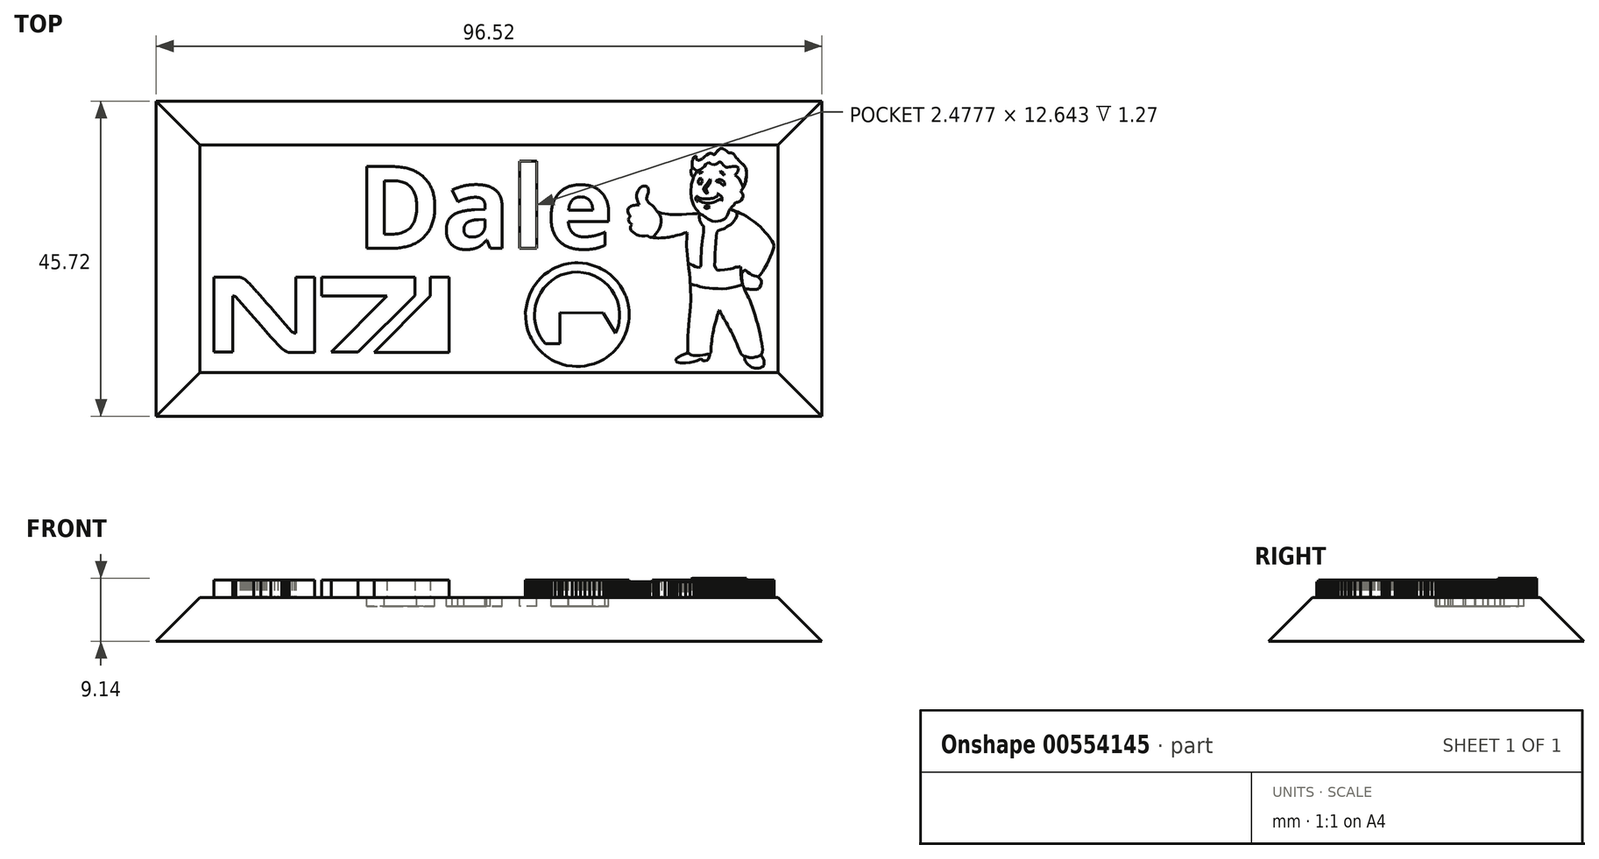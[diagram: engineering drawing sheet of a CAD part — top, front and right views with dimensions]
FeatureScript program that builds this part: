
annotation { "Feature Type Name" : "Feature", "Feature Type Description" : "" }
export const myFeature = defineFeature(function(context is Context, id is Id, definition is map)
    precondition{}
    {
        {
            var Q0;
            Q0=qCreatedBy(makeId("Top.planeOp"),FACE);
            var sketch = newSketch(context, id + "F0", { "sketchPlane" : qUnion([Q0])});
            skLineSegment(sketch, "E0.bottom", {"start": v(50.8, -25.4) * mm, "end": v(-50.8, -25.4) * mm});
            skLineSegment(sketch, "E0.top", {"start": v(50.8, 25.4) * mm, "end": v(-50.8, 25.4) * mm});
            skLineSegment(sketch, "E0.left", {"start": v(50.8, -25.4) * mm, "end": v(50.8, 25.4) * mm});
            skLineSegment(sketch, "E0.right", {"start": v(-50.8, -25.4) * mm, "end": v(-50.8, 25.4) * mm});
            skPoint(sketch, "E0.middle", {"position": v(0, 0) * mm});
            skSolve(sketch);
        }
        {
            var Q0;
            Q0 = qSketchRegion(id + "F0", true);
            extrude(context, id + "F1", {"entities" : qUnion([Q0]), "depth" : 6.35 * mm, "offsetDistance" : 25.4 * mm});
        }
        {
            var Q0;
            Q0=makeQuery(id+"F1.opExtrude","CAP_EDGE",EDGE,{"disambiguationData":[OSD([sQuery(id+"F0.wireOp",EDGE,"E0.right")])],"isStart":false});
            var Q1;
            Q1=makeQuery(id+"F1.opExtrude","CAP_EDGE",EDGE,{"disambiguationData":[OSD([sQuery(id+"F0.wireOp",EDGE,"E0.top")])],"isStart":false});
            var Q2;
            Q2=makeQuery(id+"F1.opExtrude","CAP_EDGE",EDGE,{"disambiguationData":[OSD([sQuery(id+"F0.wireOp",EDGE,"E0.left")])],"isStart":false});
            var Q3;
            Q3=makeQuery(id+"F1.opExtrude","CAP_EDGE",EDGE,{"disambiguationData":[OSD([sQuery(id+"F0.wireOp",EDGE,"E0.bottom")])],"isStart":false});
            chamfer(context, id + "F2", {"entities" : qUnion([Q0, Q1, Q2, Q3]), "width" : 8.9 * mm, "tangentPropagation" : true});
        }
        {
            var Q0;
            Q0=makeQuery(id+"F1.opExtrude","CAP_FACE",FACE,{"disambiguationData":[OSD([sQuery(id+"F0.wireOp",EDGE,"E0.bottom"),sQuery(id+"F0.wireOp",EDGE,"E0.top"),sQuery(id+"F0.wireOp",EDGE,"E0.left"),sQuery(id+"F0.wireOp",EDGE,"E0.right")])],"isStart":false});
            var sketch = newSketch(context, id + "F3", { "sketchPlane" : qUnion([Q0])});
            skText(sketch, "E1", { "text": "Dale", "fontName": "OpenSans-Bold.ttf"});
            const initialGuessF3  = {"E1": [-0.01922, 0.00149, 1, 0, 0.01198]};
            skSetInitialGuess(sketch, initialGuessF3);
            skSolve(sketch);
        }
        {
            var Q0;
            Q0=makeQuery(id+"F3.imprint","IMPRINT",FACE,{"disambiguationData":[TD([[makeQuery(id+"F3.imprint","IMPRINT",EDGE,{"derivedFrom":sQuery(id+"F3.wireOp",EDGE,"E1.sketch_text.stroke-0")}),1.0]])]});
            var sketch = newSketch(context, id + "F4", { "sketchPlane" : qUnion([Q0])});
            skLineSegment(sketch, "E2", {"start": v(21.69, 8.01) * mm, "end": v(21.57, 8.24) * mm});
            skLineSegment(sketch, "E3", {"start": v(21.57, 8.24) * mm, "end": v(21.48, 8.48) * mm});
            skLineSegment(sketch, "E4", {"start": v(21.48, 8.48) * mm, "end": v(21.44, 8.64) * mm});
            skLineSegment(sketch, "E5", {"start": v(21.44, 8.64) * mm, "end": v(21.4, 8.93) * mm});
            skLineSegment(sketch, "E6", {"start": v(21.4, 8.93) * mm, "end": v(21.4, 9.24) * mm});
            skLineSegment(sketch, "E7", {"start": v(21.4, 9.24) * mm, "end": v(21.44, 9.52) * mm});
            skLineSegment(sketch, "E8", {"start": v(21.44, 9.52) * mm, "end": v(21.55, 9.82) * mm});
            skLineSegment(sketch, "E9", {"start": v(21.55, 9.82) * mm, "end": v(21.7, 10.05) * mm});
            skLineSegment(sketch, "E10", {"start": v(21.7, 10.05) * mm, "end": v(21.83, 10.2) * mm});
            skLineSegment(sketch, "E11", {"start": v(21.83, 10.2) * mm, "end": v(21.96, 10.34) * mm});
            skLineSegment(sketch, "E12", {"start": v(21.96, 10.34) * mm, "end": v(22.13, 10.44) * mm});
            skLineSegment(sketch, "E13", {"start": v(22.13, 10.44) * mm, "end": v(22.33, 10.53) * mm});
            skLineSegment(sketch, "E14", {"start": v(22.33, 10.53) * mm, "end": v(22.48, 10.55) * mm});
            skLineSegment(sketch, "E15", {"start": v(22.48, 10.55) * mm, "end": v(22.6, 10.55) * mm});
            skLineSegment(sketch, "E16", {"start": v(22.6, 10.55) * mm, "end": v(22.73, 10.54) * mm});
            skLineSegment(sketch, "E17", {"start": v(22.73, 10.54) * mm, "end": v(22.84, 10.5) * mm});
            skLineSegment(sketch, "E18", {"start": v(22.84, 10.5) * mm, "end": v(22.95, 10.38) * mm});
            skLineSegment(sketch, "E19", {"start": v(22.95, 10.38) * mm, "end": v(23.04, 10.2) * mm});
            skLineSegment(sketch, "E20", {"start": v(23.04, 10.2) * mm, "end": v(23.08, 10.07) * mm});
            skLineSegment(sketch, "E21", {"start": v(23.08, 10.07) * mm, "end": v(23.12, 9.92) * mm});
            skLineSegment(sketch, "E22", {"start": v(23.12, 9.92) * mm, "end": v(23.12, 9.76) * mm});
            skLineSegment(sketch, "E23", {"start": v(23.12, 9.76) * mm, "end": v(23.07, 9.57) * mm});
            skLineSegment(sketch, "E24", {"start": v(23.07, 9.57) * mm, "end": v(23.04, 9.45) * mm});
            skLineSegment(sketch, "E25", {"start": v(23.04, 9.45) * mm, "end": v(22.98, 9.3) * mm});
            skLineSegment(sketch, "E26", {"start": v(22.98, 9.3) * mm, "end": v(22.92, 9.15) * mm});
            skLineSegment(sketch, "E27", {"start": v(22.92, 9.15) * mm, "end": v(22.88, 9) * mm});
            skLineSegment(sketch, "E28", {"start": v(22.88, 9) * mm, "end": v(22.85, 8.83) * mm});
            skLineSegment(sketch, "E29", {"start": v(22.85, 8.83) * mm, "end": v(22.86, 8.62) * mm});
            skLineSegment(sketch, "E30", {"start": v(22.86, 8.62) * mm, "end": v(22.96, 8.38) * mm});
            skLineSegment(sketch, "E31", {"start": v(22.96, 8.38) * mm, "end": v(23.1, 8.2) * mm});
            skLineSegment(sketch, "E32", {"start": v(23.1, 8.2) * mm, "end": v(23.3, 8) * mm});
            skLineSegment(sketch, "E33", {"start": v(23.3, 8) * mm, "end": v(23.47, 7.88) * mm});
            skLineSegment(sketch, "E34", {"start": v(23.47, 7.88) * mm, "end": v(23.66, 7.74) * mm});
            skLineSegment(sketch, "E35", {"start": v(23.66, 7.74) * mm, "end": v(23.84, 7.54) * mm});
            skLineSegment(sketch, "E36", {"start": v(23.84, 7.54) * mm, "end": v(24.05, 7.29) * mm});
            skLineSegment(sketch, "E37", {"start": v(24.05, 7.29) * mm, "end": v(24.21, 7.04) * mm});
            skLineSegment(sketch, "E38", {"start": v(24.21, 7.04) * mm, "end": v(24.3, 6.9) * mm});
            skLineSegment(sketch, "E39", {"start": v(24.3, 6.9) * mm, "end": v(24.41, 6.8) * mm});
            skLineSegment(sketch, "E40", {"start": v(24.41, 6.8) * mm, "end": v(24.66, 6.73) * mm});
            skLineSegment(sketch, "E41", {"start": v(24.66, 6.73) * mm, "end": v(25.02, 6.62) * mm});
            skLineSegment(sketch, "E42", {"start": v(25.02, 6.62) * mm, "end": v(25.48, 6.54) * mm});
            skLineSegment(sketch, "E43", {"start": v(25.48, 6.54) * mm, "end": v(25.95, 6.46) * mm});
            skLineSegment(sketch, "E44", {"start": v(25.95, 6.46) * mm, "end": v(26.28, 6.44) * mm});
            skLineSegment(sketch, "E45", {"start": v(26.28, 6.44) * mm, "end": v(26.73, 6.42) * mm});
            skLineSegment(sketch, "E46", {"start": v(26.73, 6.42) * mm, "end": v(27.3, 6.41) * mm});
            skLineSegment(sketch, "E47", {"start": v(27.3, 6.41) * mm, "end": v(27.91, 6.42) * mm});
            skLineSegment(sketch, "E48", {"start": v(27.91, 6.42) * mm, "end": v(28.6, 6.45) * mm});
            skLineSegment(sketch, "E49", {"start": v(28.6, 6.45) * mm, "end": v(29.5, 6.53) * mm});
            skLineSegment(sketch, "E50", {"start": v(29.5, 6.53) * mm, "end": v(30.08, 6.55) * mm});
            skLineSegment(sketch, "E51", {"start": v(30.08, 6.55) * mm, "end": v(30.33, 6.58) * mm});
            skLineSegment(sketch, "E52", {"start": v(30.33, 6.58) * mm, "end": v(30.4, 6.63) * mm});
            skLineSegment(sketch, "E53", {"start": v(30.4, 6.63) * mm, "end": v(30.4, 6.72) * mm});
            skLineSegment(sketch, "E54", {"start": v(30.4, 6.72) * mm, "end": v(30.35, 6.78) * mm});
            skLineSegment(sketch, "E55", {"start": v(30.35, 6.78) * mm, "end": v(30.3, 6.86) * mm});
            skLineSegment(sketch, "E56", {"start": v(30.3, 6.86) * mm, "end": v(30.2, 6.99) * mm});
            skLineSegment(sketch, "E57", {"start": v(30.2, 6.99) * mm, "end": v(30.04, 7.2) * mm});
            skLineSegment(sketch, "E58", {"start": v(30.04, 7.2) * mm, "end": v(29.9, 7.35) * mm});
            skLineSegment(sketch, "E59", {"start": v(29.9, 7.35) * mm, "end": v(29.8, 7.53) * mm});
            skLineSegment(sketch, "E60", {"start": v(29.8, 7.53) * mm, "end": v(29.72, 7.67) * mm});
            skLineSegment(sketch, "E61", {"start": v(29.72, 7.67) * mm, "end": v(29.65, 7.82) * mm});
            skLineSegment(sketch, "E62", {"start": v(29.65, 7.82) * mm, "end": v(29.56, 7.99) * mm});
            skLineSegment(sketch, "E63", {"start": v(29.56, 7.99) * mm, "end": v(29.49, 8.16) * mm});
            skLineSegment(sketch, "E64", {"start": v(29.49, 8.16) * mm, "end": v(29.43, 8.35) * mm});
            skLineSegment(sketch, "E65", {"start": v(29.43, 8.35) * mm, "end": v(29.39, 8.57) * mm});
            skLineSegment(sketch, "E66", {"start": v(29.39, 8.57) * mm, "end": v(29.34, 8.8) * mm});
            skLineSegment(sketch, "E67", {"start": v(29.34, 8.8) * mm, "end": v(29.3, 9.12) * mm});
            skLineSegment(sketch, "E68", {"start": v(29.3, 9.12) * mm, "end": v(29.28, 9.38) * mm});
            skLineSegment(sketch, "E69", {"start": v(29.28, 9.38) * mm, "end": v(29.27, 9.73) * mm});
            skLineSegment(sketch, "E70", {"start": v(29.27, 9.73) * mm, "end": v(29.27, 10.04) * mm});
            skLineSegment(sketch, "E71", {"start": v(29.27, 10.04) * mm, "end": v(29.3, 10.42) * mm});
            skLineSegment(sketch, "E72", {"start": v(29.3, 10.42) * mm, "end": v(29.35, 10.8) * mm});
            skLineSegment(sketch, "E73", {"start": v(29.35, 10.8) * mm, "end": v(29.43, 11.17) * mm});
            skLineSegment(sketch, "E74", {"start": v(29.43, 11.17) * mm, "end": v(29.56, 11.55) * mm});
            skLineSegment(sketch, "E75", {"start": v(29.56, 11.55) * mm, "end": v(29.63, 11.82) * mm});
            skLineSegment(sketch, "E76", {"start": v(29.63, 11.82) * mm, "end": v(29.53, 11.9) * mm});
            skLineSegment(sketch, "E77", {"start": v(29.53, 11.9) * mm, "end": v(29.4, 12.05) * mm});
            skLineSegment(sketch, "E78", {"start": v(29.4, 12.05) * mm, "end": v(29.32, 12.29) * mm});
            skLineSegment(sketch, "E79", {"start": v(29.32, 12.29) * mm, "end": v(29.27, 12.55) * mm});
            skLineSegment(sketch, "E80", {"start": v(29.27, 12.55) * mm, "end": v(29.27, 12.8) * mm});
            skLineSegment(sketch, "E81", {"start": v(29.27, 12.8) * mm, "end": v(29.35, 13) * mm});
            skLineSegment(sketch, "E82", {"start": v(29.35, 13) * mm, "end": v(29.44, 13.12) * mm});
            skLineSegment(sketch, "E83", {"start": v(29.44, 13.12) * mm, "end": v(29.5, 13.2) * mm});
            skLineSegment(sketch, "E84", {"start": v(29.5, 13.2) * mm, "end": v(29.46, 13.38) * mm});
            skLineSegment(sketch, "E85", {"start": v(29.46, 13.38) * mm, "end": v(29.43, 13.67) * mm});
            skLineSegment(sketch, "E86", {"start": v(29.43, 13.67) * mm, "end": v(29.43, 13.88) * mm});
            skLineSegment(sketch, "E87", {"start": v(29.43, 13.88) * mm, "end": v(29.46, 14.12) * mm});
            skLineSegment(sketch, "E88", {"start": v(29.46, 14.12) * mm, "end": v(29.5, 14.3) * mm});
            skLineSegment(sketch, "E89", {"start": v(29.5, 14.3) * mm, "end": v(29.57, 14.47) * mm});
            skLineSegment(sketch, "E90", {"start": v(29.57, 14.47) * mm, "end": v(29.65, 14.66) * mm});
            skLineSegment(sketch, "E91", {"start": v(29.65, 14.66) * mm, "end": v(29.8, 14.81) * mm});
            skLineSegment(sketch, "E92", {"start": v(29.8, 14.81) * mm, "end": v(29.9, 14.89) * mm});
            skLineSegment(sketch, "E93", {"start": v(29.9, 14.89) * mm, "end": v(29.96, 14.92) * mm});
            skLineSegment(sketch, "E94", {"start": v(29.96, 14.92) * mm, "end": v(30, 14.76) * mm});
            skLineSegment(sketch, "E95", {"start": v(30, 14.76) * mm, "end": v(30, 14.63) * mm});
            skLineSegment(sketch, "E96", {"start": v(30, 14.63) * mm, "end": v(30.03, 14.45) * mm});
            skLineSegment(sketch, "E97", {"start": v(30.03, 14.45) * mm, "end": v(30.14, 14.34) * mm});
            skLineSegment(sketch, "E98", {"start": v(30.14, 14.34) * mm, "end": v(30.3, 14.27) * mm});
            skLineSegment(sketch, "E99", {"start": v(30.3, 14.27) * mm, "end": v(30.48, 14.29) * mm});
            skLineSegment(sketch, "E100", {"start": v(30.48, 14.29) * mm, "end": v(30.72, 14.4) * mm});
            skLineSegment(sketch, "E101", {"start": v(30.72, 14.4) * mm, "end": v(30.92, 14.52) * mm});
            skLineSegment(sketch, "E102", {"start": v(30.92, 14.52) * mm, "end": v(31.1, 14.69) * mm});
            skLineSegment(sketch, "E103", {"start": v(31.1, 14.69) * mm, "end": v(31.3, 14.85) * mm});
            skLineSegment(sketch, "E104", {"start": v(31.3, 14.85) * mm, "end": v(31.48, 15.01) * mm});
            skLineSegment(sketch, "E105", {"start": v(31.48, 15.01) * mm, "end": v(31.73, 15.17) * mm});
            skLineSegment(sketch, "E106", {"start": v(31.73, 15.17) * mm, "end": v(31.97, 15.29) * mm});
            skLineSegment(sketch, "E107", {"start": v(31.97, 15.29) * mm, "end": v(32.15, 15.3) * mm});
            skLineSegment(sketch, "E108", {"start": v(32.15, 15.3) * mm, "end": v(32.31, 15.22) * mm});
            skLineSegment(sketch, "E109", {"start": v(32.31, 15.22) * mm, "end": v(32.45, 15.13) * mm});
            skLineSegment(sketch, "E110", {"start": v(32.45, 15.13) * mm, "end": v(32.49, 15.12) * mm});
            skLineSegment(sketch, "E111", {"start": v(32.49, 15.12) * mm, "end": v(32.53, 15.1) * mm});
            skLineSegment(sketch, "E112", {"start": v(32.53, 15.1) * mm, "end": v(32.58, 15.1) * mm});
            skLineSegment(sketch, "E113", {"start": v(32.58, 15.1) * mm, "end": v(32.63, 15.13) * mm});
            skLineSegment(sketch, "E114", {"start": v(32.63, 15.13) * mm, "end": v(32.68, 15.17) * mm});
            skLineSegment(sketch, "E115", {"start": v(32.68, 15.17) * mm, "end": v(32.78, 15.24) * mm});
            skLineSegment(sketch, "E116", {"start": v(32.78, 15.24) * mm, "end": v(32.88, 15.36) * mm});
            skLineSegment(sketch, "E117", {"start": v(32.88, 15.36) * mm, "end": v(32.97, 15.49) * mm});
            skLineSegment(sketch, "E118", {"start": v(32.97, 15.49) * mm, "end": v(33.1, 15.61) * mm});
            skLineSegment(sketch, "E119", {"start": v(33.1, 15.61) * mm, "end": v(33.22, 15.72) * mm});
            skLineSegment(sketch, "E120", {"start": v(33.22, 15.72) * mm, "end": v(33.35, 15.83) * mm});
            skLineSegment(sketch, "E121", {"start": v(33.35, 15.83) * mm, "end": v(33.48, 15.93) * mm});
            skLineSegment(sketch, "E122", {"start": v(33.48, 15.93) * mm, "end": v(33.62, 15.99) * mm});
            skLineSegment(sketch, "E123", {"start": v(33.62, 15.99) * mm, "end": v(33.76, 16) * mm});
            skLineSegment(sketch, "E124", {"start": v(33.76, 16) * mm, "end": v(33.94, 15.94) * mm});
            skLineSegment(sketch, "E125", {"start": v(33.94, 15.94) * mm, "end": v(34.13, 15.85) * mm});
            skLineSegment(sketch, "E126", {"start": v(34.13, 15.85) * mm, "end": v(34.3, 15.72) * mm});
            skLineSegment(sketch, "E127", {"start": v(34.3, 15.72) * mm, "end": v(34.44, 15.57) * mm});
            skLineSegment(sketch, "E128", {"start": v(34.44, 15.57) * mm, "end": v(34.58, 15.45) * mm});
            skLineSegment(sketch, "E129", {"start": v(34.58, 15.45) * mm, "end": v(34.71, 15.38) * mm});
            skLineSegment(sketch, "E130", {"start": v(34.71, 15.38) * mm, "end": v(34.9, 15.34) * mm});
            skLineSegment(sketch, "E131", {"start": v(34.9, 15.34) * mm, "end": v(35.13, 15.34) * mm});
            skLineSegment(sketch, "E132", {"start": v(35.13, 15.34) * mm, "end": v(35.32, 15.31) * mm});
            skLineSegment(sketch, "E133", {"start": v(35.32, 15.31) * mm, "end": v(35.43, 15.2) * mm});
            skLineSegment(sketch, "E134", {"start": v(35.43, 15.2) * mm, "end": v(35.52, 15.11) * mm});
            skLineSegment(sketch, "E135", {"start": v(35.52, 15.11) * mm, "end": v(35.58, 15.02) * mm});
            skLineSegment(sketch, "E136", {"start": v(35.58, 15.02) * mm, "end": v(35.7, 14.87) * mm});
            skLineSegment(sketch, "E137", {"start": v(35.7, 14.87) * mm, "end": v(35.79, 14.73) * mm});
            skLineSegment(sketch, "E138", {"start": v(35.79, 14.73) * mm, "end": v(35.87, 14.63) * mm});
            skLineSegment(sketch, "E139", {"start": v(35.87, 14.63) * mm, "end": v(35.96, 14.54) * mm});
            skLineSegment(sketch, "E140", {"start": v(35.96, 14.54) * mm, "end": v(36.06, 14.43) * mm});
            skLineSegment(sketch, "E141", {"start": v(36.06, 14.43) * mm, "end": v(36.19, 14.29) * mm});
            skLineSegment(sketch, "E142", {"start": v(36.19, 14.29) * mm, "end": v(36.27, 14.19) * mm});
            skLineSegment(sketch, "E143", {"start": v(36.27, 14.19) * mm, "end": v(36.33, 14.11) * mm});
            skLineSegment(sketch, "E144", {"start": v(36.33, 14.11) * mm, "end": v(36.4, 14.04) * mm});
            skLineSegment(sketch, "E145", {"start": v(36.4, 14.04) * mm, "end": v(36.49, 13.96) * mm});
            skLineSegment(sketch, "E146", {"start": v(36.49, 13.96) * mm, "end": v(36.56, 13.88) * mm});
            skLineSegment(sketch, "E147", {"start": v(36.56, 13.88) * mm, "end": v(36.67, 13.78) * mm});
            skLineSegment(sketch, "E148", {"start": v(36.67, 13.78) * mm, "end": v(36.8, 13.69) * mm});
            skLineSegment(sketch, "E149", {"start": v(36.8, 13.69) * mm, "end": v(36.93, 13.55) * mm});
            skLineSegment(sketch, "E150", {"start": v(36.93, 13.55) * mm, "end": v(37.04, 13.42) * mm});
            skLineSegment(sketch, "E151", {"start": v(37.04, 13.42) * mm, "end": v(37.17, 13.2) * mm});
            skLineSegment(sketch, "E152", {"start": v(37.17, 13.2) * mm, "end": v(37.25, 13) * mm});
            skLineSegment(sketch, "E153", {"start": v(37.25, 13) * mm, "end": v(37.3, 12.76) * mm});
            skLineSegment(sketch, "E154", {"start": v(37.3, 12.76) * mm, "end": v(37.33, 12.47) * mm});
            skLineSegment(sketch, "E155", {"start": v(37.33, 12.47) * mm, "end": v(37.35, 12.23) * mm});
            skLineSegment(sketch, "E156", {"start": v(37.35, 12.23) * mm, "end": v(37.33, 11.98) * mm});
            skLineSegment(sketch, "E157", {"start": v(37.33, 11.98) * mm, "end": v(37.32, 11.78) * mm});
            skLineSegment(sketch, "E158", {"start": v(37.32, 11.78) * mm, "end": v(37.26, 11.57) * mm});
            skLineSegment(sketch, "E159", {"start": v(37.26, 11.57) * mm, "end": v(37.22, 11.31) * mm});
            skLineSegment(sketch, "E160", {"start": v(37.22, 11.31) * mm, "end": v(37.17, 11.1) * mm});
            skLineSegment(sketch, "E161", {"start": v(37.17, 11.1) * mm, "end": v(37.11, 10.92) * mm});
            skLineSegment(sketch, "E162", {"start": v(37.11, 10.92) * mm, "end": v(37.05, 10.74) * mm});
            skLineSegment(sketch, "E163", {"start": v(37.05, 10.74) * mm, "end": v(36.97, 10.58) * mm});
            skLineSegment(sketch, "E164", {"start": v(36.97, 10.58) * mm, "end": v(36.87, 10.34) * mm});
            skLineSegment(sketch, "E165", {"start": v(36.87, 10.34) * mm, "end": v(36.74, 10.15) * mm});
            skLineSegment(sketch, "E166", {"start": v(36.74, 10.15) * mm, "end": v(36.63, 9.98) * mm});
            skLineSegment(sketch, "E167", {"start": v(36.63, 9.98) * mm, "end": v(36.48, 9.83) * mm});
            skLineSegment(sketch, "E168", {"start": v(36.48, 9.83) * mm, "end": v(36.56, 9.63) * mm});
            skLineSegment(sketch, "E169", {"start": v(36.56, 9.63) * mm, "end": v(36.75, 9.46) * mm});
            skLineSegment(sketch, "E170", {"start": v(36.75, 9.46) * mm, "end": v(36.83, 9.22) * mm});
            skLineSegment(sketch, "E171", {"start": v(36.83, 9.22) * mm, "end": v(36.8, 9) * mm});
            skLineSegment(sketch, "E172", {"start": v(36.8, 9) * mm, "end": v(36.74, 8.79) * mm});
            skLineSegment(sketch, "E173", {"start": v(36.74, 8.79) * mm, "end": v(36.56, 8.52) * mm});
            skLineSegment(sketch, "E174", {"start": v(36.56, 8.52) * mm, "end": v(36.4, 8.4) * mm});
            skLineSegment(sketch, "E175", {"start": v(36.4, 8.4) * mm, "end": v(36.18, 8.26) * mm});
            skLineSegment(sketch, "E176", {"start": v(36.18, 8.26) * mm, "end": v(36, 8.2) * mm});
            skLineSegment(sketch, "E177", {"start": v(36, 8.2) * mm, "end": v(35.78, 8.16) * mm});
            skLineSegment(sketch, "E178", {"start": v(35.78, 8.16) * mm, "end": v(35.59, 8.03) * mm});
            skLineSegment(sketch, "E179", {"start": v(35.59, 8.03) * mm, "end": v(35.51, 7.8) * mm});
            skLineSegment(sketch, "E180", {"start": v(35.51, 7.8) * mm, "end": v(35.3, 7.6) * mm});
            skLineSegment(sketch, "E181", {"start": v(35.3, 7.6) * mm, "end": v(35.12, 7.42) * mm});
            skLineSegment(sketch, "E182", {"start": v(35.12, 7.42) * mm, "end": v(35.04, 7.27) * mm});
            skLineSegment(sketch, "E183", {"start": v(35.04, 7.27) * mm, "end": v(35.12, 7.14) * mm});
            skLineSegment(sketch, "E184", {"start": v(35.12, 7.14) * mm, "end": v(35.4, 7.03) * mm});
            skLineSegment(sketch, "E185", {"start": v(35.4, 7.03) * mm, "end": v(35.69, 6.92) * mm});
            skLineSegment(sketch, "E186", {"start": v(35.69, 6.92) * mm, "end": v(36.03, 6.79) * mm});
            skLineSegment(sketch, "E187", {"start": v(36.03, 6.79) * mm, "end": v(36.39, 6.63) * mm});
            skLineSegment(sketch, "E188", {"start": v(36.39, 6.63) * mm, "end": v(36.84, 6.43) * mm});
            skLineSegment(sketch, "E189", {"start": v(36.84, 6.43) * mm, "end": v(37.3, 6.16) * mm});
            skLineSegment(sketch, "E190", {"start": v(37.3, 6.16) * mm, "end": v(37.84, 5.8) * mm});
            skLineSegment(sketch, "E191", {"start": v(37.84, 5.8) * mm, "end": v(38.38, 5.4) * mm});
            skLineSegment(sketch, "E192", {"start": v(38.38, 5.4) * mm, "end": v(38.94, 4.96) * mm});
            skLineSegment(sketch, "E193", {"start": v(38.94, 4.96) * mm, "end": v(39.33, 4.62) * mm});
            skLineSegment(sketch, "E194", {"start": v(39.33, 4.62) * mm, "end": v(39.67, 4.27) * mm});
            skLineSegment(sketch, "E195", {"start": v(39.67, 4.27) * mm, "end": v(40.08, 3.81) * mm});
            skLineSegment(sketch, "E196", {"start": v(40.08, 3.81) * mm, "end": v(40.44, 3.44) * mm});
            skLineSegment(sketch, "E197", {"start": v(40.44, 3.44) * mm, "end": v(40.76, 3) * mm});
            skLineSegment(sketch, "E198", {"start": v(40.76, 3) * mm, "end": v(41, 2.62) * mm});
            skLineSegment(sketch, "E199", {"start": v(41, 2.62) * mm, "end": v(41.2, 2.25) * mm});
            skLineSegment(sketch, "E200", {"start": v(41.2, 2.25) * mm, "end": v(41.33, 1.83) * mm});
            skLineSegment(sketch, "E201", {"start": v(41.33, 1.83) * mm, "end": v(41.22, 1.37) * mm});
            skLineSegment(sketch, "E202", {"start": v(41.22, 1.37) * mm, "end": v(41.02, 0.8) * mm});
            skLineSegment(sketch, "E203", {"start": v(41.02, 0.8) * mm, "end": v(40.76, 0.26) * mm});
            skLineSegment(sketch, "E204", {"start": v(40.76, 0.26) * mm, "end": v(40.54, -0.22) * mm});
            skLineSegment(sketch, "E205", {"start": v(40.54, -0.22) * mm, "end": v(40.29, -0.78) * mm});
            skLineSegment(sketch, "E206", {"start": v(40.29, -0.78) * mm, "end": v(39.95, -1.39) * mm});
            skLineSegment(sketch, "E207", {"start": v(39.95, -1.39) * mm, "end": v(39.67, -1.83) * mm});
            skLineSegment(sketch, "E208", {"start": v(39.67, -1.83) * mm, "end": v(39.35, -2.26) * mm});
            skLineSegment(sketch, "E209", {"start": v(39.35, -2.26) * mm, "end": v(39.07, -2.55) * mm});
            skLineSegment(sketch, "E210", {"start": v(39.07, -2.55) * mm, "end": v(39.01, -2.68) * mm});
            skLineSegment(sketch, "E211", {"start": v(39.01, -2.68) * mm, "end": v(39.25, -2.88) * mm});
            skLineSegment(sketch, "E212", {"start": v(39.25, -2.88) * mm, "end": v(39.4, -3.03) * mm});
            skLineSegment(sketch, "E213", {"start": v(39.4, -3.03) * mm, "end": v(39.48, -3.24) * mm});
            skLineSegment(sketch, "E214", {"start": v(39.48, -3.24) * mm, "end": v(39.48, -3.5) * mm});
            skLineSegment(sketch, "E215", {"start": v(39.48, -3.5) * mm, "end": v(39.42, -3.83) * mm});
            skLineSegment(sketch, "E216", {"start": v(39.42, -3.83) * mm, "end": v(39.25, -4.13) * mm});
            skLineSegment(sketch, "E217", {"start": v(39.25, -4.13) * mm, "end": v(39.1, -4.37) * mm});
            skLineSegment(sketch, "E218", {"start": v(39.1, -4.37) * mm, "end": v(38.92, -4.42) * mm});
            skLineSegment(sketch, "E219", {"start": v(29.21, -4.75) * mm, "end": v(29.2, -4.71) * mm});
            skLineSegment(sketch, "E220", {"start": v(29.21, -4.75) * mm, "end": v(29.19, -4.27) * mm});
            skLineSegment(sketch, "E221", {"start": v(29.19, -4.27) * mm, "end": v(29.16, -3.76) * mm});
            skLineSegment(sketch, "E222", {"start": v(29.16, -3.76) * mm, "end": v(29.15, -3.34) * mm});
            skLineSegment(sketch, "E223", {"start": v(29.15, -3.34) * mm, "end": v(29.12, -2.92) * mm});
            skLineSegment(sketch, "E224", {"start": v(29.12, -2.92) * mm, "end": v(29.07, -2.13) * mm});
            skLineSegment(sketch, "E225", {"start": v(29.07, -2.13) * mm, "end": v(28.97, -1.43) * mm});
            skLineSegment(sketch, "E226", {"start": v(28.97, -1.43) * mm, "end": v(28.88, -0.7) * mm});
            skLineSegment(sketch, "E227", {"start": v(28.88, -0.7) * mm, "end": v(28.8, -0.13) * mm});
            skLineSegment(sketch, "E228", {"start": v(28.8, -0.13) * mm, "end": v(28.73, 0.55) * mm});
            skLineSegment(sketch, "E229", {"start": v(28.73, 0.55) * mm, "end": v(28.67, 1.2) * mm});
            skLineSegment(sketch, "E230", {"start": v(28.67, 1.2) * mm, "end": v(28.64, 1.85) * mm});
            skLineSegment(sketch, "E231", {"start": v(28.64, 1.85) * mm, "end": v(28.63, 2.4) * mm});
            skLineSegment(sketch, "E232", {"start": v(28.63, 2.4) * mm, "end": v(28.67, 2.94) * mm});
            skLineSegment(sketch, "E233", {"start": v(28.67, 2.94) * mm, "end": v(28.69, 3.44) * mm});
            skLineSegment(sketch, "E234", {"start": v(28.69, 3.44) * mm, "end": v(28.72, 3.67) * mm});
            skLineSegment(sketch, "E235", {"start": v(28.72, 3.67) * mm, "end": v(28.7, 3.78) * mm});
            skLineSegment(sketch, "E236", {"start": v(28.7, 3.78) * mm, "end": v(28.59, 3.79) * mm});
            skLineSegment(sketch, "E237", {"start": v(28.59, 3.79) * mm, "end": v(28.3, 3.73) * mm});
            skLineSegment(sketch, "E238", {"start": v(28.3, 3.73) * mm, "end": v(28.07, 3.65) * mm});
            skLineSegment(sketch, "E239", {"start": v(28.07, 3.65) * mm, "end": v(27.93, 3.57) * mm});
            skLineSegment(sketch, "E240", {"start": v(27.93, 3.57) * mm, "end": v(27.68, 3.51) * mm});
            skLineSegment(sketch, "E241", {"start": v(27.68, 3.51) * mm, "end": v(27.28, 3.4) * mm});
            skLineSegment(sketch, "E242", {"start": v(27.28, 3.4) * mm, "end": v(27, 3.33) * mm});
            skLineSegment(sketch, "E243", {"start": v(27, 3.33) * mm, "end": v(26.74, 3.26) * mm});
            skLineSegment(sketch, "E244", {"start": v(26.74, 3.26) * mm, "end": v(26.5, 3.21) * mm});
            skLineSegment(sketch, "E245", {"start": v(26.5, 3.21) * mm, "end": v(26.28, 3.15) * mm});
            skLineSegment(sketch, "E246", {"start": v(26.28, 3.15) * mm, "end": v(26.1, 3.13) * mm});
            skLineSegment(sketch, "E247", {"start": v(26.1, 3.13) * mm, "end": v(25.86, 3.1) * mm});
            skLineSegment(sketch, "E248", {"start": v(25.86, 3.1) * mm, "end": v(25.54, 3.04) * mm});
            skLineSegment(sketch, "E249", {"start": v(25.54, 3.04) * mm, "end": v(25.24, 3.03) * mm});
            skLineSegment(sketch, "E250", {"start": v(25.24, 3.03) * mm, "end": v(24.9, 3.01) * mm});
            skLineSegment(sketch, "E251", {"start": v(24.9, 3.01) * mm, "end": v(24.58, 3) * mm});
            skLineSegment(sketch, "E252", {"start": v(24.58, 3) * mm, "end": v(24.24, 3.01) * mm});
            skLineSegment(sketch, "E253", {"start": v(24.24, 3.01) * mm, "end": v(23.88, 3.05) * mm});
            skLineSegment(sketch, "E254", {"start": v(23.88, 3.05) * mm, "end": v(23.62, 3.09) * mm});
            skLineSegment(sketch, "E255", {"start": v(23.62, 3.09) * mm, "end": v(23.31, 3.13) * mm});
            skLineSegment(sketch, "E256", {"start": v(23.31, 3.13) * mm, "end": v(23.1, 3.23) * mm});
            skLineSegment(sketch, "E257", {"start": v(23.1, 3.23) * mm, "end": v(22.94, 3.34) * mm});
            skLineSegment(sketch, "E258", {"start": v(22.94, 3.34) * mm, "end": v(22.62, 3.3) * mm});
            skLineSegment(sketch, "E259", {"start": v(22.62, 3.3) * mm, "end": v(22.12, 3.29) * mm});
            skLineSegment(sketch, "E260", {"start": v(22.12, 3.29) * mm, "end": v(21.78, 3.35) * mm});
            skLineSegment(sketch, "E261", {"start": v(21.78, 3.35) * mm, "end": v(21.4, 3.48) * mm});
            skLineSegment(sketch, "E262", {"start": v(21.4, 3.48) * mm, "end": v(21.1, 3.68) * mm});
            skLineSegment(sketch, "E263", {"start": v(21.1, 3.68) * mm, "end": v(20.84, 3.87) * mm});
            skLineSegment(sketch, "E264", {"start": v(20.84, 3.87) * mm, "end": v(20.62, 4.08) * mm});
            skLineSegment(sketch, "E265", {"start": v(20.62, 4.08) * mm, "end": v(20.56, 4.22) * mm});
            skLineSegment(sketch, "E266", {"start": v(20.56, 4.22) * mm, "end": v(20.48, 4.4) * mm});
            skLineSegment(sketch, "E267", {"start": v(20.48, 4.4) * mm, "end": v(20.47, 4.6) * mm});
            skLineSegment(sketch, "E268", {"start": v(20.47, 4.6) * mm, "end": v(20.54, 4.78) * mm});
            skLineSegment(sketch, "E269", {"start": v(20.54, 4.78) * mm, "end": v(20.67, 4.92) * mm});
            skLineSegment(sketch, "E270", {"start": v(20.67, 4.92) * mm, "end": v(20.61, 5.07) * mm});
            skLineSegment(sketch, "E271", {"start": v(20.61, 5.07) * mm, "end": v(20.46, 5.19) * mm});
            skLineSegment(sketch, "E272", {"start": v(20.46, 5.19) * mm, "end": v(20.29, 5.35) * mm});
            skLineSegment(sketch, "E273", {"start": v(20.29, 5.35) * mm, "end": v(20.2, 5.56) * mm});
            skLineSegment(sketch, "E274", {"start": v(20.2, 5.56) * mm, "end": v(20.19, 5.71) * mm});
            skLineSegment(sketch, "E275", {"start": v(20.19, 5.71) * mm, "end": v(20.26, 5.87) * mm});
            skLineSegment(sketch, "E276", {"start": v(20.26, 5.87) * mm, "end": v(20.37, 6.02) * mm});
            skLineSegment(sketch, "E277", {"start": v(20.37, 6.02) * mm, "end": v(20.44, 6.16) * mm});
            skLineSegment(sketch, "E278", {"start": v(20.44, 6.16) * mm, "end": v(20.4, 6.27) * mm});
            skLineSegment(sketch, "E279", {"start": v(20.4, 6.27) * mm, "end": v(20.3, 6.41) * mm});
            skLineSegment(sketch, "E280", {"start": v(20.3, 6.41) * mm, "end": v(20.24, 6.5) * mm});
            skLineSegment(sketch, "E281", {"start": v(20.24, 6.5) * mm, "end": v(20.17, 6.67) * mm});
            skLineSegment(sketch, "E282", {"start": v(20.17, 6.67) * mm, "end": v(20.13, 6.84) * mm});
            skLineSegment(sketch, "E283", {"start": v(20.13, 6.84) * mm, "end": v(20.13, 7.08) * mm});
            skLineSegment(sketch, "E284", {"start": v(20.13, 7.08) * mm, "end": v(20.18, 7.28) * mm});
            skLineSegment(sketch, "E285", {"start": v(20.18, 7.28) * mm, "end": v(20.33, 7.46) * mm});
            skLineSegment(sketch, "E286", {"start": v(20.33, 7.46) * mm, "end": v(20.56, 7.63) * mm});
            skLineSegment(sketch, "E287", {"start": v(20.56, 7.63) * mm, "end": v(20.84, 7.74) * mm});
            skLineSegment(sketch, "E288", {"start": v(20.84, 7.74) * mm, "end": v(21.08, 7.77) * mm});
            skLineSegment(sketch, "E289", {"start": v(21.08, 7.77) * mm, "end": v(21.32, 7.79) * mm});
            skLineSegment(sketch, "E290", {"start": v(21.32, 7.79) * mm, "end": v(21.58, 7.8) * mm});
            skLineSegment(sketch, "E291", {"start": v(21.58, 7.8) * mm, "end": v(21.74, 7.8) * mm});
            skLineSegment(sketch, "E292", {"start": v(21.74, 7.8) * mm, "end": v(21.69, 8.01) * mm});
            skLineSegment(sketch, "E293", {"start": v(29.63, 11.82) * mm, "end": v(29.76, 12.06) * mm});
            skLineSegment(sketch, "E294", {"start": v(29.76, 12.06) * mm, "end": v(29.9, 12.33) * mm});
            skLineSegment(sketch, "E295", {"start": v(29.9, 12.33) * mm, "end": v(30.04, 12.55) * mm});
            skLineSegment(sketch, "E296", {"start": v(30.04, 12.55) * mm, "end": v(30.17, 12.73) * mm});
            skLineSegment(sketch, "E297", {"start": v(30.17, 12.73) * mm, "end": v(30.33, 12.84) * mm});
            skLineSegment(sketch, "E298", {"start": v(30.33, 12.84) * mm, "end": v(30.58, 12.93) * mm});
            skLineSegment(sketch, "E299", {"start": v(30.58, 12.93) * mm, "end": v(30.7, 13) * mm});
            skLineSegment(sketch, "E300", {"start": v(30.7, 13) * mm, "end": v(30.87, 13.13) * mm});
            skLineSegment(sketch, "E301", {"start": v(30.87, 13.13) * mm, "end": v(31.06, 13.3) * mm});
            skLineSegment(sketch, "E302", {"start": v(38.92, -4.42) * mm, "end": v(38.79, -4.43) * mm});
            skLineSegment(sketch, "E303", {"start": v(38.79, -4.43) * mm, "end": v(38.63, -4.43) * mm});
            skLineSegment(sketch, "E304", {"start": v(38.63, -4.43) * mm, "end": v(38.35, -4.43) * mm});
            skLineSegment(sketch, "E305", {"start": v(38.35, -4.43) * mm, "end": v(38.1, -4.42) * mm});
            skLineSegment(sketch, "E306", {"start": v(38.1, -4.42) * mm, "end": v(37.85, -4.42) * mm});
            skLineSegment(sketch, "E307", {"start": v(37.85, -4.42) * mm, "end": v(37.63, -4.42) * mm});
            skLineSegment(sketch, "E308", {"start": v(37.63, -4.42) * mm, "end": v(37.4, -4.4) * mm});
            skLineSegment(sketch, "E309", {"start": v(37.4, -4.4) * mm, "end": v(37.18, -4.36) * mm});
            skLineSegment(sketch, "E310", {"start": v(37.18, -4.36) * mm, "end": v(37.07, -4.38) * mm});
            skLineSegment(sketch, "E311", {"start": v(37.07, -4.38) * mm, "end": v(37.09, -4.53) * mm});
            skLineSegment(sketch, "E312", {"start": v(37.09, -4.53) * mm, "end": v(37.47, -5.31) * mm});
            skLineSegment(sketch, "E313", {"start": v(37.47, -5.31) * mm, "end": v(37.64, -5.68) * mm});
            skLineSegment(sketch, "E314", {"start": v(37.64, -5.68) * mm, "end": v(37.8, -6.06) * mm});
            skLineSegment(sketch, "E315", {"start": v(37.8, -6.06) * mm, "end": v(37.97, -6.45) * mm});
            skLineSegment(sketch, "E316", {"start": v(37.97, -6.45) * mm, "end": v(38.2, -7.11) * mm});
            skLineSegment(sketch, "E317", {"start": v(38.2, -7.11) * mm, "end": v(38.51, -8.08) * mm});
            skLineSegment(sketch, "E318", {"start": v(38.51, -8.08) * mm, "end": v(38.8, -9) * mm});
            skLineSegment(sketch, "E319", {"start": v(38.8, -9) * mm, "end": v(38.95, -9.52) * mm});
            skLineSegment(sketch, "E320", {"start": v(38.95, -9.52) * mm, "end": v(39.17, -10.39) * mm});
            skLineSegment(sketch, "E321", {"start": v(39.17, -10.39) * mm, "end": v(39.3, -10.92) * mm});
            skLineSegment(sketch, "E322", {"start": v(39.3, -10.92) * mm, "end": v(39.36, -11.28) * mm});
            skLineSegment(sketch, "E323", {"start": v(39.36, -11.28) * mm, "end": v(39.44, -11.74) * mm});
            skLineSegment(sketch, "E324", {"start": v(39.44, -11.74) * mm, "end": v(39.52, -12.24) * mm});
            skLineSegment(sketch, "E325", {"start": v(39.52, -12.24) * mm, "end": v(39.61, -12.75) * mm});
            skLineSegment(sketch, "E326", {"start": v(39.61, -12.75) * mm, "end": v(39.64, -13.16) * mm});
            skLineSegment(sketch, "E327", {"start": v(39.64, -13.16) * mm, "end": v(39.6, -13.6) * mm});
            skLineSegment(sketch, "E328", {"start": v(39.6, -13.6) * mm, "end": v(39.5, -13.85) * mm});
            skLineSegment(sketch, "E329", {"start": v(39.5, -13.85) * mm, "end": v(39.48, -13.94) * mm});
            skLineSegment(sketch, "E330", {"start": v(39.48, -13.94) * mm, "end": v(39.5, -14.05) * mm});
            skLineSegment(sketch, "E331", {"start": v(39.5, -14.05) * mm, "end": v(39.62, -14.22) * mm});
            skLineSegment(sketch, "E332", {"start": v(39.62, -14.22) * mm, "end": v(39.72, -14.46) * mm});
            skLineSegment(sketch, "E333", {"start": v(39.72, -14.46) * mm, "end": v(39.77, -14.6) * mm});
            skLineSegment(sketch, "E334", {"start": v(39.77, -14.6) * mm, "end": v(39.83, -14.77) * mm});
            skLineSegment(sketch, "E335", {"start": v(39.83, -14.77) * mm, "end": v(39.86, -15) * mm});
            skLineSegment(sketch, "E336", {"start": v(39.86, -15) * mm, "end": v(39.87, -15.21) * mm});
            skLineSegment(sketch, "E337", {"start": v(39.87, -15.21) * mm, "end": v(39.85, -15.4) * mm});
            skLineSegment(sketch, "E338", {"start": v(39.85, -15.4) * mm, "end": v(39.71, -15.6) * mm});
            skLineSegment(sketch, "E339", {"start": v(39.71, -15.6) * mm, "end": v(39.53, -15.72) * mm});
            skLineSegment(sketch, "E340", {"start": v(39.53, -15.72) * mm, "end": v(39.35, -15.81) * mm});
            skLineSegment(sketch, "E341", {"start": v(39.35, -15.81) * mm, "end": v(39.12, -15.85) * mm});
            skLineSegment(sketch, "E342", {"start": v(39.12, -15.85) * mm, "end": v(38.92, -15.87) * mm});
            skLineSegment(sketch, "E343", {"start": v(38.92, -15.87) * mm, "end": v(38.73, -15.88) * mm});
            skLineSegment(sketch, "E344", {"start": v(38.73, -15.88) * mm, "end": v(38.53, -15.86) * mm});
            skLineSegment(sketch, "E345", {"start": v(38.53, -15.86) * mm, "end": v(38.33, -15.81) * mm});
            skLineSegment(sketch, "E346", {"start": v(38.33, -15.81) * mm, "end": v(38.07, -15.73) * mm});
            skLineSegment(sketch, "E347", {"start": v(38.07, -15.73) * mm, "end": v(37.8, -15.6) * mm});
            skLineSegment(sketch, "E348", {"start": v(37.8, -15.6) * mm, "end": v(37.59, -15.38) * mm});
            skLineSegment(sketch, "E349", {"start": v(37.59, -15.38) * mm, "end": v(37.4, -15.2) * mm});
            skLineSegment(sketch, "E350", {"start": v(37.4, -15.2) * mm, "end": v(37.27, -15.01) * mm});
            skLineSegment(sketch, "E351", {"start": v(37.27, -15.01) * mm, "end": v(37.15, -14.81) * mm});
            skLineSegment(sketch, "E352", {"start": v(37.15, -14.81) * mm, "end": v(37.1, -14.6) * mm});
            skLineSegment(sketch, "E353", {"start": v(37.1, -14.6) * mm, "end": v(37.06, -14.4) * mm});
            skLineSegment(sketch, "E354", {"start": v(37.06, -14.4) * mm, "end": v(37.05, -14.25) * mm});
            skLineSegment(sketch, "E355", {"start": v(37.05, -14.25) * mm, "end": v(36.78, -14.05) * mm});
            skLineSegment(sketch, "E356", {"start": v(36.78, -14.05) * mm, "end": v(36.58, -13.82) * mm});
            skLineSegment(sketch, "E357", {"start": v(36.58, -13.82) * mm, "end": v(36.44, -13.6) * mm});
            skLineSegment(sketch, "E358", {"start": v(36.44, -13.6) * mm, "end": v(36.28, -13.27) * mm});
            skLineSegment(sketch, "E359", {"start": v(36.28, -13.27) * mm, "end": v(36.16, -13) * mm});
            skLineSegment(sketch, "E360", {"start": v(36.16, -13) * mm, "end": v(36.04, -12.7) * mm});
            skLineSegment(sketch, "E361", {"start": v(36.04, -12.7) * mm, "end": v(35.9, -12.35) * mm});
            skLineSegment(sketch, "E362", {"start": v(35.9, -12.35) * mm, "end": v(35.74, -11.93) * mm});
            skLineSegment(sketch, "E363", {"start": v(35.74, -11.93) * mm, "end": v(35.54, -11.48) * mm});
            skLineSegment(sketch, "E364", {"start": v(35.54, -11.48) * mm, "end": v(35.32, -11.06) * mm});
            skLineSegment(sketch, "E365", {"start": v(35.32, -11.06) * mm, "end": v(35.08, -10.55) * mm});
            skLineSegment(sketch, "E366", {"start": v(35.08, -10.55) * mm, "end": v(34.9, -10.2) * mm});
            skLineSegment(sketch, "E367", {"start": v(34.9, -10.2) * mm, "end": v(34.68, -9.82) * mm});
            skLineSegment(sketch, "E368", {"start": v(34.68, -9.82) * mm, "end": v(34.56, -9.62) * mm});
            skLineSegment(sketch, "E369", {"start": v(34.56, -9.62) * mm, "end": v(34.37, -9.28) * mm});
            skLineSegment(sketch, "E370", {"start": v(34.37, -9.28) * mm, "end": v(34.17, -8.91) * mm});
            skLineSegment(sketch, "E371", {"start": v(34.17, -8.91) * mm, "end": v(34, -8.62) * mm});
            skLineSegment(sketch, "E372", {"start": v(34, -8.62) * mm, "end": v(33.83, -8.32) * mm});
            skLineSegment(sketch, "E373", {"start": v(33.83, -8.32) * mm, "end": v(33.57, -7.84) * mm});
            skLineSegment(sketch, "E374", {"start": v(33.57, -7.84) * mm, "end": v(33.38, -7.5) * mm});
            skLineSegment(sketch, "E375", {"start": v(33.38, -7.5) * mm, "end": v(33.28, -7.53) * mm});
            skLineSegment(sketch, "E376", {"start": v(33.28, -7.53) * mm, "end": v(33.23, -7.68) * mm});
            skLineSegment(sketch, "E377", {"start": v(33.23, -7.68) * mm, "end": v(33.17, -7.95) * mm});
            skLineSegment(sketch, "E378", {"start": v(33.17, -7.95) * mm, "end": v(33.06, -8.28) * mm});
            skLineSegment(sketch, "E379", {"start": v(33.06, -8.28) * mm, "end": v(33, -8.58) * mm});
            skLineSegment(sketch, "E380", {"start": v(33, -8.58) * mm, "end": v(32.91, -8.87) * mm});
            skLineSegment(sketch, "E381", {"start": v(32.91, -8.87) * mm, "end": v(32.78, -9.26) * mm});
            skLineSegment(sketch, "E382", {"start": v(32.78, -9.26) * mm, "end": v(32.73, -9.46) * mm});
            skLineSegment(sketch, "E383", {"start": v(32.73, -9.46) * mm, "end": v(32.7, -9.68) * mm});
            skLineSegment(sketch, "E384", {"start": v(32.7, -9.68) * mm, "end": v(32.64, -9.94) * mm});
            skLineSegment(sketch, "E385", {"start": v(32.64, -9.94) * mm, "end": v(32.57, -10.18) * mm});
            skLineSegment(sketch, "E386", {"start": v(32.57, -10.18) * mm, "end": v(32.53, -10.45) * mm});
            skLineSegment(sketch, "E387", {"start": v(32.53, -10.45) * mm, "end": v(32.46, -10.86) * mm});
            skLineSegment(sketch, "E388", {"start": v(32.46, -10.86) * mm, "end": v(32.39, -11.27) * mm});
            skLineSegment(sketch, "E389", {"start": v(32.39, -11.27) * mm, "end": v(32.31, -11.6) * mm});
            skLineSegment(sketch, "E390", {"start": v(32.31, -11.6) * mm, "end": v(32.27, -12) * mm});
            skLineSegment(sketch, "E391", {"start": v(32.27, -12) * mm, "end": v(32.22, -12.28) * mm});
            skLineSegment(sketch, "E392", {"start": v(32.22, -12.28) * mm, "end": v(32.2, -12.8) * mm});
            skLineSegment(sketch, "E393", {"start": v(32.2, -12.8) * mm, "end": v(32.2, -13.32) * mm});
            skLineSegment(sketch, "E394", {"start": v(32.2, -13.32) * mm, "end": v(32.2, -13.6) * mm});
            skLineSegment(sketch, "E395", {"start": v(32.2, -13.6) * mm, "end": v(31.98, -13.82) * mm});
            skLineSegment(sketch, "E396", {"start": v(31.98, -13.82) * mm, "end": v(31.93, -14.18) * mm});
            skLineSegment(sketch, "E397", {"start": v(31.93, -14.18) * mm, "end": v(31.81, -14.53) * mm});
            skLineSegment(sketch, "E398", {"start": v(31.81, -14.53) * mm, "end": v(31.58, -14.7) * mm});
            skLineSegment(sketch, "E399", {"start": v(31.58, -14.7) * mm, "end": v(31.27, -14.83) * mm});
            skLineSegment(sketch, "E400", {"start": v(31.27, -14.83) * mm, "end": v(30.96, -14.8) * mm});
            skLineSegment(sketch, "E401", {"start": v(30.96, -14.8) * mm, "end": v(30.81, -14.62) * mm});
            skLineSegment(sketch, "E402", {"start": v(30.81, -14.62) * mm, "end": v(30.7, -14.52) * mm});
            skLineSegment(sketch, "E403", {"start": v(30.7, -14.52) * mm, "end": v(30.51, -14.63) * mm});
            skLineSegment(sketch, "E404", {"start": v(30.51, -14.63) * mm, "end": v(30.13, -14.8) * mm});
            skLineSegment(sketch, "E405", {"start": v(30.13, -14.8) * mm, "end": v(29.7, -14.92) * mm});
            skLineSegment(sketch, "E406", {"start": v(29.7, -14.92) * mm, "end": v(29.14, -15.05) * mm});
            skLineSegment(sketch, "E407", {"start": v(29.14, -15.05) * mm, "end": v(28.51, -15.11) * mm});
            skLineSegment(sketch, "E408", {"start": v(28.51, -15.11) * mm, "end": v(27.73, -15.14) * mm});
            skLineSegment(sketch, "E409", {"start": v(27.73, -15.14) * mm, "end": v(27.2, -15) * mm});
            skLineSegment(sketch, "E410", {"start": v(27.2, -15) * mm, "end": v(27.06, -14.78) * mm});
            skLineSegment(sketch, "E411", {"start": v(27.06, -14.78) * mm, "end": v(27.11, -14.53) * mm});
            skLineSegment(sketch, "E412", {"start": v(27.11, -14.53) * mm, "end": v(27.4, -14.3) * mm});
            skLineSegment(sketch, "E413", {"start": v(27.4, -14.3) * mm, "end": v(27.84, -14.04) * mm});
            skLineSegment(sketch, "E414", {"start": v(27.84, -14.04) * mm, "end": v(28.32, -13.88) * mm});
            skLineSegment(sketch, "E415", {"start": v(28.32, -13.88) * mm, "end": v(28.77, -13.68) * mm});
            skLineSegment(sketch, "E416", {"start": v(28.77, -13.68) * mm, "end": v(28.8, -13.36) * mm});
            skLineSegment(sketch, "E417", {"start": v(28.8, -13.36) * mm, "end": v(28.78, -12.78) * mm});
            skLineSegment(sketch, "E418", {"start": v(28.78, -12.78) * mm, "end": v(28.8, -12.04) * mm});
            skLineSegment(sketch, "E419", {"start": v(28.8, -12.04) * mm, "end": v(28.83, -11.22) * mm});
            skLineSegment(sketch, "E420", {"start": v(28.83, -11.22) * mm, "end": v(28.86, -10.48) * mm});
            skLineSegment(sketch, "E421", {"start": v(28.86, -10.48) * mm, "end": v(28.91, -9.65) * mm});
            skLineSegment(sketch, "E422", {"start": v(28.91, -9.65) * mm, "end": v(29, -8.82) * mm});
            skLineSegment(sketch, "E423", {"start": v(29, -8.82) * mm, "end": v(29.08, -7.9) * mm});
            skLineSegment(sketch, "E424", {"start": v(29.08, -7.9) * mm, "end": v(29.17, -6.98) * mm});
            skLineSegment(sketch, "E425", {"start": v(29.17, -6.98) * mm, "end": v(29.27, -5.82) * mm});
            skLineSegment(sketch, "E426", {"start": v(29.27, -5.82) * mm, "end": v(29.26, -5.25) * mm});
            skLineSegment(sketch, "E427", {"start": v(29.26, -5.25) * mm, "end": v(29.21, -4.75) * mm});
            skSolve(sketch);
        }
        {
            var Q0;
            Q0 = qSketchRegion(id + "F4", true);
            extrude(context, id + "F5", {"entities" : qUnion([Q0]), "operationType" : NewBodyOperationType.ADD, "depth" : 2.54 * mm, "offsetDistance" : 25.4 * mm});
        }
        {
            var Q0;
            Q0=makeQuery(id+"F5.opExtrude","CAP_FACE",FACE,{"disambiguationData":[OSD([sQuery(id+"F4.wireOp",EDGE,"E2"),sQuery(id+"F4.wireOp",EDGE,"E3"),sQuery(id+"F4.wireOp",EDGE,"E4"),sQuery(id+"F4.wireOp",EDGE,"E5"),sQuery(id+"F4.wireOp",EDGE,"E6"),sQuery(id+"F4.wireOp",EDGE,"E7"),sQuery(id+"F4.wireOp",EDGE,"E8"),sQuery(id+"F4.wireOp",EDGE,"E9"),sQuery(id+"F4.wireOp",EDGE,"E10"),sQuery(id+"F4.wireOp",EDGE,"E11"),sQuery(id+"F4.wireOp",EDGE,"E12"),sQuery(id+"F4.wireOp",EDGE,"E13"),sQuery(id+"F4.wireOp",EDGE,"E14"),sQuery(id+"F4.wireOp",EDGE,"E15"),sQuery(id+"F4.wireOp",EDGE,"E16"),sQuery(id+"F4.wireOp",EDGE,"E17"),sQuery(id+"F4.wireOp",EDGE,"E18"),sQuery(id+"F4.wireOp",EDGE,"E19"),sQuery(id+"F4.wireOp",EDGE,"E20"),sQuery(id+"F4.wireOp",EDGE,"E21"),sQuery(id+"F4.wireOp",EDGE,"E22"),sQuery(id+"F4.wireOp",EDGE,"E23"),sQuery(id+"F4.wireOp",EDGE,"E24"),sQuery(id+"F4.wireOp",EDGE,"E25"),sQuery(id+"F4.wireOp",EDGE,"E26"),sQuery(id+"F4.wireOp",EDGE,"E27"),sQuery(id+"F4.wireOp",EDGE,"E28"),sQuery(id+"F4.wireOp",EDGE,"E29"),sQuery(id+"F4.wireOp",EDGE,"E30"),sQuery(id+"F4.wireOp",EDGE,"E31"),sQuery(id+"F4.wireOp",EDGE,"E32"),sQuery(id+"F4.wireOp",EDGE,"E33"),sQuery(id+"F4.wireOp",EDGE,"E34"),sQuery(id+"F4.wireOp",EDGE,"E35"),sQuery(id+"F4.wireOp",EDGE,"E36"),sQuery(id+"F4.wireOp",EDGE,"E37"),sQuery(id+"F4.wireOp",EDGE,"E38"),sQuery(id+"F4.wireOp",EDGE,"E39"),sQuery(id+"F4.wireOp",EDGE,"E40"),sQuery(id+"F4.wireOp",EDGE,"E41"),sQuery(id+"F4.wireOp",EDGE,"E42"),sQuery(id+"F4.wireOp",EDGE,"E43"),sQuery(id+"F4.wireOp",EDGE,"E44"),sQuery(id+"F4.wireOp",EDGE,"E45"),sQuery(id+"F4.wireOp",EDGE,"E46"),sQuery(id+"F4.wireOp",EDGE,"E47"),sQuery(id+"F4.wireOp",EDGE,"E48"),sQuery(id+"F4.wireOp",EDGE,"E49"),sQuery(id+"F4.wireOp",EDGE,"E50"),sQuery(id+"F4.wireOp",EDGE,"E51"),sQuery(id+"F4.wireOp",EDGE,"E52"),sQuery(id+"F4.wireOp",EDGE,"E53"),sQuery(id+"F4.wireOp",EDGE,"E54"),sQuery(id+"F4.wireOp",EDGE,"E55"),sQuery(id+"F4.wireOp",EDGE,"E56"),sQuery(id+"F4.wireOp",EDGE,"E57"),sQuery(id+"F4.wireOp",EDGE,"E58"),sQuery(id+"F4.wireOp",EDGE,"E59"),sQuery(id+"F4.wireOp",EDGE,"E60"),sQuery(id+"F4.wireOp",EDGE,"E61"),sQuery(id+"F4.wireOp",EDGE,"E62"),sQuery(id+"F4.wireOp",EDGE,"E63"),sQuery(id+"F4.wireOp",EDGE,"E64"),sQuery(id+"F4.wireOp",EDGE,"E65"),sQuery(id+"F4.wireOp",EDGE,"E66"),sQuery(id+"F4.wireOp",EDGE,"E67"),sQuery(id+"F4.wireOp",EDGE,"E68"),sQuery(id+"F4.wireOp",EDGE,"E69"),sQuery(id+"F4.wireOp",EDGE,"E70"),sQuery(id+"F4.wireOp",EDGE,"E71"),sQuery(id+"F4.wireOp",EDGE,"E72"),sQuery(id+"F4.wireOp",EDGE,"E73"),sQuery(id+"F4.wireOp",EDGE,"E74"),sQuery(id+"F4.wireOp",EDGE,"E75"),sQuery(id+"F4.wireOp",EDGE,"E76"),sQuery(id+"F4.wireOp",EDGE,"E77"),sQuery(id+"F4.wireOp",EDGE,"E78"),sQuery(id+"F4.wireOp",EDGE,"E79"),sQuery(id+"F4.wireOp",EDGE,"E80"),sQuery(id+"F4.wireOp",EDGE,"E81"),sQuery(id+"F4.wireOp",EDGE,"E82"),sQuery(id+"F4.wireOp",EDGE,"E83"),sQuery(id+"F4.wireOp",EDGE,"E84"),sQuery(id+"F4.wireOp",EDGE,"E85"),sQuery(id+"F4.wireOp",EDGE,"E86"),sQuery(id+"F4.wireOp",EDGE,"E87"),sQuery(id+"F4.wireOp",EDGE,"E88"),sQuery(id+"F4.wireOp",EDGE,"E89"),sQuery(id+"F4.wireOp",EDGE,"E90"),sQuery(id+"F4.wireOp",EDGE,"E91"),sQuery(id+"F4.wireOp",EDGE,"E92"),sQuery(id+"F4.wireOp",EDGE,"E93"),sQuery(id+"F4.wireOp",EDGE,"E94"),sQuery(id+"F4.wireOp",EDGE,"E95"),sQuery(id+"F4.wireOp",EDGE,"E96"),sQuery(id+"F4.wireOp",EDGE,"E97"),sQuery(id+"F4.wireOp",EDGE,"E98"),sQuery(id+"F4.wireOp",EDGE,"E99"),sQuery(id+"F4.wireOp",EDGE,"E100"),sQuery(id+"F4.wireOp",EDGE,"E101"),sQuery(id+"F4.wireOp",EDGE,"E102"),sQuery(id+"F4.wireOp",EDGE,"E103"),sQuery(id+"F4.wireOp",EDGE,"E104"),sQuery(id+"F4.wireOp",EDGE,"E105"),sQuery(id+"F4.wireOp",EDGE,"E106"),sQuery(id+"F4.wireOp",EDGE,"E107"),sQuery(id+"F4.wireOp",EDGE,"E108"),sQuery(id+"F4.wireOp",EDGE,"E109"),sQuery(id+"F4.wireOp",EDGE,"E110"),sQuery(id+"F4.wireOp",EDGE,"E111"),sQuery(id+"F4.wireOp",EDGE,"E112"),sQuery(id+"F4.wireOp",EDGE,"E113"),sQuery(id+"F4.wireOp",EDGE,"E114"),sQuery(id+"F4.wireOp",EDGE,"E115"),sQuery(id+"F4.wireOp",EDGE,"E116"),sQuery(id+"F4.wireOp",EDGE,"E117"),sQuery(id+"F4.wireOp",EDGE,"E118"),sQuery(id+"F4.wireOp",EDGE,"E119"),sQuery(id+"F4.wireOp",EDGE,"E120"),sQuery(id+"F4.wireOp",EDGE,"E121"),sQuery(id+"F4.wireOp",EDGE,"E122"),sQuery(id+"F4.wireOp",EDGE,"E123"),sQuery(id+"F4.wireOp",EDGE,"E124"),sQuery(id+"F4.wireOp",EDGE,"E125"),sQuery(id+"F4.wireOp",EDGE,"E126"),sQuery(id+"F4.wireOp",EDGE,"E127"),sQuery(id+"F4.wireOp",EDGE,"E128"),sQuery(id+"F4.wireOp",EDGE,"E129"),sQuery(id+"F4.wireOp",EDGE,"E130"),sQuery(id+"F4.wireOp",EDGE,"E131"),sQuery(id+"F4.wireOp",EDGE,"E132"),sQuery(id+"F4.wireOp",EDGE,"E133"),sQuery(id+"F4.wireOp",EDGE,"E134"),sQuery(id+"F4.wireOp",EDGE,"E135"),sQuery(id+"F4.wireOp",EDGE,"E136"),sQuery(id+"F4.wireOp",EDGE,"E137"),sQuery(id+"F4.wireOp",EDGE,"E138"),sQuery(id+"F4.wireOp",EDGE,"E139"),sQuery(id+"F4.wireOp",EDGE,"E140"),sQuery(id+"F4.wireOp",EDGE,"E141"),sQuery(id+"F4.wireOp",EDGE,"E142"),sQuery(id+"F4.wireOp",EDGE,"E143"),sQuery(id+"F4.wireOp",EDGE,"E144"),sQuery(id+"F4.wireOp",EDGE,"E145"),sQuery(id+"F4.wireOp",EDGE,"E146"),sQuery(id+"F4.wireOp",EDGE,"E147"),sQuery(id+"F4.wireOp",EDGE,"E148"),sQuery(id+"F4.wireOp",EDGE,"E149"),sQuery(id+"F4.wireOp",EDGE,"E150"),sQuery(id+"F4.wireOp",EDGE,"E151"),sQuery(id+"F4.wireOp",EDGE,"E152"),sQuery(id+"F4.wireOp",EDGE,"E153"),sQuery(id+"F4.wireOp",EDGE,"E154"),sQuery(id+"F4.wireOp",EDGE,"E155"),sQuery(id+"F4.wireOp",EDGE,"E156"),sQuery(id+"F4.wireOp",EDGE,"E157"),sQuery(id+"F4.wireOp",EDGE,"E158"),sQuery(id+"F4.wireOp",EDGE,"E159"),sQuery(id+"F4.wireOp",EDGE,"E160"),sQuery(id+"F4.wireOp",EDGE,"E161"),sQuery(id+"F4.wireOp",EDGE,"E162"),sQuery(id+"F4.wireOp",EDGE,"E163"),sQuery(id+"F4.wireOp",EDGE,"E164"),sQuery(id+"F4.wireOp",EDGE,"E165"),sQuery(id+"F4.wireOp",EDGE,"E166"),sQuery(id+"F4.wireOp",EDGE,"E167"),sQuery(id+"F4.wireOp",EDGE,"E168"),sQuery(id+"F4.wireOp",EDGE,"E169"),sQuery(id+"F4.wireOp",EDGE,"E170"),sQuery(id+"F4.wireOp",EDGE,"E171"),sQuery(id+"F4.wireOp",EDGE,"E172"),sQuery(id+"F4.wireOp",EDGE,"E173"),sQuery(id+"F4.wireOp",EDGE,"E174"),sQuery(id+"F4.wireOp",EDGE,"E175"),sQuery(id+"F4.wireOp",EDGE,"E176"),sQuery(id+"F4.wireOp",EDGE,"E177"),sQuery(id+"F4.wireOp",EDGE,"E178"),sQuery(id+"F4.wireOp",EDGE,"E179"),sQuery(id+"F4.wireOp",EDGE,"E180"),sQuery(id+"F4.wireOp",EDGE,"E181"),sQuery(id+"F4.wireOp",EDGE,"E182"),sQuery(id+"F4.wireOp",EDGE,"E183"),sQuery(id+"F4.wireOp",EDGE,"E184"),sQuery(id+"F4.wireOp",EDGE,"E185"),sQuery(id+"F4.wireOp",EDGE,"E186"),sQuery(id+"F4.wireOp",EDGE,"E187"),sQuery(id+"F4.wireOp",EDGE,"E188"),sQuery(id+"F4.wireOp",EDGE,"E189"),sQuery(id+"F4.wireOp",EDGE,"E190"),sQuery(id+"F4.wireOp",EDGE,"E191"),sQuery(id+"F4.wireOp",EDGE,"E192"),sQuery(id+"F4.wireOp",EDGE,"E193"),sQuery(id+"F4.wireOp",EDGE,"E194"),sQuery(id+"F4.wireOp",EDGE,"E195"),sQuery(id+"F4.wireOp",EDGE,"E196"),sQuery(id+"F4.wireOp",EDGE,"E197"),sQuery(id+"F4.wireOp",EDGE,"E198"),sQuery(id+"F4.wireOp",EDGE,"E199"),sQuery(id+"F4.wireOp",EDGE,"E200"),sQuery(id+"F4.wireOp",EDGE,"E201"),sQuery(id+"F4.wireOp",EDGE,"E202"),sQuery(id+"F4.wireOp",EDGE,"E203"),sQuery(id+"F4.wireOp",EDGE,"E204"),sQuery(id+"F4.wireOp",EDGE,"E205"),sQuery(id+"F4.wireOp",EDGE,"E206"),sQuery(id+"F4.wireOp",EDGE,"E207"),sQuery(id+"F4.wireOp",EDGE,"E208"),sQuery(id+"F4.wireOp",EDGE,"E209"),sQuery(id+"F4.wireOp",EDGE,"E210"),sQuery(id+"F4.wireOp",EDGE,"E211"),sQuery(id+"F4.wireOp",EDGE,"E212"),sQuery(id+"F4.wireOp",EDGE,"E213"),sQuery(id+"F4.wireOp",EDGE,"E214"),sQuery(id+"F4.wireOp",EDGE,"E215"),sQuery(id+"F4.wireOp",EDGE,"E216"),sQuery(id+"F4.wireOp",EDGE,"E217"),sQuery(id+"F4.wireOp",EDGE,"E218"),sQuery(id+"F4.wireOp",EDGE,"E220"),sQuery(id+"F4.wireOp",EDGE,"E221"),sQuery(id+"F4.wireOp",EDGE,"E222"),sQuery(id+"F4.wireOp",EDGE,"E223"),sQuery(id+"F4.wireOp",EDGE,"E224"),sQuery(id+"F4.wireOp",EDGE,"E225"),sQuery(id+"F4.wireOp",EDGE,"E226"),sQuery(id+"F4.wireOp",EDGE,"E227"),sQuery(id+"F4.wireOp",EDGE,"E228"),sQuery(id+"F4.wireOp",EDGE,"E229"),sQuery(id+"F4.wireOp",EDGE,"E230"),sQuery(id+"F4.wireOp",EDGE,"E231"),sQuery(id+"F4.wireOp",EDGE,"E232"),sQuery(id+"F4.wireOp",EDGE,"E233"),sQuery(id+"F4.wireOp",EDGE,"E234"),sQuery(id+"F4.wireOp",EDGE,"E235"),sQuery(id+"F4.wireOp",EDGE,"E236"),sQuery(id+"F4.wireOp",EDGE,"E237"),sQuery(id+"F4.wireOp",EDGE,"E238"),sQuery(id+"F4.wireOp",EDGE,"E239"),sQuery(id+"F4.wireOp",EDGE,"E240"),sQuery(id+"F4.wireOp",EDGE,"E241"),sQuery(id+"F4.wireOp",EDGE,"E242"),sQuery(id+"F4.wireOp",EDGE,"E243"),sQuery(id+"F4.wireOp",EDGE,"E244"),sQuery(id+"F4.wireOp",EDGE,"E245"),sQuery(id+"F4.wireOp",EDGE,"E246"),sQuery(id+"F4.wireOp",EDGE,"E247"),sQuery(id+"F4.wireOp",EDGE,"E248"),sQuery(id+"F4.wireOp",EDGE,"E249"),sQuery(id+"F4.wireOp",EDGE,"E250"),sQuery(id+"F4.wireOp",EDGE,"E251"),sQuery(id+"F4.wireOp",EDGE,"E252"),sQuery(id+"F4.wireOp",EDGE,"E253"),sQuery(id+"F4.wireOp",EDGE,"E254"),sQuery(id+"F4.wireOp",EDGE,"E255"),sQuery(id+"F4.wireOp",EDGE,"E256"),sQuery(id+"F4.wireOp",EDGE,"E257"),sQuery(id+"F4.wireOp",EDGE,"E258"),sQuery(id+"F4.wireOp",EDGE,"E259"),sQuery(id+"F4.wireOp",EDGE,"E260"),sQuery(id+"F4.wireOp",EDGE,"E261"),sQuery(id+"F4.wireOp",EDGE,"E262"),sQuery(id+"F4.wireOp",EDGE,"E263"),sQuery(id+"F4.wireOp",EDGE,"E264"),sQuery(id+"F4.wireOp",EDGE,"E265"),sQuery(id+"F4.wireOp",EDGE,"E266"),sQuery(id+"F4.wireOp",EDGE,"E267"),sQuery(id+"F4.wireOp",EDGE,"E268"),sQuery(id+"F4.wireOp",EDGE,"E269"),sQuery(id+"F4.wireOp",EDGE,"E270"),sQuery(id+"F4.wireOp",EDGE,"E271"),sQuery(id+"F4.wireOp",EDGE,"E272"),sQuery(id+"F4.wireOp",EDGE,"E273"),sQuery(id+"F4.wireOp",EDGE,"E274"),sQuery(id+"F4.wireOp",EDGE,"E275"),sQuery(id+"F4.wireOp",EDGE,"E276"),sQuery(id+"F4.wireOp",EDGE,"E277"),sQuery(id+"F4.wireOp",EDGE,"E278"),sQuery(id+"F4.wireOp",EDGE,"E279"),sQuery(id+"F4.wireOp",EDGE,"E280"),sQuery(id+"F4.wireOp",EDGE,"E281"),sQuery(id+"F4.wireOp",EDGE,"E282"),sQuery(id+"F4.wireOp",EDGE,"E283"),sQuery(id+"F4.wireOp",EDGE,"E284"),sQuery(id+"F4.wireOp",EDGE,"E285"),sQuery(id+"F4.wireOp",EDGE,"E286"),sQuery(id+"F4.wireOp",EDGE,"E287"),sQuery(id+"F4.wireOp",EDGE,"E288"),sQuery(id+"F4.wireOp",EDGE,"E289"),sQuery(id+"F4.wireOp",EDGE,"E290"),sQuery(id+"F4.wireOp",EDGE,"E291"),sQuery(id+"F4.wireOp",EDGE,"E292"),sQuery(id+"F4.wireOp",EDGE,"E302"),sQuery(id+"F4.wireOp",EDGE,"E303"),sQuery(id+"F4.wireOp",EDGE,"E304"),sQuery(id+"F4.wireOp",EDGE,"E305"),sQuery(id+"F4.wireOp",EDGE,"E306"),sQuery(id+"F4.wireOp",EDGE,"E307"),sQuery(id+"F4.wireOp",EDGE,"E308"),sQuery(id+"F4.wireOp",EDGE,"E309"),sQuery(id+"F4.wireOp",EDGE,"E310"),sQuery(id+"F4.wireOp",EDGE,"E311"),sQuery(id+"F4.wireOp",EDGE,"E312"),sQuery(id+"F4.wireOp",EDGE,"E313"),sQuery(id+"F4.wireOp",EDGE,"E314"),sQuery(id+"F4.wireOp",EDGE,"E315"),sQuery(id+"F4.wireOp",EDGE,"E316"),sQuery(id+"F4.wireOp",EDGE,"E317"),sQuery(id+"F4.wireOp",EDGE,"E318"),sQuery(id+"F4.wireOp",EDGE,"E319"),sQuery(id+"F4.wireOp",EDGE,"E320"),sQuery(id+"F4.wireOp",EDGE,"E321"),sQuery(id+"F4.wireOp",EDGE,"E322"),sQuery(id+"F4.wireOp",EDGE,"E323"),sQuery(id+"F4.wireOp",EDGE,"E324"),sQuery(id+"F4.wireOp",EDGE,"E325"),sQuery(id+"F4.wireOp",EDGE,"E326"),sQuery(id+"F4.wireOp",EDGE,"E327"),sQuery(id+"F4.wireOp",EDGE,"E328"),sQuery(id+"F4.wireOp",EDGE,"E329"),sQuery(id+"F4.wireOp",EDGE,"E330"),sQuery(id+"F4.wireOp",EDGE,"E331"),sQuery(id+"F4.wireOp",EDGE,"E332"),sQuery(id+"F4.wireOp",EDGE,"E333"),sQuery(id+"F4.wireOp",EDGE,"E334"),sQuery(id+"F4.wireOp",EDGE,"E335"),sQuery(id+"F4.wireOp",EDGE,"E336"),sQuery(id+"F4.wireOp",EDGE,"E337"),sQuery(id+"F4.wireOp",EDGE,"E338"),sQuery(id+"F4.wireOp",EDGE,"E339"),sQuery(id+"F4.wireOp",EDGE,"E340"),sQuery(id+"F4.wireOp",EDGE,"E341"),sQuery(id+"F4.wireOp",EDGE,"E342"),sQuery(id+"F4.wireOp",EDGE,"E343"),sQuery(id+"F4.wireOp",EDGE,"E344"),sQuery(id+"F4.wireOp",EDGE,"E345"),sQuery(id+"F4.wireOp",EDGE,"E346"),sQuery(id+"F4.wireOp",EDGE,"E347"),sQuery(id+"F4.wireOp",EDGE,"E348"),sQuery(id+"F4.wireOp",EDGE,"E349"),sQuery(id+"F4.wireOp",EDGE,"E350"),sQuery(id+"F4.wireOp",EDGE,"E351"),sQuery(id+"F4.wireOp",EDGE,"E352"),sQuery(id+"F4.wireOp",EDGE,"E353"),sQuery(id+"F4.wireOp",EDGE,"E354"),sQuery(id+"F4.wireOp",EDGE,"E355"),sQuery(id+"F4.wireOp",EDGE,"E356"),sQuery(id+"F4.wireOp",EDGE,"E357"),sQuery(id+"F4.wireOp",EDGE,"E358"),sQuery(id+"F4.wireOp",EDGE,"E359"),sQuery(id+"F4.wireOp",EDGE,"E360"),sQuery(id+"F4.wireOp",EDGE,"E361"),sQuery(id+"F4.wireOp",EDGE,"E362"),sQuery(id+"F4.wireOp",EDGE,"E363"),sQuery(id+"F4.wireOp",EDGE,"E364"),sQuery(id+"F4.wireOp",EDGE,"E365"),sQuery(id+"F4.wireOp",EDGE,"E366"),sQuery(id+"F4.wireOp",EDGE,"E367"),sQuery(id+"F4.wireOp",EDGE,"E368"),sQuery(id+"F4.wireOp",EDGE,"E369"),sQuery(id+"F4.wireOp",EDGE,"E370"),sQuery(id+"F4.wireOp",EDGE,"E371"),sQuery(id+"F4.wireOp",EDGE,"E372"),sQuery(id+"F4.wireOp",EDGE,"E373"),sQuery(id+"F4.wireOp",EDGE,"E374"),sQuery(id+"F4.wireOp",EDGE,"E375"),sQuery(id+"F4.wireOp",EDGE,"E376"),sQuery(id+"F4.wireOp",EDGE,"E377"),sQuery(id+"F4.wireOp",EDGE,"E378"),sQuery(id+"F4.wireOp",EDGE,"E379"),sQuery(id+"F4.wireOp",EDGE,"E380"),sQuery(id+"F4.wireOp",EDGE,"E381"),sQuery(id+"F4.wireOp",EDGE,"E382"),sQuery(id+"F4.wireOp",EDGE,"E383"),sQuery(id+"F4.wireOp",EDGE,"E384"),sQuery(id+"F4.wireOp",EDGE,"E385"),sQuery(id+"F4.wireOp",EDGE,"E386"),sQuery(id+"F4.wireOp",EDGE,"E387"),sQuery(id+"F4.wireOp",EDGE,"E388"),sQuery(id+"F4.wireOp",EDGE,"E389"),sQuery(id+"F4.wireOp",EDGE,"E390"),sQuery(id+"F4.wireOp",EDGE,"E391"),sQuery(id+"F4.wireOp",EDGE,"E392"),sQuery(id+"F4.wireOp",EDGE,"E393"),sQuery(id+"F4.wireOp",EDGE,"E394"),sQuery(id+"F4.wireOp",EDGE,"E395"),sQuery(id+"F4.wireOp",EDGE,"E396"),sQuery(id+"F4.wireOp",EDGE,"E397"),sQuery(id+"F4.wireOp",EDGE,"E398"),sQuery(id+"F4.wireOp",EDGE,"E399"),sQuery(id+"F4.wireOp",EDGE,"E400"),sQuery(id+"F4.wireOp",EDGE,"E401"),sQuery(id+"F4.wireOp",EDGE,"E402"),sQuery(id+"F4.wireOp",EDGE,"E403"),sQuery(id+"F4.wireOp",EDGE,"E404"),sQuery(id+"F4.wireOp",EDGE,"E405"),sQuery(id+"F4.wireOp",EDGE,"E406"),sQuery(id+"F4.wireOp",EDGE,"E407"),sQuery(id+"F4.wireOp",EDGE,"E408"),sQuery(id+"F4.wireOp",EDGE,"E409"),sQuery(id+"F4.wireOp",EDGE,"E410"),sQuery(id+"F4.wireOp",EDGE,"E411"),sQuery(id+"F4.wireOp",EDGE,"E412"),sQuery(id+"F4.wireOp",EDGE,"E413"),sQuery(id+"F4.wireOp",EDGE,"E414"),sQuery(id+"F4.wireOp",EDGE,"E415"),sQuery(id+"F4.wireOp",EDGE,"E416"),sQuery(id+"F4.wireOp",EDGE,"E417"),sQuery(id+"F4.wireOp",EDGE,"E418"),sQuery(id+"F4.wireOp",EDGE,"E419"),sQuery(id+"F4.wireOp",EDGE,"E420"),sQuery(id+"F4.wireOp",EDGE,"E421"),sQuery(id+"F4.wireOp",EDGE,"E422"),sQuery(id+"F4.wireOp",EDGE,"E423"),sQuery(id+"F4.wireOp",EDGE,"E424"),sQuery(id+"F4.wireOp",EDGE,"E425"),sQuery(id+"F4.wireOp",EDGE,"E426"),sQuery(id+"F4.wireOp",EDGE,"E427")])],"isStart":false});
            var sketch = newSketch(context, id + "F6", { "sketchPlane" : qUnion([Q0])});
            skLineSegment(sketch, "E428", {"start": v(30.52, 6.52) * mm, "end": v(30.5, 6.38) * mm});
            skLineSegment(sketch, "E429", {"start": v(30.5, 6.38) * mm, "end": v(30.48, 6.17) * mm});
            skLineSegment(sketch, "E430", {"start": v(30.48, 6.17) * mm, "end": v(30.47, 5.98) * mm});
            skLineSegment(sketch, "E431", {"start": v(30.47, 5.98) * mm, "end": v(30.5, 5.77) * mm});
            skLineSegment(sketch, "E432", {"start": v(30.5, 5.77) * mm, "end": v(30.54, 5.56) * mm});
            skLineSegment(sketch, "E433", {"start": v(30.54, 5.56) * mm, "end": v(30.63, 5.32) * mm});
            skLineSegment(sketch, "E434", {"start": v(30.63, 5.32) * mm, "end": v(30.76, 5.08) * mm});
            skLineSegment(sketch, "E435", {"start": v(30.76, 5.08) * mm, "end": v(30.92, 4.9) * mm});
            skLineSegment(sketch, "E436", {"start": v(30.92, 4.9) * mm, "end": v(31.07, 4.74) * mm});
            skLineSegment(sketch, "E437", {"start": v(31.07, 4.74) * mm, "end": v(31.12, 4.65) * mm});
            skLineSegment(sketch, "E438", {"start": v(31.12, 4.65) * mm, "end": v(31.1, 4.35) * mm});
            skLineSegment(sketch, "E439", {"start": v(31.1, 4.35) * mm, "end": v(31.07, 3.9) * mm});
            skLineSegment(sketch, "E440", {"start": v(31.07, 3.9) * mm, "end": v(31, 3.37) * mm});
            skLineSegment(sketch, "E441", {"start": v(31, 3.37) * mm, "end": v(30.95, 3.05) * mm});
            skLineSegment(sketch, "E442", {"start": v(30.95, 3.05) * mm, "end": v(30.9, 2.55) * mm});
            skLineSegment(sketch, "E443", {"start": v(30.9, 2.55) * mm, "end": v(30.84, 2.04) * mm});
            skLineSegment(sketch, "E444", {"start": v(30.84, 2.04) * mm, "end": v(30.8, 1.45) * mm});
            skLineSegment(sketch, "E445", {"start": v(30.8, 1.45) * mm, "end": v(30.76, 0.92) * mm});
            skLineSegment(sketch, "E446", {"start": v(30.76, 0.92) * mm, "end": v(30.72, 0.17) * mm});
            skLineSegment(sketch, "E447", {"start": v(30.72, 0.17) * mm, "end": v(30.7, -0.73) * mm});
            skLineSegment(sketch, "E448", {"start": v(30.7, -0.73) * mm, "end": v(30.7, -0.96) * mm});
            skLineSegment(sketch, "E449", {"start": v(30.7, -0.96) * mm, "end": v(30.67, -1.11) * mm});
            skLineSegment(sketch, "E450", {"start": v(30.67, -1.11) * mm, "end": v(30.57, -1.22) * mm});
            skLineSegment(sketch, "E451", {"start": v(30.57, -1.22) * mm, "end": v(30.38, -1.28) * mm});
            skLineSegment(sketch, "E452", {"start": v(30.38, -1.28) * mm, "end": v(30.12, -1.23) * mm});
            skLineSegment(sketch, "E453", {"start": v(30.12, -1.23) * mm, "end": v(29.89, -1.14) * mm});
            skLineSegment(sketch, "E454", {"start": v(29.89, -1.14) * mm, "end": v(29.6, -0.98) * mm});
            skLineSegment(sketch, "E455", {"start": v(29.6, -0.98) * mm, "end": v(29.22, -0.81) * mm});
            skLineSegment(sketch, "E456", {"start": v(29.22, -0.81) * mm, "end": v(29.1, -0.75) * mm});
            skLineSegment(sketch, "E457", {"start": v(29.73, -3.8) * mm, "end": v(30.17, -3.9) * mm});
            skLineSegment(sketch, "E458", {"start": v(30.17, -3.9) * mm, "end": v(30.61, -4.05) * mm});
            skLineSegment(sketch, "E459", {"start": v(30.61, -4.05) * mm, "end": v(31.26, -4.2) * mm});
            skLineSegment(sketch, "E460", {"start": v(31.26, -4.2) * mm, "end": v(31.9, -4.27) * mm});
            skLineSegment(sketch, "E461", {"start": v(31.9, -4.27) * mm, "end": v(32.46, -4.32) * mm});
            skLineSegment(sketch, "E462", {"start": v(32.46, -4.32) * mm, "end": v(33.2, -4.35) * mm});
            skLineSegment(sketch, "E463", {"start": v(33.2, -4.35) * mm, "end": v(33.76, -4.36) * mm});
            skLineSegment(sketch, "E464", {"start": v(33.76, -4.36) * mm, "end": v(34.47, -4.3) * mm});
            skLineSegment(sketch, "E465", {"start": v(34.47, -4.3) * mm, "end": v(35.12, -4.19) * mm});
            skLineSegment(sketch, "E466", {"start": v(35.12, -4.19) * mm, "end": v(35.7, -4.09) * mm});
            skLineSegment(sketch, "E467", {"start": v(35.7, -4.09) * mm, "end": v(36.38, -3.9) * mm});
            skLineSegment(sketch, "E468", {"start": v(36.38, -3.9) * mm, "end": v(36.63, -3.8) * mm});
            skLineSegment(sketch, "E469", {"start": v(36.63, -3.8) * mm, "end": v(36.7, -3.7) * mm});
            skLineSegment(sketch, "E470", {"start": v(36.7, -3.7) * mm, "end": v(36.65, -3.4) * mm});
            skLineSegment(sketch, "E471", {"start": v(36.65, -3.4) * mm, "end": v(36.58, -2.9) * mm});
            skLineSegment(sketch, "E472", {"start": v(36.58, -2.9) * mm, "end": v(36.5, -2.1) * mm});
            skLineSegment(sketch, "E473", {"start": v(36.5, -2.1) * mm, "end": v(36.48, -1.32) * mm});
            skLineSegment(sketch, "E474", {"start": v(36.48, -1.32) * mm, "end": v(36.42, -1.18) * mm});
            skLineSegment(sketch, "E475", {"start": v(36.42, -1.18) * mm, "end": v(36.3, -1.13) * mm});
            skLineSegment(sketch, "E476", {"start": v(36.3, -1.13) * mm, "end": v(36.09, -1.19) * mm});
            skLineSegment(sketch, "E477", {"start": v(36.09, -1.19) * mm, "end": v(35.75, -1.24) * mm});
            skLineSegment(sketch, "E478", {"start": v(35.75, -1.24) * mm, "end": v(35.32, -1.37) * mm});
            skLineSegment(sketch, "E479", {"start": v(35.32, -1.37) * mm, "end": v(35.02, -1.45) * mm});
            skLineSegment(sketch, "E480", {"start": v(35.02, -1.45) * mm, "end": v(34.6, -1.5) * mm});
            skLineSegment(sketch, "E481", {"start": v(34.6, -1.5) * mm, "end": v(34.15, -1.59) * mm});
            skLineSegment(sketch, "E482", {"start": v(34.15, -1.59) * mm, "end": v(33.48, -1.63) * mm});
            skLineSegment(sketch, "E483", {"start": v(33.48, -1.63) * mm, "end": v(33.04, -1.63) * mm});
            skLineSegment(sketch, "E484", {"start": v(33.04, -1.63) * mm, "end": v(32.87, -1.39) * mm});
            skLineSegment(sketch, "E485", {"start": v(32.87, -1.39) * mm, "end": v(32.7, -0.95) * mm});
            skLineSegment(sketch, "E486", {"start": v(32.7, -0.95) * mm, "end": v(32.72, -0.23) * mm});
            skLineSegment(sketch, "E487", {"start": v(32.72, -0.23) * mm, "end": v(32.75, 0.35) * mm});
            skLineSegment(sketch, "E488", {"start": v(32.75, 0.35) * mm, "end": v(32.77, 0.8) * mm});
            skLineSegment(sketch, "E489", {"start": v(32.77, 0.8) * mm, "end": v(32.82, 1.46) * mm});
            skLineSegment(sketch, "E490", {"start": v(32.82, 1.46) * mm, "end": v(32.88, 2.38) * mm});
            skLineSegment(sketch, "E491", {"start": v(32.88, 2.38) * mm, "end": v(32.95, 3.23) * mm});
            skLineSegment(sketch, "E492", {"start": v(32.95, 3.23) * mm, "end": v(33.03, 3.81) * mm});
            skLineSegment(sketch, "E493", {"start": v(33.03, 3.81) * mm, "end": v(33.17, 4.05) * mm});
            skLineSegment(sketch, "E494", {"start": v(33.17, 4.05) * mm, "end": v(33.53, 4.2) * mm});
            skLineSegment(sketch, "E495", {"start": v(33.53, 4.2) * mm, "end": v(34.12, 4.38) * mm});
            skLineSegment(sketch, "E496", {"start": v(34.12, 4.38) * mm, "end": v(34.55, 4.67) * mm});
            skLineSegment(sketch, "E497", {"start": v(34.55, 4.67) * mm, "end": v(35.01, 4.97) * mm});
            skLineSegment(sketch, "E498", {"start": v(35.01, 4.97) * mm, "end": v(35.36, 5.3) * mm});
            skLineSegment(sketch, "E499", {"start": v(35.36, 5.3) * mm, "end": v(35.7, 5.68) * mm});
            skLineSegment(sketch, "E500", {"start": v(35.7, 5.68) * mm, "end": v(35.9, 6.17) * mm});
            skLineSegment(sketch, "E501", {"start": v(35.9, 6.17) * mm, "end": v(35.93, 6.47) * mm});
            skLineSegment(sketch, "E502", {"start": v(35.93, 6.47) * mm, "end": v(35.94, 6.69) * mm});
            skLineSegment(sketch, "E503", {"start": v(35.94, 6.69) * mm, "end": v(35.76, 6.82) * mm});
            skLineSegment(sketch, "E504", {"start": v(35.76, 6.82) * mm, "end": v(35.46, 6.96) * mm});
            skLineSegment(sketch, "E505", {"start": v(35.46, 6.96) * mm, "end": v(35.2, 7.07) * mm});
            skLineSegment(sketch, "E506", {"start": v(35.2, 7.07) * mm, "end": v(35.06, 7.14) * mm});
            skLineSegment(sketch, "E507", {"start": v(35.06, 7.14) * mm, "end": v(34.9, 7.17) * mm});
            skLineSegment(sketch, "E508", {"start": v(34.9, 7.17) * mm, "end": v(34.75, 7) * mm});
            skLineSegment(sketch, "E509", {"start": v(34.75, 7) * mm, "end": v(34.7, 6.73) * mm});
            skLineSegment(sketch, "E510", {"start": v(34.7, 6.73) * mm, "end": v(34.6, 6.44) * mm});
            skLineSegment(sketch, "E511", {"start": v(34.6, 6.44) * mm, "end": v(34.47, 6.18) * mm});
            skLineSegment(sketch, "E512", {"start": v(34.47, 6.18) * mm, "end": v(34.31, 5.99) * mm});
            skLineSegment(sketch, "E513", {"start": v(34.31, 5.99) * mm, "end": v(34.12, 5.79) * mm});
            skLineSegment(sketch, "E514", {"start": v(34.12, 5.79) * mm, "end": v(33.88, 5.66) * mm});
            skLineSegment(sketch, "E515", {"start": v(33.88, 5.66) * mm, "end": v(33.58, 5.53) * mm});
            skLineSegment(sketch, "E516", {"start": v(33.58, 5.53) * mm, "end": v(33.2, 5.44) * mm});
            skLineSegment(sketch, "E517", {"start": v(33.2, 5.44) * mm, "end": v(32.79, 5.4) * mm});
            skLineSegment(sketch, "E518", {"start": v(32.79, 5.4) * mm, "end": v(32.36, 5.47) * mm});
            skLineSegment(sketch, "E519", {"start": v(32.36, 5.47) * mm, "end": v(32.12, 5.58) * mm});
            skLineSegment(sketch, "E520", {"start": v(32.12, 5.58) * mm, "end": v(31.88, 5.7) * mm});
            skLineSegment(sketch, "E521", {"start": v(30.53, 6.6) * mm, "end": v(30.52, 6.52) * mm});
            skLineSegment(sketch, "E522", {"start": v(31.88, 5.7) * mm, "end": v(31.72, 5.78) * mm});
            skLineSegment(sketch, "E523", {"start": v(31.72, 5.78) * mm, "end": v(31.55, 5.89) * mm});
            skLineSegment(sketch, "E524", {"start": v(31.55, 5.89) * mm, "end": v(31.4, 6) * mm});
            skLineSegment(sketch, "E525", {"start": v(31.4, 6) * mm, "end": v(31.26, 6.11) * mm});
            skLineSegment(sketch, "E526", {"start": v(31.26, 6.11) * mm, "end": v(31.05, 6.25) * mm});
            skLineSegment(sketch, "E527", {"start": v(31.05, 6.25) * mm, "end": v(30.94, 6.33) * mm});
            skLineSegment(sketch, "E528", {"start": v(30.94, 6.33) * mm, "end": v(30.78, 6.42) * mm});
            skLineSegment(sketch, "E529", {"start": v(30.78, 6.42) * mm, "end": v(30.67, 6.48) * mm});
            skLineSegment(sketch, "E530", {"start": v(30.67, 6.48) * mm, "end": v(30.6, 6.54) * mm});
            skLineSegment(sketch, "E531", {"start": v(30.6, 6.54) * mm, "end": v(30.53, 6.6) * mm});
            skLineSegment(sketch, "E532", {"start": v(29.1, -0.75) * mm, "end": v(28.89, -0.78) * mm});
            skLineSegment(sketch, "E533", {"start": v(29.15, -3.44) * mm, "end": v(29.32, -3.68) * mm});
            skLineSegment(sketch, "E534", {"start": v(29.32, -3.68) * mm, "end": v(29.73, -3.8) * mm});
            skLineSegment(sketch, "E535", {"start": v(28.89, -0.78) * mm, "end": v(28.9, -1.07) * mm});
            skLineSegment(sketch, "E536", {"start": v(28.9, -1.07) * mm, "end": v(28.9, -1.4) * mm});
            skLineSegment(sketch, "E537", {"start": v(28.9, -1.4) * mm, "end": v(28.93, -1.86) * mm});
            skLineSegment(sketch, "E538", {"start": v(28.93, -1.86) * mm, "end": v(28.97, -2.21) * mm});
            skLineSegment(sketch, "E539", {"start": v(28.97, -2.21) * mm, "end": v(29.04, -2.82) * mm});
            skLineSegment(sketch, "E540", {"start": v(29.04, -2.82) * mm, "end": v(29.1, -3.34) * mm});
            skLineSegment(sketch, "E541", {"start": v(29.1, -3.34) * mm, "end": v(29.15, -3.44) * mm});
            skSolve(sketch);
        }
        {
            var Q0;
            Q0 = qSketchRegion(id + "F6", true);
            extrude(context, id + "F7", {"entities" : qUnion([Q0]), "operationType" : NewBodyOperationType.REMOVE, "oppositeDirection" : true, "depth" : 0.25 * mm, "offsetDistance" : 25.4 * mm});
        }
        {
            var Q0;
            Q0=makeQuery(id+"F5.opExtrude","CAP_FACE",FACE,{"disambiguationData":[OSD([sQuery(id+"F4.wireOp",EDGE,"E2"),sQuery(id+"F4.wireOp",EDGE,"E3"),sQuery(id+"F4.wireOp",EDGE,"E4"),sQuery(id+"F4.wireOp",EDGE,"E5"),sQuery(id+"F4.wireOp",EDGE,"E6"),sQuery(id+"F4.wireOp",EDGE,"E7"),sQuery(id+"F4.wireOp",EDGE,"E8"),sQuery(id+"F4.wireOp",EDGE,"E9"),sQuery(id+"F4.wireOp",EDGE,"E10"),sQuery(id+"F4.wireOp",EDGE,"E11"),sQuery(id+"F4.wireOp",EDGE,"E12"),sQuery(id+"F4.wireOp",EDGE,"E13"),sQuery(id+"F4.wireOp",EDGE,"E14"),sQuery(id+"F4.wireOp",EDGE,"E15"),sQuery(id+"F4.wireOp",EDGE,"E16"),sQuery(id+"F4.wireOp",EDGE,"E17"),sQuery(id+"F4.wireOp",EDGE,"E18"),sQuery(id+"F4.wireOp",EDGE,"E19"),sQuery(id+"F4.wireOp",EDGE,"E20"),sQuery(id+"F4.wireOp",EDGE,"E21"),sQuery(id+"F4.wireOp",EDGE,"E22"),sQuery(id+"F4.wireOp",EDGE,"E23"),sQuery(id+"F4.wireOp",EDGE,"E24"),sQuery(id+"F4.wireOp",EDGE,"E25"),sQuery(id+"F4.wireOp",EDGE,"E26"),sQuery(id+"F4.wireOp",EDGE,"E27"),sQuery(id+"F4.wireOp",EDGE,"E28"),sQuery(id+"F4.wireOp",EDGE,"E29"),sQuery(id+"F4.wireOp",EDGE,"E30"),sQuery(id+"F4.wireOp",EDGE,"E31"),sQuery(id+"F4.wireOp",EDGE,"E32"),sQuery(id+"F4.wireOp",EDGE,"E33"),sQuery(id+"F4.wireOp",EDGE,"E34"),sQuery(id+"F4.wireOp",EDGE,"E35"),sQuery(id+"F4.wireOp",EDGE,"E36"),sQuery(id+"F4.wireOp",EDGE,"E37"),sQuery(id+"F4.wireOp",EDGE,"E38"),sQuery(id+"F4.wireOp",EDGE,"E39"),sQuery(id+"F4.wireOp",EDGE,"E40"),sQuery(id+"F4.wireOp",EDGE,"E41"),sQuery(id+"F4.wireOp",EDGE,"E42"),sQuery(id+"F4.wireOp",EDGE,"E43"),sQuery(id+"F4.wireOp",EDGE,"E44"),sQuery(id+"F4.wireOp",EDGE,"E45"),sQuery(id+"F4.wireOp",EDGE,"E46"),sQuery(id+"F4.wireOp",EDGE,"E47"),sQuery(id+"F4.wireOp",EDGE,"E48"),sQuery(id+"F4.wireOp",EDGE,"E49"),sQuery(id+"F4.wireOp",EDGE,"E50"),sQuery(id+"F4.wireOp",EDGE,"E51"),sQuery(id+"F4.wireOp",EDGE,"E52"),sQuery(id+"F4.wireOp",EDGE,"E53"),sQuery(id+"F4.wireOp",EDGE,"E54"),sQuery(id+"F4.wireOp",EDGE,"E55"),sQuery(id+"F4.wireOp",EDGE,"E56"),sQuery(id+"F4.wireOp",EDGE,"E57"),sQuery(id+"F4.wireOp",EDGE,"E58"),sQuery(id+"F4.wireOp",EDGE,"E59"),sQuery(id+"F4.wireOp",EDGE,"E60"),sQuery(id+"F4.wireOp",EDGE,"E61"),sQuery(id+"F4.wireOp",EDGE,"E62"),sQuery(id+"F4.wireOp",EDGE,"E63"),sQuery(id+"F4.wireOp",EDGE,"E64"),sQuery(id+"F4.wireOp",EDGE,"E65"),sQuery(id+"F4.wireOp",EDGE,"E66"),sQuery(id+"F4.wireOp",EDGE,"E67"),sQuery(id+"F4.wireOp",EDGE,"E68"),sQuery(id+"F4.wireOp",EDGE,"E69"),sQuery(id+"F4.wireOp",EDGE,"E70"),sQuery(id+"F4.wireOp",EDGE,"E71"),sQuery(id+"F4.wireOp",EDGE,"E72"),sQuery(id+"F4.wireOp",EDGE,"E73"),sQuery(id+"F4.wireOp",EDGE,"E74"),sQuery(id+"F4.wireOp",EDGE,"E75"),sQuery(id+"F4.wireOp",EDGE,"E76"),sQuery(id+"F4.wireOp",EDGE,"E77"),sQuery(id+"F4.wireOp",EDGE,"E78"),sQuery(id+"F4.wireOp",EDGE,"E79"),sQuery(id+"F4.wireOp",EDGE,"E80"),sQuery(id+"F4.wireOp",EDGE,"E81"),sQuery(id+"F4.wireOp",EDGE,"E82"),sQuery(id+"F4.wireOp",EDGE,"E83"),sQuery(id+"F4.wireOp",EDGE,"E84"),sQuery(id+"F4.wireOp",EDGE,"E85"),sQuery(id+"F4.wireOp",EDGE,"E86"),sQuery(id+"F4.wireOp",EDGE,"E87"),sQuery(id+"F4.wireOp",EDGE,"E88"),sQuery(id+"F4.wireOp",EDGE,"E89"),sQuery(id+"F4.wireOp",EDGE,"E90"),sQuery(id+"F4.wireOp",EDGE,"E91"),sQuery(id+"F4.wireOp",EDGE,"E92"),sQuery(id+"F4.wireOp",EDGE,"E93"),sQuery(id+"F4.wireOp",EDGE,"E94"),sQuery(id+"F4.wireOp",EDGE,"E95"),sQuery(id+"F4.wireOp",EDGE,"E96"),sQuery(id+"F4.wireOp",EDGE,"E97"),sQuery(id+"F4.wireOp",EDGE,"E98"),sQuery(id+"F4.wireOp",EDGE,"E99"),sQuery(id+"F4.wireOp",EDGE,"E100"),sQuery(id+"F4.wireOp",EDGE,"E101"),sQuery(id+"F4.wireOp",EDGE,"E102"),sQuery(id+"F4.wireOp",EDGE,"E103"),sQuery(id+"F4.wireOp",EDGE,"E104"),sQuery(id+"F4.wireOp",EDGE,"E105"),sQuery(id+"F4.wireOp",EDGE,"E106"),sQuery(id+"F4.wireOp",EDGE,"E107"),sQuery(id+"F4.wireOp",EDGE,"E108"),sQuery(id+"F4.wireOp",EDGE,"E109"),sQuery(id+"F4.wireOp",EDGE,"E110"),sQuery(id+"F4.wireOp",EDGE,"E111"),sQuery(id+"F4.wireOp",EDGE,"E112"),sQuery(id+"F4.wireOp",EDGE,"E113"),sQuery(id+"F4.wireOp",EDGE,"E114"),sQuery(id+"F4.wireOp",EDGE,"E115"),sQuery(id+"F4.wireOp",EDGE,"E116"),sQuery(id+"F4.wireOp",EDGE,"E117"),sQuery(id+"F4.wireOp",EDGE,"E118"),sQuery(id+"F4.wireOp",EDGE,"E119"),sQuery(id+"F4.wireOp",EDGE,"E120"),sQuery(id+"F4.wireOp",EDGE,"E121"),sQuery(id+"F4.wireOp",EDGE,"E122"),sQuery(id+"F4.wireOp",EDGE,"E123"),sQuery(id+"F4.wireOp",EDGE,"E124"),sQuery(id+"F4.wireOp",EDGE,"E125"),sQuery(id+"F4.wireOp",EDGE,"E126"),sQuery(id+"F4.wireOp",EDGE,"E127"),sQuery(id+"F4.wireOp",EDGE,"E128"),sQuery(id+"F4.wireOp",EDGE,"E129"),sQuery(id+"F4.wireOp",EDGE,"E130"),sQuery(id+"F4.wireOp",EDGE,"E131"),sQuery(id+"F4.wireOp",EDGE,"E132"),sQuery(id+"F4.wireOp",EDGE,"E133"),sQuery(id+"F4.wireOp",EDGE,"E134"),sQuery(id+"F4.wireOp",EDGE,"E135"),sQuery(id+"F4.wireOp",EDGE,"E136"),sQuery(id+"F4.wireOp",EDGE,"E137"),sQuery(id+"F4.wireOp",EDGE,"E138"),sQuery(id+"F4.wireOp",EDGE,"E139"),sQuery(id+"F4.wireOp",EDGE,"E140"),sQuery(id+"F4.wireOp",EDGE,"E141"),sQuery(id+"F4.wireOp",EDGE,"E142"),sQuery(id+"F4.wireOp",EDGE,"E143"),sQuery(id+"F4.wireOp",EDGE,"E144"),sQuery(id+"F4.wireOp",EDGE,"E145"),sQuery(id+"F4.wireOp",EDGE,"E146"),sQuery(id+"F4.wireOp",EDGE,"E147"),sQuery(id+"F4.wireOp",EDGE,"E148"),sQuery(id+"F4.wireOp",EDGE,"E149"),sQuery(id+"F4.wireOp",EDGE,"E150"),sQuery(id+"F4.wireOp",EDGE,"E151"),sQuery(id+"F4.wireOp",EDGE,"E152"),sQuery(id+"F4.wireOp",EDGE,"E153"),sQuery(id+"F4.wireOp",EDGE,"E154"),sQuery(id+"F4.wireOp",EDGE,"E155"),sQuery(id+"F4.wireOp",EDGE,"E156"),sQuery(id+"F4.wireOp",EDGE,"E157"),sQuery(id+"F4.wireOp",EDGE,"E158"),sQuery(id+"F4.wireOp",EDGE,"E159"),sQuery(id+"F4.wireOp",EDGE,"E160"),sQuery(id+"F4.wireOp",EDGE,"E161"),sQuery(id+"F4.wireOp",EDGE,"E162"),sQuery(id+"F4.wireOp",EDGE,"E163"),sQuery(id+"F4.wireOp",EDGE,"E164"),sQuery(id+"F4.wireOp",EDGE,"E165"),sQuery(id+"F4.wireOp",EDGE,"E166"),sQuery(id+"F4.wireOp",EDGE,"E167"),sQuery(id+"F4.wireOp",EDGE,"E168"),sQuery(id+"F4.wireOp",EDGE,"E169"),sQuery(id+"F4.wireOp",EDGE,"E170"),sQuery(id+"F4.wireOp",EDGE,"E171"),sQuery(id+"F4.wireOp",EDGE,"E172"),sQuery(id+"F4.wireOp",EDGE,"E173"),sQuery(id+"F4.wireOp",EDGE,"E174"),sQuery(id+"F4.wireOp",EDGE,"E175"),sQuery(id+"F4.wireOp",EDGE,"E176"),sQuery(id+"F4.wireOp",EDGE,"E177"),sQuery(id+"F4.wireOp",EDGE,"E178"),sQuery(id+"F4.wireOp",EDGE,"E179"),sQuery(id+"F4.wireOp",EDGE,"E180"),sQuery(id+"F4.wireOp",EDGE,"E181"),sQuery(id+"F4.wireOp",EDGE,"E182"),sQuery(id+"F4.wireOp",EDGE,"E183"),sQuery(id+"F4.wireOp",EDGE,"E184"),sQuery(id+"F4.wireOp",EDGE,"E185"),sQuery(id+"F4.wireOp",EDGE,"E186"),sQuery(id+"F4.wireOp",EDGE,"E187"),sQuery(id+"F4.wireOp",EDGE,"E188"),sQuery(id+"F4.wireOp",EDGE,"E189"),sQuery(id+"F4.wireOp",EDGE,"E190"),sQuery(id+"F4.wireOp",EDGE,"E191"),sQuery(id+"F4.wireOp",EDGE,"E192"),sQuery(id+"F4.wireOp",EDGE,"E193"),sQuery(id+"F4.wireOp",EDGE,"E194"),sQuery(id+"F4.wireOp",EDGE,"E195"),sQuery(id+"F4.wireOp",EDGE,"E196"),sQuery(id+"F4.wireOp",EDGE,"E197"),sQuery(id+"F4.wireOp",EDGE,"E198"),sQuery(id+"F4.wireOp",EDGE,"E199"),sQuery(id+"F4.wireOp",EDGE,"E200"),sQuery(id+"F4.wireOp",EDGE,"E201"),sQuery(id+"F4.wireOp",EDGE,"E202"),sQuery(id+"F4.wireOp",EDGE,"E203"),sQuery(id+"F4.wireOp",EDGE,"E204"),sQuery(id+"F4.wireOp",EDGE,"E205"),sQuery(id+"F4.wireOp",EDGE,"E206"),sQuery(id+"F4.wireOp",EDGE,"E207"),sQuery(id+"F4.wireOp",EDGE,"E208"),sQuery(id+"F4.wireOp",EDGE,"E209"),sQuery(id+"F4.wireOp",EDGE,"E210"),sQuery(id+"F4.wireOp",EDGE,"E211"),sQuery(id+"F4.wireOp",EDGE,"E212"),sQuery(id+"F4.wireOp",EDGE,"E213"),sQuery(id+"F4.wireOp",EDGE,"E214"),sQuery(id+"F4.wireOp",EDGE,"E215"),sQuery(id+"F4.wireOp",EDGE,"E216"),sQuery(id+"F4.wireOp",EDGE,"E217"),sQuery(id+"F4.wireOp",EDGE,"E218"),sQuery(id+"F4.wireOp",EDGE,"E220"),sQuery(id+"F4.wireOp",EDGE,"E221"),sQuery(id+"F4.wireOp",EDGE,"E222"),sQuery(id+"F4.wireOp",EDGE,"E223"),sQuery(id+"F4.wireOp",EDGE,"E224"),sQuery(id+"F4.wireOp",EDGE,"E225"),sQuery(id+"F4.wireOp",EDGE,"E226"),sQuery(id+"F4.wireOp",EDGE,"E227"),sQuery(id+"F4.wireOp",EDGE,"E228"),sQuery(id+"F4.wireOp",EDGE,"E229"),sQuery(id+"F4.wireOp",EDGE,"E230"),sQuery(id+"F4.wireOp",EDGE,"E231"),sQuery(id+"F4.wireOp",EDGE,"E232"),sQuery(id+"F4.wireOp",EDGE,"E233"),sQuery(id+"F4.wireOp",EDGE,"E234"),sQuery(id+"F4.wireOp",EDGE,"E235"),sQuery(id+"F4.wireOp",EDGE,"E236"),sQuery(id+"F4.wireOp",EDGE,"E237"),sQuery(id+"F4.wireOp",EDGE,"E238"),sQuery(id+"F4.wireOp",EDGE,"E239"),sQuery(id+"F4.wireOp",EDGE,"E240"),sQuery(id+"F4.wireOp",EDGE,"E241"),sQuery(id+"F4.wireOp",EDGE,"E242"),sQuery(id+"F4.wireOp",EDGE,"E243"),sQuery(id+"F4.wireOp",EDGE,"E244"),sQuery(id+"F4.wireOp",EDGE,"E245"),sQuery(id+"F4.wireOp",EDGE,"E246"),sQuery(id+"F4.wireOp",EDGE,"E247"),sQuery(id+"F4.wireOp",EDGE,"E248"),sQuery(id+"F4.wireOp",EDGE,"E249"),sQuery(id+"F4.wireOp",EDGE,"E250"),sQuery(id+"F4.wireOp",EDGE,"E251"),sQuery(id+"F4.wireOp",EDGE,"E252"),sQuery(id+"F4.wireOp",EDGE,"E253"),sQuery(id+"F4.wireOp",EDGE,"E254"),sQuery(id+"F4.wireOp",EDGE,"E255"),sQuery(id+"F4.wireOp",EDGE,"E256"),sQuery(id+"F4.wireOp",EDGE,"E257"),sQuery(id+"F4.wireOp",EDGE,"E258"),sQuery(id+"F4.wireOp",EDGE,"E259"),sQuery(id+"F4.wireOp",EDGE,"E260"),sQuery(id+"F4.wireOp",EDGE,"E261"),sQuery(id+"F4.wireOp",EDGE,"E262"),sQuery(id+"F4.wireOp",EDGE,"E263"),sQuery(id+"F4.wireOp",EDGE,"E264"),sQuery(id+"F4.wireOp",EDGE,"E265"),sQuery(id+"F4.wireOp",EDGE,"E266"),sQuery(id+"F4.wireOp",EDGE,"E267"),sQuery(id+"F4.wireOp",EDGE,"E268"),sQuery(id+"F4.wireOp",EDGE,"E269"),sQuery(id+"F4.wireOp",EDGE,"E270"),sQuery(id+"F4.wireOp",EDGE,"E271"),sQuery(id+"F4.wireOp",EDGE,"E272"),sQuery(id+"F4.wireOp",EDGE,"E273"),sQuery(id+"F4.wireOp",EDGE,"E274"),sQuery(id+"F4.wireOp",EDGE,"E275"),sQuery(id+"F4.wireOp",EDGE,"E276"),sQuery(id+"F4.wireOp",EDGE,"E277"),sQuery(id+"F4.wireOp",EDGE,"E278"),sQuery(id+"F4.wireOp",EDGE,"E279"),sQuery(id+"F4.wireOp",EDGE,"E280"),sQuery(id+"F4.wireOp",EDGE,"E281"),sQuery(id+"F4.wireOp",EDGE,"E282"),sQuery(id+"F4.wireOp",EDGE,"E283"),sQuery(id+"F4.wireOp",EDGE,"E284"),sQuery(id+"F4.wireOp",EDGE,"E285"),sQuery(id+"F4.wireOp",EDGE,"E286"),sQuery(id+"F4.wireOp",EDGE,"E287"),sQuery(id+"F4.wireOp",EDGE,"E288"),sQuery(id+"F4.wireOp",EDGE,"E289"),sQuery(id+"F4.wireOp",EDGE,"E290"),sQuery(id+"F4.wireOp",EDGE,"E291"),sQuery(id+"F4.wireOp",EDGE,"E292"),sQuery(id+"F4.wireOp",EDGE,"E302"),sQuery(id+"F4.wireOp",EDGE,"E303"),sQuery(id+"F4.wireOp",EDGE,"E304"),sQuery(id+"F4.wireOp",EDGE,"E305"),sQuery(id+"F4.wireOp",EDGE,"E306"),sQuery(id+"F4.wireOp",EDGE,"E307"),sQuery(id+"F4.wireOp",EDGE,"E308"),sQuery(id+"F4.wireOp",EDGE,"E309"),sQuery(id+"F4.wireOp",EDGE,"E310"),sQuery(id+"F4.wireOp",EDGE,"E311"),sQuery(id+"F4.wireOp",EDGE,"E312"),sQuery(id+"F4.wireOp",EDGE,"E313"),sQuery(id+"F4.wireOp",EDGE,"E314"),sQuery(id+"F4.wireOp",EDGE,"E315"),sQuery(id+"F4.wireOp",EDGE,"E316"),sQuery(id+"F4.wireOp",EDGE,"E317"),sQuery(id+"F4.wireOp",EDGE,"E318"),sQuery(id+"F4.wireOp",EDGE,"E319"),sQuery(id+"F4.wireOp",EDGE,"E320"),sQuery(id+"F4.wireOp",EDGE,"E321"),sQuery(id+"F4.wireOp",EDGE,"E322"),sQuery(id+"F4.wireOp",EDGE,"E323"),sQuery(id+"F4.wireOp",EDGE,"E324"),sQuery(id+"F4.wireOp",EDGE,"E325"),sQuery(id+"F4.wireOp",EDGE,"E326"),sQuery(id+"F4.wireOp",EDGE,"E327"),sQuery(id+"F4.wireOp",EDGE,"E328"),sQuery(id+"F4.wireOp",EDGE,"E329"),sQuery(id+"F4.wireOp",EDGE,"E330"),sQuery(id+"F4.wireOp",EDGE,"E331"),sQuery(id+"F4.wireOp",EDGE,"E332"),sQuery(id+"F4.wireOp",EDGE,"E333"),sQuery(id+"F4.wireOp",EDGE,"E334"),sQuery(id+"F4.wireOp",EDGE,"E335"),sQuery(id+"F4.wireOp",EDGE,"E336"),sQuery(id+"F4.wireOp",EDGE,"E337"),sQuery(id+"F4.wireOp",EDGE,"E338"),sQuery(id+"F4.wireOp",EDGE,"E339"),sQuery(id+"F4.wireOp",EDGE,"E340"),sQuery(id+"F4.wireOp",EDGE,"E341"),sQuery(id+"F4.wireOp",EDGE,"E342"),sQuery(id+"F4.wireOp",EDGE,"E343"),sQuery(id+"F4.wireOp",EDGE,"E344"),sQuery(id+"F4.wireOp",EDGE,"E345"),sQuery(id+"F4.wireOp",EDGE,"E346"),sQuery(id+"F4.wireOp",EDGE,"E347"),sQuery(id+"F4.wireOp",EDGE,"E348"),sQuery(id+"F4.wireOp",EDGE,"E349"),sQuery(id+"F4.wireOp",EDGE,"E350"),sQuery(id+"F4.wireOp",EDGE,"E351"),sQuery(id+"F4.wireOp",EDGE,"E352"),sQuery(id+"F4.wireOp",EDGE,"E353"),sQuery(id+"F4.wireOp",EDGE,"E354"),sQuery(id+"F4.wireOp",EDGE,"E355"),sQuery(id+"F4.wireOp",EDGE,"E356"),sQuery(id+"F4.wireOp",EDGE,"E357"),sQuery(id+"F4.wireOp",EDGE,"E358"),sQuery(id+"F4.wireOp",EDGE,"E359"),sQuery(id+"F4.wireOp",EDGE,"E360"),sQuery(id+"F4.wireOp",EDGE,"E361"),sQuery(id+"F4.wireOp",EDGE,"E362"),sQuery(id+"F4.wireOp",EDGE,"E363"),sQuery(id+"F4.wireOp",EDGE,"E364"),sQuery(id+"F4.wireOp",EDGE,"E365"),sQuery(id+"F4.wireOp",EDGE,"E366"),sQuery(id+"F4.wireOp",EDGE,"E367"),sQuery(id+"F4.wireOp",EDGE,"E368"),sQuery(id+"F4.wireOp",EDGE,"E369"),sQuery(id+"F4.wireOp",EDGE,"E370"),sQuery(id+"F4.wireOp",EDGE,"E371"),sQuery(id+"F4.wireOp",EDGE,"E372"),sQuery(id+"F4.wireOp",EDGE,"E373"),sQuery(id+"F4.wireOp",EDGE,"E374"),sQuery(id+"F4.wireOp",EDGE,"E375"),sQuery(id+"F4.wireOp",EDGE,"E376"),sQuery(id+"F4.wireOp",EDGE,"E377"),sQuery(id+"F4.wireOp",EDGE,"E378"),sQuery(id+"F4.wireOp",EDGE,"E379"),sQuery(id+"F4.wireOp",EDGE,"E380"),sQuery(id+"F4.wireOp",EDGE,"E381"),sQuery(id+"F4.wireOp",EDGE,"E382"),sQuery(id+"F4.wireOp",EDGE,"E383"),sQuery(id+"F4.wireOp",EDGE,"E384"),sQuery(id+"F4.wireOp",EDGE,"E385"),sQuery(id+"F4.wireOp",EDGE,"E386"),sQuery(id+"F4.wireOp",EDGE,"E387"),sQuery(id+"F4.wireOp",EDGE,"E388"),sQuery(id+"F4.wireOp",EDGE,"E389"),sQuery(id+"F4.wireOp",EDGE,"E390"),sQuery(id+"F4.wireOp",EDGE,"E391"),sQuery(id+"F4.wireOp",EDGE,"E392"),sQuery(id+"F4.wireOp",EDGE,"E393"),sQuery(id+"F4.wireOp",EDGE,"E394"),sQuery(id+"F4.wireOp",EDGE,"E395"),sQuery(id+"F4.wireOp",EDGE,"E396"),sQuery(id+"F4.wireOp",EDGE,"E397"),sQuery(id+"F4.wireOp",EDGE,"E398"),sQuery(id+"F4.wireOp",EDGE,"E399"),sQuery(id+"F4.wireOp",EDGE,"E400"),sQuery(id+"F4.wireOp",EDGE,"E401"),sQuery(id+"F4.wireOp",EDGE,"E402"),sQuery(id+"F4.wireOp",EDGE,"E403"),sQuery(id+"F4.wireOp",EDGE,"E404"),sQuery(id+"F4.wireOp",EDGE,"E405"),sQuery(id+"F4.wireOp",EDGE,"E406"),sQuery(id+"F4.wireOp",EDGE,"E407"),sQuery(id+"F4.wireOp",EDGE,"E408"),sQuery(id+"F4.wireOp",EDGE,"E409"),sQuery(id+"F4.wireOp",EDGE,"E410"),sQuery(id+"F4.wireOp",EDGE,"E411"),sQuery(id+"F4.wireOp",EDGE,"E412"),sQuery(id+"F4.wireOp",EDGE,"E413"),sQuery(id+"F4.wireOp",EDGE,"E414"),sQuery(id+"F4.wireOp",EDGE,"E415"),sQuery(id+"F4.wireOp",EDGE,"E416"),sQuery(id+"F4.wireOp",EDGE,"E417"),sQuery(id+"F4.wireOp",EDGE,"E418"),sQuery(id+"F4.wireOp",EDGE,"E419"),sQuery(id+"F4.wireOp",EDGE,"E420"),sQuery(id+"F4.wireOp",EDGE,"E421"),sQuery(id+"F4.wireOp",EDGE,"E422"),sQuery(id+"F4.wireOp",EDGE,"E423"),sQuery(id+"F4.wireOp",EDGE,"E424"),sQuery(id+"F4.wireOp",EDGE,"E425"),sQuery(id+"F4.wireOp",EDGE,"E426"),sQuery(id+"F4.wireOp",EDGE,"E427")])],"isStart":false});
            var sketch = newSketch(context, id + "F8", { "sketchPlane" : qUnion([Q0])});
            skLineSegment(sketch, "E542", {"start": v(30.37, 11.45) * mm, "end": v(30.32, 11.26) * mm});
            skLineSegment(sketch, "E543", {"start": v(30.32, 11.26) * mm, "end": v(30.33, 11.08) * mm});
            skLineSegment(sketch, "E544", {"start": v(30.33, 11.08) * mm, "end": v(30.4, 10.9) * mm});
            skLineSegment(sketch, "E545", {"start": v(30.4, 10.9) * mm, "end": v(30.5, 10.77) * mm});
            skLineSegment(sketch, "E546", {"start": v(30.5, 10.77) * mm, "end": v(30.61, 10.73) * mm});
            skLineSegment(sketch, "E547", {"start": v(30.61, 10.73) * mm, "end": v(30.74, 10.84) * mm});
            skLineSegment(sketch, "E548", {"start": v(30.74, 10.84) * mm, "end": v(30.84, 11.01) * mm});
            skLineSegment(sketch, "E549", {"start": v(30.84, 11.01) * mm, "end": v(30.88, 11.23) * mm});
            skLineSegment(sketch, "E550", {"start": v(30.88, 11.23) * mm, "end": v(30.83, 11.48) * mm});
            skLineSegment(sketch, "E551", {"start": v(30.83, 11.48) * mm, "end": v(30.75, 11.64) * mm});
            skLineSegment(sketch, "E552", {"start": v(30.75, 11.64) * mm, "end": v(30.65, 11.66) * mm});
            skLineSegment(sketch, "E553", {"start": v(30.65, 11.66) * mm, "end": v(30.5, 11.62) * mm});
            skLineSegment(sketch, "E554", {"start": v(30.5, 11.62) * mm, "end": v(30.38, 11.48) * mm});
            skLineSegment(sketch, "E555", {"start": v(32.03, 11.55) * mm, "end": v(31.8, 11.17) * mm});
            skLineSegment(sketch, "E556", {"start": v(31.8, 11.17) * mm, "end": v(31.56, 10.8) * mm});
            skLineSegment(sketch, "E557", {"start": v(31.56, 10.8) * mm, "end": v(31.3, 10.53) * mm});
            skLineSegment(sketch, "E558", {"start": v(31.3, 10.53) * mm, "end": v(31.13, 10.3) * mm});
            skLineSegment(sketch, "E559", {"start": v(31.13, 10.3) * mm, "end": v(31.07, 10.1) * mm});
            skLineSegment(sketch, "E560", {"start": v(31.07, 10.1) * mm, "end": v(31.12, 9.93) * mm});
            skLineSegment(sketch, "E561", {"start": v(31.12, 9.93) * mm, "end": v(31.28, 9.68) * mm});
            skLineSegment(sketch, "E562", {"start": v(31.28, 9.68) * mm, "end": v(31.46, 9.54) * mm});
            skLineSegment(sketch, "E563", {"start": v(31.46, 9.54) * mm, "end": v(31.6, 9.49) * mm});
            skLineSegment(sketch, "E564", {"start": v(31.6, 9.49) * mm, "end": v(31.65, 9.54) * mm});
            skLineSegment(sketch, "E565", {"start": v(31.65, 9.54) * mm, "end": v(31.67, 9.6) * mm});
            skLineSegment(sketch, "E566", {"start": v(31.67, 9.6) * mm, "end": v(31.64, 9.72) * mm});
            skLineSegment(sketch, "E567", {"start": v(31.64, 9.72) * mm, "end": v(31.55, 9.83) * mm});
            skLineSegment(sketch, "E568", {"start": v(31.55, 9.83) * mm, "end": v(31.44, 10.03) * mm});
            skLineSegment(sketch, "E569", {"start": v(31.44, 10.03) * mm, "end": v(31.46, 10.22) * mm});
            skLineSegment(sketch, "E570", {"start": v(31.46, 10.22) * mm, "end": v(31.68, 10.46) * mm});
            skLineSegment(sketch, "E571", {"start": v(31.68, 10.46) * mm, "end": v(31.93, 10.8) * mm});
            skLineSegment(sketch, "E572", {"start": v(31.93, 10.8) * mm, "end": v(32.05, 11.11) * mm});
            skLineSegment(sketch, "E573", {"start": v(32.05, 11.11) * mm, "end": v(32.1, 11.41) * mm});
            skLineSegment(sketch, "E574", {"start": v(32.1, 11.41) * mm, "end": v(32.03, 11.55) * mm});
            skLineSegment(sketch, "E575", {"start": v(32.94, 11.19) * mm, "end": v(33.1, 11.14) * mm});
            skLineSegment(sketch, "E576", {"start": v(33.1, 11.14) * mm, "end": v(33.26, 11.13) * mm});
            skLineSegment(sketch, "E577", {"start": v(33.26, 11.13) * mm, "end": v(33.42, 11.1) * mm});
            skLineSegment(sketch, "E578", {"start": v(33.42, 11.1) * mm, "end": v(33.52, 11.02) * mm});
            skLineSegment(sketch, "E579", {"start": v(33.52, 11.02) * mm, "end": v(33.66, 10.93) * mm});
            skLineSegment(sketch, "E580", {"start": v(33.66, 10.93) * mm, "end": v(33.79, 10.78) * mm});
            skLineSegment(sketch, "E581", {"start": v(33.79, 10.78) * mm, "end": v(33.94, 10.65) * mm});
            skLineSegment(sketch, "E582", {"start": v(33.94, 10.65) * mm, "end": v(34.08, 10.63) * mm});
            skLineSegment(sketch, "E583", {"start": v(34.08, 10.63) * mm, "end": v(34.15, 10.72) * mm});
            skLineSegment(sketch, "E584", {"start": v(34.15, 10.72) * mm, "end": v(34.17, 10.87) * mm});
            skLineSegment(sketch, "E585", {"start": v(34.17, 10.87) * mm, "end": v(34.11, 11.07) * mm});
            skLineSegment(sketch, "E586", {"start": v(34.11, 11.07) * mm, "end": v(33.99, 11.22) * mm});
            skLineSegment(sketch, "E587", {"start": v(33.99, 11.22) * mm, "end": v(33.85, 11.36) * mm});
            skLineSegment(sketch, "E588", {"start": v(33.85, 11.36) * mm, "end": v(33.68, 11.43) * mm});
            skLineSegment(sketch, "E589", {"start": v(33.68, 11.43) * mm, "end": v(33.49, 11.48) * mm});
            skLineSegment(sketch, "E590", {"start": v(33.49, 11.48) * mm, "end": v(33.32, 11.48) * mm});
            skLineSegment(sketch, "E591", {"start": v(33.32, 11.48) * mm, "end": v(33.17, 11.45) * mm});
            skLineSegment(sketch, "E592", {"start": v(33.17, 11.45) * mm, "end": v(33, 11.36) * mm});
            skLineSegment(sketch, "E593", {"start": v(33, 11.36) * mm, "end": v(32.93, 11.28) * mm});
            skLineSegment(sketch, "E594", {"start": v(32.93, 11.28) * mm, "end": v(32.94, 11.19) * mm});
            skLineSegment(sketch, "E595", {"start": v(30.11, 9.07) * mm, "end": v(29.99, 8.96) * mm});
            skLineSegment(sketch, "E596", {"start": v(29.99, 8.96) * mm, "end": v(29.95, 8.81) * mm});
            skLineSegment(sketch, "E597", {"start": v(29.95, 8.81) * mm, "end": v(29.96, 8.63) * mm});
            skLineSegment(sketch, "E598", {"start": v(29.96, 8.63) * mm, "end": v(30.02, 8.5) * mm});
            skLineSegment(sketch, "E599", {"start": v(30.02, 8.5) * mm, "end": v(30.1, 8.39) * mm});
            skLineSegment(sketch, "E600", {"start": v(30.1, 8.39) * mm, "end": v(30.18, 8.29) * mm});
            skLineSegment(sketch, "E601", {"start": v(30.18, 8.29) * mm, "end": v(30.24, 8.32) * mm});
            skLineSegment(sketch, "E602", {"start": v(30.24, 8.32) * mm, "end": v(30.22, 8.57) * mm});
            skLineSegment(sketch, "E603", {"start": v(30.22, 8.57) * mm, "end": v(30.34, 8.49) * mm});
            skLineSegment(sketch, "E604", {"start": v(30.34, 8.49) * mm, "end": v(30.5, 8.4) * mm});
            skLineSegment(sketch, "E605", {"start": v(30.5, 8.4) * mm, "end": v(30.72, 8.28) * mm});
            skLineSegment(sketch, "E606", {"start": v(30.72, 8.28) * mm, "end": v(30.9, 8.2) * mm});
            skLineSegment(sketch, "E607", {"start": v(30.9, 8.2) * mm, "end": v(31.2, 8.1) * mm});
            skLineSegment(sketch, "E608", {"start": v(31.2, 8.1) * mm, "end": v(31.5, 8.03) * mm});
            skLineSegment(sketch, "E609", {"start": v(31.5, 8.03) * mm, "end": v(31.8, 8.03) * mm});
            skLineSegment(sketch, "E610", {"start": v(31.8, 8.03) * mm, "end": v(32, 8.05) * mm});
            skLineSegment(sketch, "E611", {"start": v(32, 8.05) * mm, "end": v(32.3, 8.1) * mm});
            skLineSegment(sketch, "E612", {"start": v(32.3, 8.1) * mm, "end": v(32.58, 8.19) * mm});
            skLineSegment(sketch, "E613", {"start": v(32.58, 8.19) * mm, "end": v(32.88, 8.3) * mm});
            skLineSegment(sketch, "E614", {"start": v(32.88, 8.3) * mm, "end": v(33.1, 8.42) * mm});
            skLineSegment(sketch, "E615", {"start": v(33.1, 8.42) * mm, "end": v(33.25, 8.53) * mm});
            skLineSegment(sketch, "E616", {"start": v(33.25, 8.53) * mm, "end": v(33.38, 8.6) * mm});
            skLineSegment(sketch, "E617", {"start": v(33.38, 8.6) * mm, "end": v(33.5, 8.66) * mm});
            skLineSegment(sketch, "E618", {"start": v(33.5, 8.66) * mm, "end": v(33.62, 8.6) * mm});
            skLineSegment(sketch, "E619", {"start": v(33.62, 8.6) * mm, "end": v(33.67, 8.42) * mm});
            skLineSegment(sketch, "E620", {"start": v(33.67, 8.42) * mm, "end": v(33.68, 8.37) * mm});
            skLineSegment(sketch, "E621", {"start": v(33.68, 8.37) * mm, "end": v(33.71, 8.36) * mm});
            skLineSegment(sketch, "E622", {"start": v(33.71, 8.36) * mm, "end": v(33.74, 8.42) * mm});
            skLineSegment(sketch, "E623", {"start": v(33.74, 8.42) * mm, "end": v(33.78, 8.68) * mm});
            skLineSegment(sketch, "E624", {"start": v(33.78, 8.68) * mm, "end": v(33.77, 8.86) * mm});
            skLineSegment(sketch, "E625", {"start": v(33.77, 8.86) * mm, "end": v(33.74, 8.96) * mm});
            skLineSegment(sketch, "E626", {"start": v(33.74, 8.96) * mm, "end": v(33.62, 9.09) * mm});
            skLineSegment(sketch, "E627", {"start": v(33.62, 9.09) * mm, "end": v(33.5, 9.22) * mm});
            skLineSegment(sketch, "E628", {"start": v(33.5, 9.22) * mm, "end": v(33.34, 9.31) * mm});
            skLineSegment(sketch, "E629", {"start": v(33.34, 9.31) * mm, "end": v(33.2, 9.41) * mm});
            skLineSegment(sketch, "E630", {"start": v(33.2, 9.41) * mm, "end": v(33.12, 9.47) * mm});
            skLineSegment(sketch, "E631", {"start": v(33.12, 9.47) * mm, "end": v(33.1, 9.46) * mm});
            skLineSegment(sketch, "E632", {"start": v(33.1, 9.46) * mm, "end": v(33.1, 9.43) * mm});
            skLineSegment(sketch, "E633", {"start": v(33.1, 9.43) * mm, "end": v(33.1, 9.38) * mm});
            skLineSegment(sketch, "E634", {"start": v(33.1, 9.38) * mm, "end": v(33.16, 9.32) * mm});
            skLineSegment(sketch, "E635", {"start": v(33.16, 9.32) * mm, "end": v(33.2, 9.25) * mm});
            skLineSegment(sketch, "E636", {"start": v(33.2, 9.25) * mm, "end": v(33.16, 9.14) * mm});
            skLineSegment(sketch, "E637", {"start": v(33.16, 9.14) * mm, "end": v(33.07, 9.08) * mm});
            skLineSegment(sketch, "E638", {"start": v(33.07, 9.08) * mm, "end": v(32.97, 9.01) * mm});
            skLineSegment(sketch, "E639", {"start": v(32.97, 9.01) * mm, "end": v(32.82, 8.92) * mm});
            skLineSegment(sketch, "E640", {"start": v(32.82, 8.92) * mm, "end": v(32.6, 8.85) * mm});
            skLineSegment(sketch, "E641", {"start": v(32.6, 8.85) * mm, "end": v(32.42, 8.78) * mm});
            skLineSegment(sketch, "E642", {"start": v(32.42, 8.78) * mm, "end": v(32.2, 8.73) * mm});
            skLineSegment(sketch, "E643", {"start": v(32.2, 8.73) * mm, "end": v(31.98, 8.7) * mm});
            skLineSegment(sketch, "E644", {"start": v(31.98, 8.7) * mm, "end": v(31.54, 8.69) * mm});
            skLineSegment(sketch, "E645", {"start": v(31.54, 8.69) * mm, "end": v(31.23, 8.68) * mm});
            skLineSegment(sketch, "E646", {"start": v(31.23, 8.68) * mm, "end": v(30.96, 8.7) * mm});
            skLineSegment(sketch, "E647", {"start": v(30.96, 8.7) * mm, "end": v(30.72, 8.73) * mm});
            skLineSegment(sketch, "E648", {"start": v(30.72, 8.73) * mm, "end": v(30.55, 8.79) * mm});
            skLineSegment(sketch, "E649", {"start": v(30.55, 8.79) * mm, "end": v(30.39, 8.86) * mm});
            skLineSegment(sketch, "E650", {"start": v(30.39, 8.86) * mm, "end": v(30.24, 8.94) * mm});
            skLineSegment(sketch, "E651", {"start": v(30.24, 8.94) * mm, "end": v(30.21, 8.97) * mm});
            skLineSegment(sketch, "E652", {"start": v(30.21, 8.97) * mm, "end": v(30.2, 9.04) * mm});
            skLineSegment(sketch, "E653", {"start": v(30.2, 9.04) * mm, "end": v(30.19, 9.07) * mm});
            skLineSegment(sketch, "E654", {"start": v(30.19, 9.07) * mm, "end": v(30.17, 9.1) * mm});
            skLineSegment(sketch, "E655", {"start": v(30.17, 9.1) * mm, "end": v(30.11, 9.07) * mm});
            skLineSegment(sketch, "E656", {"start": v(31.18, 7.53) * mm, "end": v(31.25, 7.47) * mm});
            skLineSegment(sketch, "E657", {"start": v(31.25, 7.47) * mm, "end": v(31.33, 7.38) * mm});
            skLineSegment(sketch, "E658", {"start": v(31.33, 7.38) * mm, "end": v(31.47, 7.32) * mm});
            skLineSegment(sketch, "E659", {"start": v(31.47, 7.32) * mm, "end": v(31.6, 7.3) * mm});
            skLineSegment(sketch, "E660", {"start": v(31.6, 7.3) * mm, "end": v(31.7, 7.34) * mm});
            skLineSegment(sketch, "E661", {"start": v(31.7, 7.34) * mm, "end": v(31.78, 7.37) * mm});
            skLineSegment(sketch, "E662", {"start": v(31.78, 7.37) * mm, "end": v(31.86, 7.37) * mm});
            skLineSegment(sketch, "E663", {"start": v(31.86, 7.37) * mm, "end": v(31.93, 7.4) * mm});
            skLineSegment(sketch, "E664", {"start": v(31.93, 7.4) * mm, "end": v(31.96, 7.5) * mm});
            skLineSegment(sketch, "E665", {"start": v(31.96, 7.5) * mm, "end": v(31.94, 7.56) * mm});
            skLineSegment(sketch, "E666", {"start": v(31.94, 7.56) * mm, "end": v(31.85, 7.63) * mm});
            skLineSegment(sketch, "E667", {"start": v(31.85, 7.63) * mm, "end": v(31.76, 7.66) * mm});
            skLineSegment(sketch, "E668", {"start": v(31.76, 7.66) * mm, "end": v(31.68, 7.68) * mm});
            skLineSegment(sketch, "E669", {"start": v(31.68, 7.68) * mm, "end": v(31.62, 7.66) * mm});
            skLineSegment(sketch, "E670", {"start": v(31.62, 7.66) * mm, "end": v(31.53, 7.62) * mm});
            skLineSegment(sketch, "E671", {"start": v(31.53, 7.62) * mm, "end": v(31.44, 7.6) * mm});
            skLineSegment(sketch, "E672", {"start": v(31.44, 7.6) * mm, "end": v(31.34, 7.6) * mm});
            skLineSegment(sketch, "E673", {"start": v(31.34, 7.6) * mm, "end": v(31.27, 7.56) * mm});
            skLineSegment(sketch, "E674", {"start": v(31.27, 7.56) * mm, "end": v(31.18, 7.53) * mm});
            skLineSegment(sketch, "E675", {"start": v(30.38, 11.48) * mm, "end": v(30.37, 11.45) * mm});
            skSolve(sketch);
        }
        {
            var Q0;
            Q0 = qSketchRegion(id + "F8", true);
            extrude(context, id + "F9", {"entities" : qUnion([Q0]), "operationType" : NewBodyOperationType.REMOVE, "oppositeDirection" : true, "depth" : 0.03 * mm, "offsetDistance" : 25.4 * mm});
        }
        {
            var Q0;
            Q0=makeQuery(id+"F5.opExtrude","CAP_FACE",FACE,{"disambiguationData":[OSD([sQuery(id+"F4.wireOp",EDGE,"E2"),sQuery(id+"F4.wireOp",EDGE,"E3"),sQuery(id+"F4.wireOp",EDGE,"E4"),sQuery(id+"F4.wireOp",EDGE,"E5"),sQuery(id+"F4.wireOp",EDGE,"E6"),sQuery(id+"F4.wireOp",EDGE,"E7"),sQuery(id+"F4.wireOp",EDGE,"E8"),sQuery(id+"F4.wireOp",EDGE,"E9"),sQuery(id+"F4.wireOp",EDGE,"E10"),sQuery(id+"F4.wireOp",EDGE,"E11"),sQuery(id+"F4.wireOp",EDGE,"E12"),sQuery(id+"F4.wireOp",EDGE,"E13"),sQuery(id+"F4.wireOp",EDGE,"E14"),sQuery(id+"F4.wireOp",EDGE,"E15"),sQuery(id+"F4.wireOp",EDGE,"E16"),sQuery(id+"F4.wireOp",EDGE,"E17"),sQuery(id+"F4.wireOp",EDGE,"E18"),sQuery(id+"F4.wireOp",EDGE,"E19"),sQuery(id+"F4.wireOp",EDGE,"E20"),sQuery(id+"F4.wireOp",EDGE,"E21"),sQuery(id+"F4.wireOp",EDGE,"E22"),sQuery(id+"F4.wireOp",EDGE,"E23"),sQuery(id+"F4.wireOp",EDGE,"E24"),sQuery(id+"F4.wireOp",EDGE,"E25"),sQuery(id+"F4.wireOp",EDGE,"E26"),sQuery(id+"F4.wireOp",EDGE,"E27"),sQuery(id+"F4.wireOp",EDGE,"E28"),sQuery(id+"F4.wireOp",EDGE,"E29"),sQuery(id+"F4.wireOp",EDGE,"E30"),sQuery(id+"F4.wireOp",EDGE,"E31"),sQuery(id+"F4.wireOp",EDGE,"E32"),sQuery(id+"F4.wireOp",EDGE,"E33"),sQuery(id+"F4.wireOp",EDGE,"E34"),sQuery(id+"F4.wireOp",EDGE,"E35"),sQuery(id+"F4.wireOp",EDGE,"E36"),sQuery(id+"F4.wireOp",EDGE,"E37"),sQuery(id+"F4.wireOp",EDGE,"E38"),sQuery(id+"F4.wireOp",EDGE,"E39"),sQuery(id+"F4.wireOp",EDGE,"E40"),sQuery(id+"F4.wireOp",EDGE,"E41"),sQuery(id+"F4.wireOp",EDGE,"E42"),sQuery(id+"F4.wireOp",EDGE,"E43"),sQuery(id+"F4.wireOp",EDGE,"E44"),sQuery(id+"F4.wireOp",EDGE,"E45"),sQuery(id+"F4.wireOp",EDGE,"E46"),sQuery(id+"F4.wireOp",EDGE,"E47"),sQuery(id+"F4.wireOp",EDGE,"E48"),sQuery(id+"F4.wireOp",EDGE,"E49"),sQuery(id+"F4.wireOp",EDGE,"E50"),sQuery(id+"F4.wireOp",EDGE,"E51"),sQuery(id+"F4.wireOp",EDGE,"E52"),sQuery(id+"F4.wireOp",EDGE,"E53"),sQuery(id+"F4.wireOp",EDGE,"E54"),sQuery(id+"F4.wireOp",EDGE,"E55"),sQuery(id+"F4.wireOp",EDGE,"E56"),sQuery(id+"F4.wireOp",EDGE,"E57"),sQuery(id+"F4.wireOp",EDGE,"E58"),sQuery(id+"F4.wireOp",EDGE,"E59"),sQuery(id+"F4.wireOp",EDGE,"E60"),sQuery(id+"F4.wireOp",EDGE,"E61"),sQuery(id+"F4.wireOp",EDGE,"E62"),sQuery(id+"F4.wireOp",EDGE,"E63"),sQuery(id+"F4.wireOp",EDGE,"E64"),sQuery(id+"F4.wireOp",EDGE,"E65"),sQuery(id+"F4.wireOp",EDGE,"E66"),sQuery(id+"F4.wireOp",EDGE,"E67"),sQuery(id+"F4.wireOp",EDGE,"E68"),sQuery(id+"F4.wireOp",EDGE,"E69"),sQuery(id+"F4.wireOp",EDGE,"E70"),sQuery(id+"F4.wireOp",EDGE,"E71"),sQuery(id+"F4.wireOp",EDGE,"E72"),sQuery(id+"F4.wireOp",EDGE,"E73"),sQuery(id+"F4.wireOp",EDGE,"E74"),sQuery(id+"F4.wireOp",EDGE,"E75"),sQuery(id+"F4.wireOp",EDGE,"E76"),sQuery(id+"F4.wireOp",EDGE,"E77"),sQuery(id+"F4.wireOp",EDGE,"E78"),sQuery(id+"F4.wireOp",EDGE,"E79"),sQuery(id+"F4.wireOp",EDGE,"E80"),sQuery(id+"F4.wireOp",EDGE,"E81"),sQuery(id+"F4.wireOp",EDGE,"E82"),sQuery(id+"F4.wireOp",EDGE,"E83"),sQuery(id+"F4.wireOp",EDGE,"E84"),sQuery(id+"F4.wireOp",EDGE,"E85"),sQuery(id+"F4.wireOp",EDGE,"E86"),sQuery(id+"F4.wireOp",EDGE,"E87"),sQuery(id+"F4.wireOp",EDGE,"E88"),sQuery(id+"F4.wireOp",EDGE,"E89"),sQuery(id+"F4.wireOp",EDGE,"E90"),sQuery(id+"F4.wireOp",EDGE,"E91"),sQuery(id+"F4.wireOp",EDGE,"E92"),sQuery(id+"F4.wireOp",EDGE,"E93"),sQuery(id+"F4.wireOp",EDGE,"E94"),sQuery(id+"F4.wireOp",EDGE,"E95"),sQuery(id+"F4.wireOp",EDGE,"E96"),sQuery(id+"F4.wireOp",EDGE,"E97"),sQuery(id+"F4.wireOp",EDGE,"E98"),sQuery(id+"F4.wireOp",EDGE,"E99"),sQuery(id+"F4.wireOp",EDGE,"E100"),sQuery(id+"F4.wireOp",EDGE,"E101"),sQuery(id+"F4.wireOp",EDGE,"E102"),sQuery(id+"F4.wireOp",EDGE,"E103"),sQuery(id+"F4.wireOp",EDGE,"E104"),sQuery(id+"F4.wireOp",EDGE,"E105"),sQuery(id+"F4.wireOp",EDGE,"E106"),sQuery(id+"F4.wireOp",EDGE,"E107"),sQuery(id+"F4.wireOp",EDGE,"E108"),sQuery(id+"F4.wireOp",EDGE,"E109"),sQuery(id+"F4.wireOp",EDGE,"E110"),sQuery(id+"F4.wireOp",EDGE,"E111"),sQuery(id+"F4.wireOp",EDGE,"E112"),sQuery(id+"F4.wireOp",EDGE,"E113"),sQuery(id+"F4.wireOp",EDGE,"E114"),sQuery(id+"F4.wireOp",EDGE,"E115"),sQuery(id+"F4.wireOp",EDGE,"E116"),sQuery(id+"F4.wireOp",EDGE,"E117"),sQuery(id+"F4.wireOp",EDGE,"E118"),sQuery(id+"F4.wireOp",EDGE,"E119"),sQuery(id+"F4.wireOp",EDGE,"E120"),sQuery(id+"F4.wireOp",EDGE,"E121"),sQuery(id+"F4.wireOp",EDGE,"E122"),sQuery(id+"F4.wireOp",EDGE,"E123"),sQuery(id+"F4.wireOp",EDGE,"E124"),sQuery(id+"F4.wireOp",EDGE,"E125"),sQuery(id+"F4.wireOp",EDGE,"E126"),sQuery(id+"F4.wireOp",EDGE,"E127"),sQuery(id+"F4.wireOp",EDGE,"E128"),sQuery(id+"F4.wireOp",EDGE,"E129"),sQuery(id+"F4.wireOp",EDGE,"E130"),sQuery(id+"F4.wireOp",EDGE,"E131"),sQuery(id+"F4.wireOp",EDGE,"E132"),sQuery(id+"F4.wireOp",EDGE,"E133"),sQuery(id+"F4.wireOp",EDGE,"E134"),sQuery(id+"F4.wireOp",EDGE,"E135"),sQuery(id+"F4.wireOp",EDGE,"E136"),sQuery(id+"F4.wireOp",EDGE,"E137"),sQuery(id+"F4.wireOp",EDGE,"E138"),sQuery(id+"F4.wireOp",EDGE,"E139"),sQuery(id+"F4.wireOp",EDGE,"E140"),sQuery(id+"F4.wireOp",EDGE,"E141"),sQuery(id+"F4.wireOp",EDGE,"E142"),sQuery(id+"F4.wireOp",EDGE,"E143"),sQuery(id+"F4.wireOp",EDGE,"E144"),sQuery(id+"F4.wireOp",EDGE,"E145"),sQuery(id+"F4.wireOp",EDGE,"E146"),sQuery(id+"F4.wireOp",EDGE,"E147"),sQuery(id+"F4.wireOp",EDGE,"E148"),sQuery(id+"F4.wireOp",EDGE,"E149"),sQuery(id+"F4.wireOp",EDGE,"E150"),sQuery(id+"F4.wireOp",EDGE,"E151"),sQuery(id+"F4.wireOp",EDGE,"E152"),sQuery(id+"F4.wireOp",EDGE,"E153"),sQuery(id+"F4.wireOp",EDGE,"E154"),sQuery(id+"F4.wireOp",EDGE,"E155"),sQuery(id+"F4.wireOp",EDGE,"E156"),sQuery(id+"F4.wireOp",EDGE,"E157"),sQuery(id+"F4.wireOp",EDGE,"E158"),sQuery(id+"F4.wireOp",EDGE,"E159"),sQuery(id+"F4.wireOp",EDGE,"E160"),sQuery(id+"F4.wireOp",EDGE,"E161"),sQuery(id+"F4.wireOp",EDGE,"E162"),sQuery(id+"F4.wireOp",EDGE,"E163"),sQuery(id+"F4.wireOp",EDGE,"E164"),sQuery(id+"F4.wireOp",EDGE,"E165"),sQuery(id+"F4.wireOp",EDGE,"E166"),sQuery(id+"F4.wireOp",EDGE,"E167"),sQuery(id+"F4.wireOp",EDGE,"E168"),sQuery(id+"F4.wireOp",EDGE,"E169"),sQuery(id+"F4.wireOp",EDGE,"E170"),sQuery(id+"F4.wireOp",EDGE,"E171"),sQuery(id+"F4.wireOp",EDGE,"E172"),sQuery(id+"F4.wireOp",EDGE,"E173"),sQuery(id+"F4.wireOp",EDGE,"E174"),sQuery(id+"F4.wireOp",EDGE,"E175"),sQuery(id+"F4.wireOp",EDGE,"E176"),sQuery(id+"F4.wireOp",EDGE,"E177"),sQuery(id+"F4.wireOp",EDGE,"E178"),sQuery(id+"F4.wireOp",EDGE,"E179"),sQuery(id+"F4.wireOp",EDGE,"E180"),sQuery(id+"F4.wireOp",EDGE,"E181"),sQuery(id+"F4.wireOp",EDGE,"E182"),sQuery(id+"F4.wireOp",EDGE,"E183"),sQuery(id+"F4.wireOp",EDGE,"E184"),sQuery(id+"F4.wireOp",EDGE,"E185"),sQuery(id+"F4.wireOp",EDGE,"E186"),sQuery(id+"F4.wireOp",EDGE,"E187"),sQuery(id+"F4.wireOp",EDGE,"E188"),sQuery(id+"F4.wireOp",EDGE,"E189"),sQuery(id+"F4.wireOp",EDGE,"E190"),sQuery(id+"F4.wireOp",EDGE,"E191"),sQuery(id+"F4.wireOp",EDGE,"E192"),sQuery(id+"F4.wireOp",EDGE,"E193"),sQuery(id+"F4.wireOp",EDGE,"E194"),sQuery(id+"F4.wireOp",EDGE,"E195"),sQuery(id+"F4.wireOp",EDGE,"E196"),sQuery(id+"F4.wireOp",EDGE,"E197"),sQuery(id+"F4.wireOp",EDGE,"E198"),sQuery(id+"F4.wireOp",EDGE,"E199"),sQuery(id+"F4.wireOp",EDGE,"E200"),sQuery(id+"F4.wireOp",EDGE,"E201"),sQuery(id+"F4.wireOp",EDGE,"E202"),sQuery(id+"F4.wireOp",EDGE,"E203"),sQuery(id+"F4.wireOp",EDGE,"E204"),sQuery(id+"F4.wireOp",EDGE,"E205"),sQuery(id+"F4.wireOp",EDGE,"E206"),sQuery(id+"F4.wireOp",EDGE,"E207"),sQuery(id+"F4.wireOp",EDGE,"E208"),sQuery(id+"F4.wireOp",EDGE,"E209"),sQuery(id+"F4.wireOp",EDGE,"E210"),sQuery(id+"F4.wireOp",EDGE,"E211"),sQuery(id+"F4.wireOp",EDGE,"E212"),sQuery(id+"F4.wireOp",EDGE,"E213"),sQuery(id+"F4.wireOp",EDGE,"E214"),sQuery(id+"F4.wireOp",EDGE,"E215"),sQuery(id+"F4.wireOp",EDGE,"E216"),sQuery(id+"F4.wireOp",EDGE,"E217"),sQuery(id+"F4.wireOp",EDGE,"E218"),sQuery(id+"F4.wireOp",EDGE,"E220"),sQuery(id+"F4.wireOp",EDGE,"E221"),sQuery(id+"F4.wireOp",EDGE,"E222"),sQuery(id+"F4.wireOp",EDGE,"E223"),sQuery(id+"F4.wireOp",EDGE,"E224"),sQuery(id+"F4.wireOp",EDGE,"E225"),sQuery(id+"F4.wireOp",EDGE,"E226"),sQuery(id+"F4.wireOp",EDGE,"E227"),sQuery(id+"F4.wireOp",EDGE,"E228"),sQuery(id+"F4.wireOp",EDGE,"E229"),sQuery(id+"F4.wireOp",EDGE,"E230"),sQuery(id+"F4.wireOp",EDGE,"E231"),sQuery(id+"F4.wireOp",EDGE,"E232"),sQuery(id+"F4.wireOp",EDGE,"E233"),sQuery(id+"F4.wireOp",EDGE,"E234"),sQuery(id+"F4.wireOp",EDGE,"E235"),sQuery(id+"F4.wireOp",EDGE,"E236"),sQuery(id+"F4.wireOp",EDGE,"E237"),sQuery(id+"F4.wireOp",EDGE,"E238"),sQuery(id+"F4.wireOp",EDGE,"E239"),sQuery(id+"F4.wireOp",EDGE,"E240"),sQuery(id+"F4.wireOp",EDGE,"E241"),sQuery(id+"F4.wireOp",EDGE,"E242"),sQuery(id+"F4.wireOp",EDGE,"E243"),sQuery(id+"F4.wireOp",EDGE,"E244"),sQuery(id+"F4.wireOp",EDGE,"E245"),sQuery(id+"F4.wireOp",EDGE,"E246"),sQuery(id+"F4.wireOp",EDGE,"E247"),sQuery(id+"F4.wireOp",EDGE,"E248"),sQuery(id+"F4.wireOp",EDGE,"E249"),sQuery(id+"F4.wireOp",EDGE,"E250"),sQuery(id+"F4.wireOp",EDGE,"E251"),sQuery(id+"F4.wireOp",EDGE,"E252"),sQuery(id+"F4.wireOp",EDGE,"E253"),sQuery(id+"F4.wireOp",EDGE,"E254"),sQuery(id+"F4.wireOp",EDGE,"E255"),sQuery(id+"F4.wireOp",EDGE,"E256"),sQuery(id+"F4.wireOp",EDGE,"E257"),sQuery(id+"F4.wireOp",EDGE,"E258"),sQuery(id+"F4.wireOp",EDGE,"E259"),sQuery(id+"F4.wireOp",EDGE,"E260"),sQuery(id+"F4.wireOp",EDGE,"E261"),sQuery(id+"F4.wireOp",EDGE,"E262"),sQuery(id+"F4.wireOp",EDGE,"E263"),sQuery(id+"F4.wireOp",EDGE,"E264"),sQuery(id+"F4.wireOp",EDGE,"E265"),sQuery(id+"F4.wireOp",EDGE,"E266"),sQuery(id+"F4.wireOp",EDGE,"E267"),sQuery(id+"F4.wireOp",EDGE,"E268"),sQuery(id+"F4.wireOp",EDGE,"E269"),sQuery(id+"F4.wireOp",EDGE,"E270"),sQuery(id+"F4.wireOp",EDGE,"E271"),sQuery(id+"F4.wireOp",EDGE,"E272"),sQuery(id+"F4.wireOp",EDGE,"E273"),sQuery(id+"F4.wireOp",EDGE,"E274"),sQuery(id+"F4.wireOp",EDGE,"E275"),sQuery(id+"F4.wireOp",EDGE,"E276"),sQuery(id+"F4.wireOp",EDGE,"E277"),sQuery(id+"F4.wireOp",EDGE,"E278"),sQuery(id+"F4.wireOp",EDGE,"E279"),sQuery(id+"F4.wireOp",EDGE,"E280"),sQuery(id+"F4.wireOp",EDGE,"E281"),sQuery(id+"F4.wireOp",EDGE,"E282"),sQuery(id+"F4.wireOp",EDGE,"E283"),sQuery(id+"F4.wireOp",EDGE,"E284"),sQuery(id+"F4.wireOp",EDGE,"E285"),sQuery(id+"F4.wireOp",EDGE,"E286"),sQuery(id+"F4.wireOp",EDGE,"E287"),sQuery(id+"F4.wireOp",EDGE,"E288"),sQuery(id+"F4.wireOp",EDGE,"E289"),sQuery(id+"F4.wireOp",EDGE,"E290"),sQuery(id+"F4.wireOp",EDGE,"E291"),sQuery(id+"F4.wireOp",EDGE,"E292"),sQuery(id+"F4.wireOp",EDGE,"E302"),sQuery(id+"F4.wireOp",EDGE,"E303"),sQuery(id+"F4.wireOp",EDGE,"E304"),sQuery(id+"F4.wireOp",EDGE,"E305"),sQuery(id+"F4.wireOp",EDGE,"E306"),sQuery(id+"F4.wireOp",EDGE,"E307"),sQuery(id+"F4.wireOp",EDGE,"E308"),sQuery(id+"F4.wireOp",EDGE,"E309"),sQuery(id+"F4.wireOp",EDGE,"E310"),sQuery(id+"F4.wireOp",EDGE,"E311"),sQuery(id+"F4.wireOp",EDGE,"E312"),sQuery(id+"F4.wireOp",EDGE,"E313"),sQuery(id+"F4.wireOp",EDGE,"E314"),sQuery(id+"F4.wireOp",EDGE,"E315"),sQuery(id+"F4.wireOp",EDGE,"E316"),sQuery(id+"F4.wireOp",EDGE,"E317"),sQuery(id+"F4.wireOp",EDGE,"E318"),sQuery(id+"F4.wireOp",EDGE,"E319"),sQuery(id+"F4.wireOp",EDGE,"E320"),sQuery(id+"F4.wireOp",EDGE,"E321"),sQuery(id+"F4.wireOp",EDGE,"E322"),sQuery(id+"F4.wireOp",EDGE,"E323"),sQuery(id+"F4.wireOp",EDGE,"E324"),sQuery(id+"F4.wireOp",EDGE,"E325"),sQuery(id+"F4.wireOp",EDGE,"E326"),sQuery(id+"F4.wireOp",EDGE,"E327"),sQuery(id+"F4.wireOp",EDGE,"E328"),sQuery(id+"F4.wireOp",EDGE,"E329"),sQuery(id+"F4.wireOp",EDGE,"E330"),sQuery(id+"F4.wireOp",EDGE,"E331"),sQuery(id+"F4.wireOp",EDGE,"E332"),sQuery(id+"F4.wireOp",EDGE,"E333"),sQuery(id+"F4.wireOp",EDGE,"E334"),sQuery(id+"F4.wireOp",EDGE,"E335"),sQuery(id+"F4.wireOp",EDGE,"E336"),sQuery(id+"F4.wireOp",EDGE,"E337"),sQuery(id+"F4.wireOp",EDGE,"E338"),sQuery(id+"F4.wireOp",EDGE,"E339"),sQuery(id+"F4.wireOp",EDGE,"E340"),sQuery(id+"F4.wireOp",EDGE,"E341"),sQuery(id+"F4.wireOp",EDGE,"E342"),sQuery(id+"F4.wireOp",EDGE,"E343"),sQuery(id+"F4.wireOp",EDGE,"E344"),sQuery(id+"F4.wireOp",EDGE,"E345"),sQuery(id+"F4.wireOp",EDGE,"E346"),sQuery(id+"F4.wireOp",EDGE,"E347"),sQuery(id+"F4.wireOp",EDGE,"E348"),sQuery(id+"F4.wireOp",EDGE,"E349"),sQuery(id+"F4.wireOp",EDGE,"E350"),sQuery(id+"F4.wireOp",EDGE,"E351"),sQuery(id+"F4.wireOp",EDGE,"E352"),sQuery(id+"F4.wireOp",EDGE,"E353"),sQuery(id+"F4.wireOp",EDGE,"E354"),sQuery(id+"F4.wireOp",EDGE,"E355"),sQuery(id+"F4.wireOp",EDGE,"E356"),sQuery(id+"F4.wireOp",EDGE,"E357"),sQuery(id+"F4.wireOp",EDGE,"E358"),sQuery(id+"F4.wireOp",EDGE,"E359"),sQuery(id+"F4.wireOp",EDGE,"E360"),sQuery(id+"F4.wireOp",EDGE,"E361"),sQuery(id+"F4.wireOp",EDGE,"E362"),sQuery(id+"F4.wireOp",EDGE,"E363"),sQuery(id+"F4.wireOp",EDGE,"E364"),sQuery(id+"F4.wireOp",EDGE,"E365"),sQuery(id+"F4.wireOp",EDGE,"E366"),sQuery(id+"F4.wireOp",EDGE,"E367"),sQuery(id+"F4.wireOp",EDGE,"E368"),sQuery(id+"F4.wireOp",EDGE,"E369"),sQuery(id+"F4.wireOp",EDGE,"E370"),sQuery(id+"F4.wireOp",EDGE,"E371"),sQuery(id+"F4.wireOp",EDGE,"E372"),sQuery(id+"F4.wireOp",EDGE,"E373"),sQuery(id+"F4.wireOp",EDGE,"E374"),sQuery(id+"F4.wireOp",EDGE,"E375"),sQuery(id+"F4.wireOp",EDGE,"E376"),sQuery(id+"F4.wireOp",EDGE,"E377"),sQuery(id+"F4.wireOp",EDGE,"E378"),sQuery(id+"F4.wireOp",EDGE,"E379"),sQuery(id+"F4.wireOp",EDGE,"E380"),sQuery(id+"F4.wireOp",EDGE,"E381"),sQuery(id+"F4.wireOp",EDGE,"E382"),sQuery(id+"F4.wireOp",EDGE,"E383"),sQuery(id+"F4.wireOp",EDGE,"E384"),sQuery(id+"F4.wireOp",EDGE,"E385"),sQuery(id+"F4.wireOp",EDGE,"E386"),sQuery(id+"F4.wireOp",EDGE,"E387"),sQuery(id+"F4.wireOp",EDGE,"E388"),sQuery(id+"F4.wireOp",EDGE,"E389"),sQuery(id+"F4.wireOp",EDGE,"E390"),sQuery(id+"F4.wireOp",EDGE,"E391"),sQuery(id+"F4.wireOp",EDGE,"E392"),sQuery(id+"F4.wireOp",EDGE,"E393"),sQuery(id+"F4.wireOp",EDGE,"E394"),sQuery(id+"F4.wireOp",EDGE,"E395"),sQuery(id+"F4.wireOp",EDGE,"E396"),sQuery(id+"F4.wireOp",EDGE,"E397"),sQuery(id+"F4.wireOp",EDGE,"E398"),sQuery(id+"F4.wireOp",EDGE,"E399"),sQuery(id+"F4.wireOp",EDGE,"E400"),sQuery(id+"F4.wireOp",EDGE,"E401"),sQuery(id+"F4.wireOp",EDGE,"E402"),sQuery(id+"F4.wireOp",EDGE,"E403"),sQuery(id+"F4.wireOp",EDGE,"E404"),sQuery(id+"F4.wireOp",EDGE,"E405"),sQuery(id+"F4.wireOp",EDGE,"E406"),sQuery(id+"F4.wireOp",EDGE,"E407"),sQuery(id+"F4.wireOp",EDGE,"E408"),sQuery(id+"F4.wireOp",EDGE,"E409"),sQuery(id+"F4.wireOp",EDGE,"E410"),sQuery(id+"F4.wireOp",EDGE,"E411"),sQuery(id+"F4.wireOp",EDGE,"E412"),sQuery(id+"F4.wireOp",EDGE,"E413"),sQuery(id+"F4.wireOp",EDGE,"E414"),sQuery(id+"F4.wireOp",EDGE,"E415"),sQuery(id+"F4.wireOp",EDGE,"E416"),sQuery(id+"F4.wireOp",EDGE,"E417"),sQuery(id+"F4.wireOp",EDGE,"E418"),sQuery(id+"F4.wireOp",EDGE,"E419"),sQuery(id+"F4.wireOp",EDGE,"E420"),sQuery(id+"F4.wireOp",EDGE,"E421"),sQuery(id+"F4.wireOp",EDGE,"E422"),sQuery(id+"F4.wireOp",EDGE,"E423"),sQuery(id+"F4.wireOp",EDGE,"E424"),sQuery(id+"F4.wireOp",EDGE,"E425"),sQuery(id+"F4.wireOp",EDGE,"E426"),sQuery(id+"F4.wireOp",EDGE,"E427")])],"isStart":false});
            var sketch = newSketch(context, id + "F10", { "sketchPlane" : qUnion([Q0])});
            skLineSegment(sketch, "E676", {"start": v(29.5, 13.2) * mm, "end": v(29.66, 13.04) * mm});
            skLineSegment(sketch, "E677", {"start": v(29.66, 13.04) * mm, "end": v(29.75, 12.94) * mm});
            skLineSegment(sketch, "E678", {"start": v(29.75, 12.94) * mm, "end": v(29.98, 12.8) * mm});
            skLineSegment(sketch, "E679", {"start": v(29.98, 12.8) * mm, "end": v(30.36, 12.82) * mm});
            skLineSegment(sketch, "E680", {"start": v(30.36, 12.82) * mm, "end": v(30.64, 12.93) * mm});
            skLineSegment(sketch, "E681", {"start": v(30.64, 12.93) * mm, "end": v(30.92, 13.16) * mm});
            skLineSegment(sketch, "E682", {"start": v(30.92, 13.16) * mm, "end": v(31.22, 13.4) * mm});
            skLineSegment(sketch, "E683", {"start": v(31.22, 13.4) * mm, "end": v(31.38, 13.69) * mm});
            skLineSegment(sketch, "E684", {"start": v(31.38, 13.69) * mm, "end": v(31.59, 13.86) * mm});
            skLineSegment(sketch, "E685", {"start": v(31.59, 13.86) * mm, "end": v(31.82, 13.94) * mm});
            skLineSegment(sketch, "E686", {"start": v(31.82, 13.94) * mm, "end": v(32.06, 13.86) * mm});
            skLineSegment(sketch, "E687", {"start": v(32.06, 13.86) * mm, "end": v(32.26, 13.71) * mm});
            skLineSegment(sketch, "E688", {"start": v(32.26, 13.71) * mm, "end": v(32.6, 13.67) * mm});
            skLineSegment(sketch, "E689", {"start": v(32.6, 13.67) * mm, "end": v(32.9, 13.74) * mm});
            skLineSegment(sketch, "E690", {"start": v(32.9, 13.74) * mm, "end": v(33.1, 13.82) * mm});
            skLineSegment(sketch, "E691", {"start": v(33.1, 13.82) * mm, "end": v(33.26, 13.95) * mm});
            skLineSegment(sketch, "E692", {"start": v(33.26, 13.95) * mm, "end": v(33.39, 14.04) * mm});
            skLineSegment(sketch, "E693", {"start": v(33.39, 14.04) * mm, "end": v(33.48, 14.05) * mm});
            skLineSegment(sketch, "E694", {"start": v(33.48, 14.05) * mm, "end": v(33.64, 13.97) * mm});
            skLineSegment(sketch, "E695", {"start": v(33.64, 13.97) * mm, "end": v(33.76, 13.82) * mm});
            skLineSegment(sketch, "E696", {"start": v(33.76, 13.82) * mm, "end": v(33.96, 13.6) * mm});
            skLineSegment(sketch, "E697", {"start": v(33.96, 13.6) * mm, "end": v(34.27, 13.33) * mm});
            skLineSegment(sketch, "E698", {"start": v(34.27, 13.33) * mm, "end": v(34.4, 13.26) * mm});
            skLineSegment(sketch, "E699", {"start": v(34.4, 13.26) * mm, "end": v(34.58, 13.24) * mm});
            skLineSegment(sketch, "E700", {"start": v(34.58, 13.24) * mm, "end": v(34.82, 13.3) * mm});
            skLineSegment(sketch, "E701", {"start": v(34.82, 13.3) * mm, "end": v(35.06, 13.35) * mm});
            skLineSegment(sketch, "E702", {"start": v(35.06, 13.35) * mm, "end": v(35.3, 13.42) * mm});
            skLineSegment(sketch, "E703", {"start": v(35.3, 13.42) * mm, "end": v(35.66, 13.4) * mm});
            skLineSegment(sketch, "E704", {"start": v(35.66, 13.4) * mm, "end": v(35.82, 13.36) * mm});
            skLineSegment(sketch, "E705", {"start": v(35.82, 13.36) * mm, "end": v(36.03, 13.29) * mm});
            skLineSegment(sketch, "E706", {"start": v(36.03, 13.29) * mm, "end": v(36.15, 13.13) * mm});
            skLineSegment(sketch, "E707", {"start": v(36.15, 13.13) * mm, "end": v(36.14, 12.88) * mm});
            skLineSegment(sketch, "E708", {"start": v(36.14, 12.88) * mm, "end": v(36.07, 12.6) * mm});
            skLineSegment(sketch, "E709", {"start": v(36.07, 12.6) * mm, "end": v(35.94, 12.42) * mm});
            skLineSegment(sketch, "E710", {"start": v(35.94, 12.42) * mm, "end": v(35.74, 12.23) * mm});
            skLineSegment(sketch, "E711", {"start": v(35.74, 12.23) * mm, "end": v(35.68, 12.14) * mm});
            skLineSegment(sketch, "E712", {"start": v(35.68, 12.14) * mm, "end": v(35.75, 12.04) * mm});
            skLineSegment(sketch, "E713", {"start": v(35.75, 12.04) * mm, "end": v(35.9, 11.93) * mm});
            skLineSegment(sketch, "E714", {"start": v(35.9, 11.93) * mm, "end": v(36.1, 11.77) * mm});
            skLineSegment(sketch, "E715", {"start": v(36.1, 11.77) * mm, "end": v(36.28, 11.55) * mm});
            skLineSegment(sketch, "E716", {"start": v(36.28, 11.55) * mm, "end": v(36.46, 11.25) * mm});
            skLineSegment(sketch, "E717", {"start": v(36.46, 11.25) * mm, "end": v(36.64, 10.88) * mm});
            skLineSegment(sketch, "E718", {"start": v(36.64, 10.88) * mm, "end": v(36.74, 10.6) * mm});
            skLineSegment(sketch, "E719", {"start": v(36.74, 10.6) * mm, "end": v(36.8, 10.42) * mm});
            skLineSegment(sketch, "E720", {"start": v(36.8, 10.42) * mm, "end": v(36.92, 10.46) * mm});
            skLineSegment(sketch, "E721", {"start": v(36.92, 10.46) * mm, "end": v(36.99, 10.6) * mm});
            skLineSegment(sketch, "E722", {"start": v(36.99, 10.6) * mm, "end": v(37.15, 11.05) * mm});
            skLineSegment(sketch, "E723", {"start": v(37.15, 11.05) * mm, "end": v(37.22, 11.57) * mm});
            skLineSegment(sketch, "E724", {"start": v(37.22, 11.57) * mm, "end": v(37.3, 11.98) * mm});
            skLineSegment(sketch, "E725", {"start": v(37.3, 11.98) * mm, "end": v(37.35, 12.12) * mm});
            skLineSegment(sketch, "E726", {"start": v(37.35, 12.12) * mm, "end": v(37.32, 12.43) * mm});
            skLineSegment(sketch, "E727", {"start": v(37.32, 12.43) * mm, "end": v(37.28, 12.83) * mm});
            skLineSegment(sketch, "E728", {"start": v(37.28, 12.83) * mm, "end": v(37.17, 13.2) * mm});
            skLineSegment(sketch, "E729", {"start": v(37.17, 13.2) * mm, "end": v(37, 13.47) * mm});
            skLineSegment(sketch, "E730", {"start": v(37, 13.47) * mm, "end": v(36.8, 13.69) * mm});
            skLineSegment(sketch, "E731", {"start": v(36.8, 13.69) * mm, "end": v(36.67, 13.76) * mm});
            skLineSegment(sketch, "E732", {"start": v(36.67, 13.76) * mm, "end": v(36.26, 14.2) * mm});
            skLineSegment(sketch, "E733", {"start": v(36.26, 14.2) * mm, "end": v(36.05, 14.45) * mm});
            skLineSegment(sketch, "E734", {"start": v(36.05, 14.45) * mm, "end": v(35.82, 14.7) * mm});
            skLineSegment(sketch, "E735", {"start": v(35.52, 15.11) * mm, "end": v(35.32, 15.31) * mm});
            skLineSegment(sketch, "E736", {"start": v(35.32, 15.31) * mm, "end": v(34.9, 15.34) * mm});
            skLineSegment(sketch, "E737", {"start": v(34.9, 15.34) * mm, "end": v(34.71, 15.38) * mm});
            skLineSegment(sketch, "E738", {"start": v(34.71, 15.38) * mm, "end": v(34.44, 15.57) * mm});
            skLineSegment(sketch, "E739", {"start": v(34.44, 15.57) * mm, "end": v(34.3, 15.72) * mm});
            skLineSegment(sketch, "E740", {"start": v(34.3, 15.72) * mm, "end": v(34.13, 15.85) * mm});
            skLineSegment(sketch, "E741", {"start": v(34.13, 15.85) * mm, "end": v(33.94, 15.94) * mm});
            skLineSegment(sketch, "E742", {"start": v(33.94, 15.94) * mm, "end": v(33.76, 16) * mm});
            skLineSegment(sketch, "E743", {"start": v(33.76, 16) * mm, "end": v(33.62, 15.99) * mm});
            skLineSegment(sketch, "E744", {"start": v(33.62, 15.99) * mm, "end": v(33.48, 15.93) * mm});
            skLineSegment(sketch, "E745", {"start": v(35.82, 14.7) * mm, "end": v(35.75, 14.8) * mm});
            skLineSegment(sketch, "E746", {"start": v(35.75, 14.8) * mm, "end": v(35.68, 14.89) * mm});
            skLineSegment(sketch, "E747", {"start": v(35.68, 14.89) * mm, "end": v(35.6, 15) * mm});
            skLineSegment(sketch, "E748", {"start": v(35.6, 15) * mm, "end": v(35.54, 15.08) * mm});
            skLineSegment(sketch, "E749", {"start": v(35.54, 15.08) * mm, "end": v(35.4, 15.23) * mm});
            skLineSegment(sketch, "E750", {"start": v(35.4, 15.23) * mm, "end": v(35.32, 15.31) * mm});
            skLineSegment(sketch, "E751", {"start": v(35.32, 15.31) * mm, "end": v(35.2, 15.34) * mm});
            skLineSegment(sketch, "E752", {"start": v(35.2, 15.34) * mm, "end": v(35.02, 15.35) * mm});
            skLineSegment(sketch, "E753", {"start": v(35.02, 15.35) * mm, "end": v(34.76, 15.38) * mm});
            skLineSegment(sketch, "E754", {"start": v(34.76, 15.38) * mm, "end": v(34.67, 15.43) * mm});
            skLineSegment(sketch, "E755", {"start": v(34.67, 15.43) * mm, "end": v(34.45, 15.59) * mm});
            skLineSegment(sketch, "E756", {"start": v(34.45, 15.59) * mm, "end": v(34.2, 15.82) * mm});
            skLineSegment(sketch, "E757", {"start": v(34.2, 15.82) * mm, "end": v(34, 15.91) * mm});
            skLineSegment(sketch, "E758", {"start": v(34, 15.91) * mm, "end": v(33.85, 15.97) * mm});
            skLineSegment(sketch, "E759", {"start": v(33.85, 15.97) * mm, "end": v(33.75, 16) * mm});
            skLineSegment(sketch, "E760", {"start": v(33.75, 16) * mm, "end": v(33.57, 15.97) * mm});
            skLineSegment(sketch, "E761", {"start": v(33.57, 15.97) * mm, "end": v(33.46, 15.92) * mm});
            skLineSegment(sketch, "E762", {"start": v(33.46, 15.92) * mm, "end": v(33.24, 15.73) * mm});
            skLineSegment(sketch, "E763", {"start": v(33.24, 15.73) * mm, "end": v(33.14, 15.64) * mm});
            skLineSegment(sketch, "E764", {"start": v(33.14, 15.64) * mm, "end": v(33.04, 15.54) * mm});
            skLineSegment(sketch, "E765", {"start": v(33.04, 15.54) * mm, "end": v(32.92, 15.41) * mm});
            skLineSegment(sketch, "E766", {"start": v(32.92, 15.41) * mm, "end": v(32.8, 15.26) * mm});
            skLineSegment(sketch, "E767", {"start": v(32.8, 15.26) * mm, "end": v(32.72, 15.18) * mm});
            skLineSegment(sketch, "E768", {"start": v(32.72, 15.18) * mm, "end": v(32.63, 15.13) * mm});
            skLineSegment(sketch, "E769", {"start": v(32.63, 15.13) * mm, "end": v(32.5, 15.12) * mm});
            skLineSegment(sketch, "E770", {"start": v(32.5, 15.12) * mm, "end": v(32.43, 15.16) * mm});
            skLineSegment(sketch, "E771", {"start": v(32.43, 15.16) * mm, "end": v(32.34, 15.22) * mm});
            skLineSegment(sketch, "E772", {"start": v(32.34, 15.22) * mm, "end": v(32.2, 15.29) * mm});
            skLineSegment(sketch, "E773", {"start": v(32.2, 15.29) * mm, "end": v(32.03, 15.3) * mm});
            skLineSegment(sketch, "E774", {"start": v(32.03, 15.3) * mm, "end": v(31.83, 15.22) * mm});
            skLineSegment(sketch, "E775", {"start": v(31.83, 15.22) * mm, "end": v(31.52, 15.03) * mm});
            skLineSegment(sketch, "E776", {"start": v(31.52, 15.03) * mm, "end": v(31.37, 14.9) * mm});
            skLineSegment(sketch, "E777", {"start": v(31.37, 14.9) * mm, "end": v(31.1, 14.69) * mm});
            skLineSegment(sketch, "E778", {"start": v(31.1, 14.69) * mm, "end": v(30.98, 14.57) * mm});
            skLineSegment(sketch, "E779", {"start": v(30.98, 14.57) * mm, "end": v(30.88, 14.49) * mm});
            skLineSegment(sketch, "E780", {"start": v(30.88, 14.49) * mm, "end": v(30.73, 14.4) * mm});
            skLineSegment(sketch, "E781", {"start": v(30.73, 14.4) * mm, "end": v(30.56, 14.32) * mm});
            skLineSegment(sketch, "E782", {"start": v(30.56, 14.32) * mm, "end": v(30.42, 14.28) * mm});
            skLineSegment(sketch, "E783", {"start": v(30.42, 14.28) * mm, "end": v(30.3, 14.29) * mm});
            skLineSegment(sketch, "E784", {"start": v(30.3, 14.29) * mm, "end": v(30.19, 14.32) * mm});
            skLineSegment(sketch, "E785", {"start": v(30.19, 14.32) * mm, "end": v(30.1, 14.4) * mm});
            skLineSegment(sketch, "E786", {"start": v(30.1, 14.4) * mm, "end": v(30.03, 14.49) * mm});
            skLineSegment(sketch, "E787", {"start": v(30.03, 14.49) * mm, "end": v(30, 14.64) * mm});
            skLineSegment(sketch, "E788", {"start": v(30, 14.64) * mm, "end": v(30, 14.77) * mm});
            skLineSegment(sketch, "E789", {"start": v(30, 14.77) * mm, "end": v(30, 14.92) * mm});
            skLineSegment(sketch, "E790", {"start": v(30, 14.92) * mm, "end": v(29.98, 14.94) * mm});
            skLineSegment(sketch, "E791", {"start": v(29.98, 14.94) * mm, "end": v(29.94, 14.93) * mm});
            skLineSegment(sketch, "E792", {"start": v(29.94, 14.93) * mm, "end": v(29.86, 14.87) * mm});
            skLineSegment(sketch, "E793", {"start": v(29.86, 14.87) * mm, "end": v(29.75, 14.77) * mm});
            skLineSegment(sketch, "E794", {"start": v(29.75, 14.77) * mm, "end": v(29.6, 14.54) * mm});
            skLineSegment(sketch, "E795", {"start": v(29.6, 14.54) * mm, "end": v(29.52, 14.35) * mm});
            skLineSegment(sketch, "E796", {"start": v(29.52, 14.35) * mm, "end": v(29.45, 14.07) * mm});
            skLineSegment(sketch, "E797", {"start": v(29.45, 14.07) * mm, "end": v(29.43, 13.73) * mm});
            skLineSegment(sketch, "E798", {"start": v(29.43, 13.73) * mm, "end": v(29.45, 13.44) * mm});
            skLineSegment(sketch, "E799", {"start": v(29.45, 13.44) * mm, "end": v(29.5, 13.2) * mm});
            skLineSegment(sketch, "E800", {"start": v(29.5, 13.2) * mm, "end": v(29.5, 13.2) * mm});
            skLineSegment(sketch, "E801", {"start": v(29.5, 13.2) * mm, "end": v(29.48, 13.17) * mm});
            skLineSegment(sketch, "E802", {"start": v(29.48, 13.17) * mm, "end": v(29.46, 13.14) * mm});
            skLineSegment(sketch, "E803", {"start": v(29.46, 13.14) * mm, "end": v(29.41, 13.1) * mm});
            skLineSegment(sketch, "E804", {"start": v(29.41, 13.1) * mm, "end": v(29.34, 13) * mm});
            skLineSegment(sketch, "E805", {"start": v(29.34, 13) * mm, "end": v(29.33, 12.96) * mm});
            skLineSegment(sketch, "E806", {"start": v(29.33, 12.96) * mm, "end": v(29.31, 12.9) * mm});
            skLineSegment(sketch, "E807", {"start": v(29.31, 12.9) * mm, "end": v(29.27, 12.8) * mm});
            skLineSegment(sketch, "E808", {"start": v(29.27, 12.8) * mm, "end": v(29.27, 12.68) * mm});
            skLineSegment(sketch, "E809", {"start": v(29.27, 12.68) * mm, "end": v(29.28, 12.5) * mm});
            skLineSegment(sketch, "E810", {"start": v(29.28, 12.5) * mm, "end": v(29.31, 12.36) * mm});
            skLineSegment(sketch, "E811", {"start": v(29.31, 12.36) * mm, "end": v(29.35, 12.22) * mm});
            skLineSegment(sketch, "E812", {"start": v(29.35, 12.22) * mm, "end": v(29.4, 12.07) * mm});
            skLineSegment(sketch, "E813", {"start": v(29.4, 12.07) * mm, "end": v(29.48, 11.95) * mm});
            skLineSegment(sketch, "E814", {"start": v(29.48, 11.95) * mm, "end": v(29.56, 11.9) * mm});
            skLineSegment(sketch, "E815", {"start": v(29.56, 11.9) * mm, "end": v(29.64, 11.87) * mm});
            skLineSegment(sketch, "E816", {"start": v(29.64, 11.87) * mm, "end": v(29.7, 11.94) * mm});
            skLineSegment(sketch, "E817", {"start": v(29.7, 11.94) * mm, "end": v(29.84, 12.18) * mm});
            skLineSegment(sketch, "E818", {"start": v(29.84, 12.18) * mm, "end": v(29.91, 12.33) * mm});
            skLineSegment(sketch, "E819", {"start": v(29.91, 12.33) * mm, "end": v(30.01, 12.47) * mm});
            skLineSegment(sketch, "E820", {"start": v(30.01, 12.47) * mm, "end": v(30.1, 12.6) * mm});
            skLineSegment(sketch, "E821", {"start": v(30.1, 12.6) * mm, "end": v(30.18, 12.72) * mm});
            skLineSegment(sketch, "E822", {"start": v(30.18, 12.72) * mm, "end": v(30.28, 12.8) * mm});
            skLineSegment(sketch, "E823", {"start": v(30.28, 12.8) * mm, "end": v(30.36, 12.82) * mm});
            skLineSegment(sketch, "E824", {"start": v(33.48, 12.54) * mm, "end": v(33.57, 12.53) * mm});
            skLineSegment(sketch, "E825", {"start": v(33.57, 12.53) * mm, "end": v(33.65, 12.49) * mm});
            skLineSegment(sketch, "E826", {"start": v(33.65, 12.49) * mm, "end": v(33.72, 12.44) * mm});
            skLineSegment(sketch, "E827", {"start": v(33.72, 12.44) * mm, "end": v(33.8, 12.37) * mm});
            skLineSegment(sketch, "E828", {"start": v(33.8, 12.37) * mm, "end": v(33.89, 12.27) * mm});
            skLineSegment(sketch, "E829", {"start": v(33.89, 12.27) * mm, "end": v(33.96, 12.18) * mm});
            skLineSegment(sketch, "E830", {"start": v(33.96, 12.18) * mm, "end": v(34.05, 12.1) * mm});
            skLineSegment(sketch, "E831", {"start": v(34.05, 12.1) * mm, "end": v(34.1, 12.1) * mm});
            skLineSegment(sketch, "E832", {"start": v(34.1, 12.1) * mm, "end": v(34.1, 12.16) * mm});
            skLineSegment(sketch, "E833", {"start": v(34.1, 12.16) * mm, "end": v(34.07, 12.25) * mm});
            skLineSegment(sketch, "E834", {"start": v(34.07, 12.25) * mm, "end": v(34, 12.35) * mm});
            skLineSegment(sketch, "E835", {"start": v(34, 12.35) * mm, "end": v(33.9, 12.46) * mm});
            skLineSegment(sketch, "E836", {"start": v(33.9, 12.46) * mm, "end": v(33.83, 12.56) * mm});
            skLineSegment(sketch, "E837", {"start": v(33.83, 12.56) * mm, "end": v(33.74, 12.64) * mm});
            skLineSegment(sketch, "E838", {"start": v(33.74, 12.64) * mm, "end": v(33.69, 12.66) * mm});
            skLineSegment(sketch, "E839", {"start": v(33.69, 12.66) * mm, "end": v(33.6, 12.67) * mm});
            skLineSegment(sketch, "E840", {"start": v(33.6, 12.67) * mm, "end": v(33.53, 12.64) * mm});
            skLineSegment(sketch, "E841", {"start": v(33.53, 12.64) * mm, "end": v(33.46, 12.56) * mm});
            skLineSegment(sketch, "E842", {"start": v(33.46, 12.56) * mm, "end": v(33.48, 12.54) * mm});
            skLineSegment(sketch, "E843", {"start": v(30.65, 12.44) * mm, "end": v(30.69, 12.47) * mm});
            skLineSegment(sketch, "E844", {"start": v(30.69, 12.47) * mm, "end": v(30.72, 12.5) * mm});
            skLineSegment(sketch, "E845", {"start": v(30.72, 12.5) * mm, "end": v(30.77, 12.51) * mm});
            skLineSegment(sketch, "E846", {"start": v(30.77, 12.51) * mm, "end": v(30.8, 12.5) * mm});
            skLineSegment(sketch, "E847", {"start": v(30.8, 12.5) * mm, "end": v(30.83, 12.49) * mm});
            skLineSegment(sketch, "E848", {"start": v(30.83, 12.49) * mm, "end": v(30.87, 12.48) * mm});
            skLineSegment(sketch, "E849", {"start": v(30.87, 12.48) * mm, "end": v(30.9, 12.47) * mm});
            skLineSegment(sketch, "E850", {"start": v(30.9, 12.47) * mm, "end": v(30.92, 12.49) * mm});
            skLineSegment(sketch, "E851", {"start": v(30.92, 12.49) * mm, "end": v(30.93, 12.53) * mm});
            skLineSegment(sketch, "E852", {"start": v(30.93, 12.53) * mm, "end": v(30.93, 12.56) * mm});
            skLineSegment(sketch, "E853", {"start": v(30.93, 12.56) * mm, "end": v(30.9, 12.57) * mm});
            skLineSegment(sketch, "E854", {"start": v(30.9, 12.57) * mm, "end": v(30.88, 12.6) * mm});
            skLineSegment(sketch, "E855", {"start": v(30.88, 12.6) * mm, "end": v(30.86, 12.61) * mm});
            skLineSegment(sketch, "E856", {"start": v(30.86, 12.61) * mm, "end": v(30.85, 12.65) * mm});
            skLineSegment(sketch, "E857", {"start": v(30.85, 12.65) * mm, "end": v(30.82, 12.66) * mm});
            skLineSegment(sketch, "E858", {"start": v(30.82, 12.66) * mm, "end": v(30.8, 12.66) * mm});
            skLineSegment(sketch, "E859", {"start": v(30.8, 12.66) * mm, "end": v(30.76, 12.66) * mm});
            skLineSegment(sketch, "E860", {"start": v(30.76, 12.66) * mm, "end": v(30.74, 12.64) * mm});
            skLineSegment(sketch, "E861", {"start": v(30.74, 12.64) * mm, "end": v(30.72, 12.62) * mm});
            skLineSegment(sketch, "E862", {"start": v(30.72, 12.62) * mm, "end": v(30.67, 12.6) * mm});
            skLineSegment(sketch, "E863", {"start": v(30.67, 12.6) * mm, "end": v(30.63, 12.56) * mm});
            skLineSegment(sketch, "E864", {"start": v(30.63, 12.56) * mm, "end": v(30.6, 12.53) * mm});
            skLineSegment(sketch, "E865", {"start": v(30.6, 12.53) * mm, "end": v(30.54, 12.5) * mm});
            skLineSegment(sketch, "E866", {"start": v(30.54, 12.5) * mm, "end": v(30.52, 12.47) * mm});
            skLineSegment(sketch, "E867", {"start": v(30.52, 12.47) * mm, "end": v(30.47, 12.44) * mm});
            skLineSegment(sketch, "E868", {"start": v(30.47, 12.44) * mm, "end": v(30.45, 12.4) * mm});
            skLineSegment(sketch, "E869", {"start": v(30.45, 12.4) * mm, "end": v(30.47, 12.38) * mm});
            skLineSegment(sketch, "E870", {"start": v(30.47, 12.38) * mm, "end": v(30.5, 12.36) * mm});
            skLineSegment(sketch, "E871", {"start": v(30.5, 12.36) * mm, "end": v(30.55, 12.38) * mm});
            skLineSegment(sketch, "E872", {"start": v(30.55, 12.38) * mm, "end": v(30.6, 12.4) * mm});
            skLineSegment(sketch, "E873", {"start": v(30.6, 12.4) * mm, "end": v(30.62, 12.42) * mm});
            skLineSegment(sketch, "E874", {"start": v(30.62, 12.42) * mm, "end": v(30.65, 12.44) * mm});
            skLineSegment(sketch, "E875", {"start": v(30.82, 12.66) * mm, "end": v(30.82, 12.66) * mm});
            skSolve(sketch);
        }
        {
            var Q0;
            Q0 = qSketchRegion(id + "F10", true);
            extrude(context, id + "F11", {"entities" : qUnion([Q0]), "operationType" : NewBodyOperationType.ADD, "depth" : 0.25 * mm, "offsetDistance" : 25.4 * mm});
        }
        {
            var Q0;
            Q0=makeQuery(id+"F11.opExtrude","CAP_FACE",FACE,{"disambiguationData":[OSD([sQuery(id+"F10.wireOp",EDGE,"E680"),sQuery(id+"F10.wireOp",EDGE,"E681"),sQuery(id+"F10.wireOp",EDGE,"E682"),sQuery(id+"F10.wireOp",EDGE,"E683"),sQuery(id+"F10.wireOp",EDGE,"E684"),sQuery(id+"F10.wireOp",EDGE,"E685"),sQuery(id+"F10.wireOp",EDGE,"E686"),sQuery(id+"F10.wireOp",EDGE,"E687"),sQuery(id+"F10.wireOp",EDGE,"E688"),sQuery(id+"F10.wireOp",EDGE,"E689"),sQuery(id+"F10.wireOp",EDGE,"E690"),sQuery(id+"F10.wireOp",EDGE,"E691"),sQuery(id+"F10.wireOp",EDGE,"E692"),sQuery(id+"F10.wireOp",EDGE,"E693"),sQuery(id+"F10.wireOp",EDGE,"E694"),sQuery(id+"F10.wireOp",EDGE,"E695"),sQuery(id+"F10.wireOp",EDGE,"E696"),sQuery(id+"F10.wireOp",EDGE,"E697"),sQuery(id+"F10.wireOp",EDGE,"E698"),sQuery(id+"F10.wireOp",EDGE,"E699"),sQuery(id+"F10.wireOp",EDGE,"E700"),sQuery(id+"F10.wireOp",EDGE,"E701"),sQuery(id+"F10.wireOp",EDGE,"E702"),sQuery(id+"F10.wireOp",EDGE,"E703"),sQuery(id+"F10.wireOp",EDGE,"E704"),sQuery(id+"F10.wireOp",EDGE,"E705"),sQuery(id+"F10.wireOp",EDGE,"E706"),sQuery(id+"F10.wireOp",EDGE,"E707"),sQuery(id+"F10.wireOp",EDGE,"E708"),sQuery(id+"F10.wireOp",EDGE,"E709"),sQuery(id+"F10.wireOp",EDGE,"E710"),sQuery(id+"F10.wireOp",EDGE,"E711"),sQuery(id+"F10.wireOp",EDGE,"E712"),sQuery(id+"F10.wireOp",EDGE,"E713"),sQuery(id+"F10.wireOp",EDGE,"E714"),sQuery(id+"F10.wireOp",EDGE,"E715"),sQuery(id+"F10.wireOp",EDGE,"E716"),sQuery(id+"F10.wireOp",EDGE,"E717"),sQuery(id+"F10.wireOp",EDGE,"E718"),sQuery(id+"F10.wireOp",EDGE,"E719"),sQuery(id+"F10.wireOp",EDGE,"E720"),sQuery(id+"F10.wireOp",EDGE,"E721"),sQuery(id+"F10.wireOp",EDGE,"E722"),sQuery(id+"F10.wireOp",EDGE,"E723"),sQuery(id+"F10.wireOp",EDGE,"E724"),sQuery(id+"F10.wireOp",EDGE,"E725"),sQuery(id+"F10.wireOp",EDGE,"E726"),sQuery(id+"F10.wireOp",EDGE,"E727"),sQuery(id+"F10.wireOp",EDGE,"E728"),sQuery(id+"F10.wireOp",EDGE,"E729"),sQuery(id+"F10.wireOp",EDGE,"E730"),sQuery(id+"F10.wireOp",EDGE,"E731"),sQuery(id+"F10.wireOp",EDGE,"E732"),sQuery(id+"F10.wireOp",EDGE,"E733"),sQuery(id+"F10.wireOp",EDGE,"E734"),sQuery(id+"F10.wireOp",EDGE,"E741"),sQuery(id+"F10.wireOp",EDGE,"E742"),sQuery(id+"F10.wireOp",EDGE,"E743"),sQuery(id+"F10.wireOp",EDGE,"E744"),sQuery(id+"F10.wireOp",EDGE,"E745"),sQuery(id+"F10.wireOp",EDGE,"E746"),sQuery(id+"F10.wireOp",EDGE,"E747"),sQuery(id+"F10.wireOp",EDGE,"E748"),sQuery(id+"F10.wireOp",EDGE,"E749"),sQuery(id+"F10.wireOp",EDGE,"E750"),sQuery(id+"F10.wireOp",EDGE,"E751"),sQuery(id+"F10.wireOp",EDGE,"E752"),sQuery(id+"F10.wireOp",EDGE,"E753"),sQuery(id+"F10.wireOp",EDGE,"E754"),sQuery(id+"F10.wireOp",EDGE,"E755"),sQuery(id+"F10.wireOp",EDGE,"E756"),sQuery(id+"F10.wireOp",EDGE,"E757"),sQuery(id+"F10.wireOp",EDGE,"E758"),sQuery(id+"F10.wireOp",EDGE,"E759"),sQuery(id+"F10.wireOp",EDGE,"E760"),sQuery(id+"F10.wireOp",EDGE,"E761"),sQuery(id+"F10.wireOp",EDGE,"E762"),sQuery(id+"F10.wireOp",EDGE,"E763"),sQuery(id+"F10.wireOp",EDGE,"E764"),sQuery(id+"F10.wireOp",EDGE,"E765"),sQuery(id+"F10.wireOp",EDGE,"E766"),sQuery(id+"F10.wireOp",EDGE,"E767"),sQuery(id+"F10.wireOp",EDGE,"E768"),sQuery(id+"F10.wireOp",EDGE,"E769"),sQuery(id+"F10.wireOp",EDGE,"E770"),sQuery(id+"F10.wireOp",EDGE,"E771"),sQuery(id+"F10.wireOp",EDGE,"E772"),sQuery(id+"F10.wireOp",EDGE,"E773"),sQuery(id+"F10.wireOp",EDGE,"E774"),sQuery(id+"F10.wireOp",EDGE,"E775"),sQuery(id+"F10.wireOp",EDGE,"E776"),sQuery(id+"F10.wireOp",EDGE,"E777"),sQuery(id+"F10.wireOp",EDGE,"E778"),sQuery(id+"F10.wireOp",EDGE,"E779"),sQuery(id+"F10.wireOp",EDGE,"E780"),sQuery(id+"F10.wireOp",EDGE,"E781"),sQuery(id+"F10.wireOp",EDGE,"E782"),sQuery(id+"F10.wireOp",EDGE,"E783"),sQuery(id+"F10.wireOp",EDGE,"E784"),sQuery(id+"F10.wireOp",EDGE,"E785"),sQuery(id+"F10.wireOp",EDGE,"E786"),sQuery(id+"F10.wireOp",EDGE,"E787"),sQuery(id+"F10.wireOp",EDGE,"E788"),sQuery(id+"F10.wireOp",EDGE,"E789"),sQuery(id+"F10.wireOp",EDGE,"E790"),sQuery(id+"F10.wireOp",EDGE,"E791"),sQuery(id+"F10.wireOp",EDGE,"E792"),sQuery(id+"F10.wireOp",EDGE,"E793"),sQuery(id+"F10.wireOp",EDGE,"E794"),sQuery(id+"F10.wireOp",EDGE,"E795"),sQuery(id+"F10.wireOp",EDGE,"E796"),sQuery(id+"F10.wireOp",EDGE,"E797"),sQuery(id+"F10.wireOp",EDGE,"E798"),sQuery(id+"F10.wireOp",EDGE,"E799"),sQuery(id+"F10.wireOp",EDGE,"E800"),sQuery(id+"F10.wireOp",EDGE,"E801"),sQuery(id+"F10.wireOp",EDGE,"E802"),sQuery(id+"F10.wireOp",EDGE,"E803"),sQuery(id+"F10.wireOp",EDGE,"E804"),sQuery(id+"F10.wireOp",EDGE,"E805"),sQuery(id+"F10.wireOp",EDGE,"E806"),sQuery(id+"F10.wireOp",EDGE,"E807"),sQuery(id+"F10.wireOp",EDGE,"E808"),sQuery(id+"F10.wireOp",EDGE,"E809"),sQuery(id+"F10.wireOp",EDGE,"E810"),sQuery(id+"F10.wireOp",EDGE,"E811"),sQuery(id+"F10.wireOp",EDGE,"E812"),sQuery(id+"F10.wireOp",EDGE,"E813"),sQuery(id+"F10.wireOp",EDGE,"E814"),sQuery(id+"F10.wireOp",EDGE,"E815"),sQuery(id+"F10.wireOp",EDGE,"E816"),sQuery(id+"F10.wireOp",EDGE,"E817"),sQuery(id+"F10.wireOp",EDGE,"E818"),sQuery(id+"F10.wireOp",EDGE,"E819"),sQuery(id+"F10.wireOp",EDGE,"E820"),sQuery(id+"F10.wireOp",EDGE,"E821"),sQuery(id+"F10.wireOp",EDGE,"E822"),sQuery(id+"F10.wireOp",EDGE,"E823")])],"isStart":false});
            var sketch = newSketch(context, id + "F12", { "sketchPlane" : qUnion([Q0])});
            skLineSegment(sketch, "E876", {"start": v(29.68, 13.1) * mm, "end": v(29.8, 12.97) * mm});
            skLineSegment(sketch, "E877", {"start": v(29.8, 12.97) * mm, "end": v(29.98, 12.85) * mm});
            skLineSegment(sketch, "E878", {"start": v(29.98, 12.85) * mm, "end": v(30.2, 12.74) * mm});
            skLineSegment(sketch, "E879", {"start": v(30.2, 12.74) * mm, "end": v(30.09, 12.57) * mm});
            skLineSegment(sketch, "E880", {"start": v(29.4, 12.03) * mm, "end": v(29.36, 12.15) * mm});
            skLineSegment(sketch, "E881", {"start": v(29.36, 12.15) * mm, "end": v(29.3, 12.33) * mm});
            skLineSegment(sketch, "E882", {"start": v(29.3, 12.33) * mm, "end": v(29.26, 12.54) * mm});
            skLineSegment(sketch, "E883", {"start": v(29.26, 12.54) * mm, "end": v(29.27, 12.81) * mm});
            skLineSegment(sketch, "E884", {"start": v(29.38, 13.05) * mm, "end": v(29.44, 13.12) * mm});
            skLineSegment(sketch, "E885", {"start": v(29.44, 13.12) * mm, "end": v(29.5, 13.2) * mm});
            skLineSegment(sketch, "E886", {"start": v(29.4, 12.03) * mm, "end": v(29.44, 12) * mm});
            skLineSegment(sketch, "E887", {"start": v(29.44, 12) * mm, "end": v(29.49, 11.93) * mm});
            skLineSegment(sketch, "E888", {"start": v(29.49, 11.93) * mm, "end": v(29.55, 11.88) * mm});
            skLineSegment(sketch, "E889", {"start": v(29.55, 11.88) * mm, "end": v(29.64, 11.87) * mm});
            skLineSegment(sketch, "E890", {"start": v(29.64, 11.87) * mm, "end": v(29.66, 11.89) * mm});
            skLineSegment(sketch, "E891", {"start": v(29.66, 11.89) * mm, "end": v(29.7, 11.93) * mm});
            skLineSegment(sketch, "E892", {"start": v(29.7, 11.93) * mm, "end": v(29.73, 11.99) * mm});
            skLineSegment(sketch, "E893", {"start": v(29.73, 11.99) * mm, "end": v(29.77, 12.05) * mm});
            skLineSegment(sketch, "E894", {"start": v(29.77, 12.05) * mm, "end": v(29.8, 12.11) * mm});
            skLineSegment(sketch, "E895", {"start": v(29.8, 12.11) * mm, "end": v(29.82, 12.16) * mm});
            skLineSegment(sketch, "E896", {"start": v(29.34, 13) * mm, "end": v(29.38, 13.05) * mm});
            skLineSegment(sketch, "E897", {"start": v(29.38, 13.05) * mm, "end": v(29.42, 13.1) * mm});
            skLineSegment(sketch, "E898", {"start": v(29.42, 13.1) * mm, "end": v(29.44, 13.14) * mm});
            skLineSegment(sketch, "E899", {"start": v(29.44, 13.14) * mm, "end": v(29.47, 13.17) * mm});
            skLineSegment(sketch, "E900", {"start": v(29.47, 13.17) * mm, "end": v(29.48, 13.19) * mm});
            skLineSegment(sketch, "E901", {"start": v(29.48, 13.19) * mm, "end": v(29.5, 13.19) * mm});
            skLineSegment(sketch, "E902", {"start": v(29.5, 13.19) * mm, "end": v(29.56, 13.17) * mm});
            skLineSegment(sketch, "E903", {"start": v(29.56, 13.17) * mm, "end": v(29.6, 13.15) * mm});
            skLineSegment(sketch, "E904", {"start": v(29.6, 13.15) * mm, "end": v(29.64, 13.13) * mm});
            skLineSegment(sketch, "E905", {"start": v(29.64, 13.13) * mm, "end": v(29.68, 13.1) * mm});
            skLineSegment(sketch, "E906", {"start": v(30.09, 12.57) * mm, "end": v(30.03, 12.47) * mm});
            skLineSegment(sketch, "E907", {"start": v(30.03, 12.47) * mm, "end": v(29.94, 12.34) * mm});
            skLineSegment(sketch, "E908", {"start": v(29.94, 12.34) * mm, "end": v(29.86, 12.2) * mm});
            skLineSegment(sketch, "E909", {"start": v(29.86, 12.2) * mm, "end": v(29.82, 12.13) * mm});
            skLineSegment(sketch, "E910", {"start": v(29.82, 12.13) * mm, "end": v(29.78, 12.05) * mm});
            skLineSegment(sketch, "E911", {"start": v(29.78, 12.05) * mm, "end": v(29.73, 11.99) * mm});
            skLineSegment(sketch, "E912", {"start": v(29.34, 13) * mm, "end": v(29.32, 12.95) * mm});
            skLineSegment(sketch, "E913", {"start": v(29.32, 12.95) * mm, "end": v(29.29, 12.87) * mm});
            skLineSegment(sketch, "E914", {"start": v(29.29, 12.87) * mm, "end": v(29.27, 12.81) * mm});
            skSolve(sketch);
        }
        {
            var Q0;
            Q0=makeQuery(id+"F12.imprint","IMPRINT",FACE,{"disambiguationData":[TD([[makeQuery(id+"F12.imprint","IMPRINT",EDGE,{"derivedFrom":sQuery(id+"F12.wireOp",EDGE,"E876")}),-1.0]])]});
            extrude(context, id + "F13", {"entities" : qUnion([Q0]), "operationType" : NewBodyOperationType.REMOVE, "oppositeDirection" : true, "depth" : 0.05 * mm, "offsetDistance" : 25.4 * mm});
        }
        {
            var Q0;
            {var subQ0=sQuery(id+"F4.wireOp",EDGE,"E425");var subQ1=sQuery(id+"F4.wireOp",EDGE,"E424");var subQ2=sQuery(id+"F4.wireOp",EDGE,"E423");var subQ3=sQuery(id+"F4.wireOp",EDGE,"E421");var subQ4=sQuery(id+"F4.wireOp",EDGE,"E420");var subQ5=sQuery(id+"F4.wireOp",EDGE,"E419");var subQ6=sQuery(id+"F4.wireOp",EDGE,"E418");var subQ7=sQuery(id+"F4.wireOp",EDGE,"E417");var subQ8=sQuery(id+"F4.wireOp",EDGE,"E416");var subQ9=sQuery(id+"F4.wireOp",EDGE,"E415");var subQ10=sQuery(id+"F4.wireOp",EDGE,"E414");var subQ11=sQuery(id+"F4.wireOp",EDGE,"E413");var subQ12=sQuery(id+"F4.wireOp",EDGE,"E412");var subQ13=sQuery(id+"F4.wireOp",EDGE,"E411");var subQ14=sQuery(id+"F4.wireOp",EDGE,"E410");var subQ15=sQuery(id+"F4.wireOp",EDGE,"E409");var subQ16=sQuery(id+"F4.wireOp",EDGE,"E408");var subQ17=sQuery(id+"F4.wireOp",EDGE,"E407");var subQ18=sQuery(id+"F4.wireOp",EDGE,"E406");var subQ19=sQuery(id+"F4.wireOp",EDGE,"E405");var subQ20=sQuery(id+"F4.wireOp",EDGE,"E404");var subQ21=sQuery(id+"F4.wireOp",EDGE,"E403");var subQ22=sQuery(id+"F4.wireOp",EDGE,"E402");var subQ23=sQuery(id+"F4.wireOp",EDGE,"E401");var subQ24=sQuery(id+"F4.wireOp",EDGE,"E400");var subQ25=sQuery(id+"F4.wireOp",EDGE,"E399");var subQ26=sQuery(id+"F4.wireOp",EDGE,"E398");var subQ27=sQuery(id+"F4.wireOp",EDGE,"E397");var subQ28=sQuery(id+"F4.wireOp",EDGE,"E396");var subQ29=sQuery(id+"F4.wireOp",EDGE,"E395");var subQ30=sQuery(id+"F4.wireOp",EDGE,"E394");var subQ31=sQuery(id+"F4.wireOp",EDGE,"E393");var subQ32=sQuery(id+"F4.wireOp",EDGE,"E392");var subQ33=sQuery(id+"F4.wireOp",EDGE,"E391");var subQ34=sQuery(id+"F4.wireOp",EDGE,"E390");var subQ35=sQuery(id+"F4.wireOp",EDGE,"E389");var subQ36=sQuery(id+"F4.wireOp",EDGE,"E388");var subQ37=sQuery(id+"F4.wireOp",EDGE,"E387");var subQ38=sQuery(id+"F4.wireOp",EDGE,"E386");var subQ39=sQuery(id+"F4.wireOp",EDGE,"E385");var subQ41=sQuery(id+"F4.wireOp",EDGE,"E384");var subQ43=sQuery(id+"F4.wireOp",EDGE,"E383");var subQ45=sQuery(id+"F4.wireOp",EDGE,"E382");var subQ47=sQuery(id+"F4.wireOp",EDGE,"E381");var subQ49=sQuery(id+"F4.wireOp",EDGE,"E380");var subQ51=sQuery(id+"F4.wireOp",EDGE,"E379");var subQ53=sQuery(id+"F4.wireOp",EDGE,"E378");var subQ55=sQuery(id+"F4.wireOp",EDGE,"E377");var subQ57=sQuery(id+"F4.wireOp",EDGE,"E376");var subQ59=sQuery(id+"F4.wireOp",EDGE,"E375");var subQ61=sQuery(id+"F4.wireOp",EDGE,"E374");var subQ63=sQuery(id+"F4.wireOp",EDGE,"E373");var subQ65=sQuery(id+"F4.wireOp",EDGE,"E372");var subQ67=sQuery(id+"F4.wireOp",EDGE,"E371");var subQ69=sQuery(id+"F4.wireOp",EDGE,"E370");var subQ71=sQuery(id+"F4.wireOp",EDGE,"E369");var subQ73=sQuery(id+"F4.wireOp",EDGE,"E368");var subQ75=sQuery(id+"F4.wireOp",EDGE,"E367");var subQ77=sQuery(id+"F4.wireOp",EDGE,"E366");var subQ79=sQuery(id+"F4.wireOp",EDGE,"E365");var subQ81=sQuery(id+"F4.wireOp",EDGE,"E364");var subQ83=sQuery(id+"F4.wireOp",EDGE,"E363");var subQ85=sQuery(id+"F4.wireOp",EDGE,"E362");var subQ87=sQuery(id+"F4.wireOp",EDGE,"E361");var subQ89=sQuery(id+"F4.wireOp",EDGE,"E360");var subQ91=sQuery(id+"F4.wireOp",EDGE,"E359");var subQ93=sQuery(id+"F4.wireOp",EDGE,"E358");var subQ95=sQuery(id+"F4.wireOp",EDGE,"E357");var subQ97=sQuery(id+"F4.wireOp",EDGE,"E356");var subQ99=sQuery(id+"F4.wireOp",EDGE,"E355");var subQ101=sQuery(id+"F4.wireOp",EDGE,"E354");var subQ103=sQuery(id+"F4.wireOp",EDGE,"E353");var subQ105=sQuery(id+"F4.wireOp",EDGE,"E352");var subQ107=sQuery(id+"F4.wireOp",EDGE,"E351");var subQ109=sQuery(id+"F4.wireOp",EDGE,"E350");var subQ111=sQuery(id+"F4.wireOp",EDGE,"E349");var subQ113=sQuery(id+"F4.wireOp",EDGE,"E348");var subQ115=sQuery(id+"F4.wireOp",EDGE,"E347");var subQ117=sQuery(id+"F4.wireOp",EDGE,"E346");var subQ119=sQuery(id+"F4.wireOp",EDGE,"E345");var subQ121=sQuery(id+"F4.wireOp",EDGE,"E344");var subQ122=sQuery(id+"F4.wireOp",EDGE,"E343");var subQ134=sQuery(id+"F4.wireOp",EDGE,"E342");var subQ135=sQuery(id+"F4.wireOp",EDGE,"E341");var subQ136=sQuery(id+"F4.wireOp",EDGE,"E340");var subQ137=sQuery(id+"F4.wireOp",EDGE,"E339");var subQ138=sQuery(id+"F4.wireOp",EDGE,"E338");var subQ139=sQuery(id+"F4.wireOp",EDGE,"E337");var subQ140=sQuery(id+"F4.wireOp",EDGE,"E336");var subQ141=sQuery(id+"F4.wireOp",EDGE,"E335");var subQ142=sQuery(id+"F4.wireOp",EDGE,"E334");var subQ143=sQuery(id+"F4.wireOp",EDGE,"E333");var subQ144=sQuery(id+"F4.wireOp",EDGE,"E332");var subQ145=sQuery(id+"F4.wireOp",EDGE,"E331");var subQ146=sQuery(id+"F4.wireOp",EDGE,"E330");var subQ147=sQuery(id+"F4.wireOp",EDGE,"E329");var subQ148=sQuery(id+"F4.wireOp",EDGE,"E328");var subQ149=sQuery(id+"F4.wireOp",EDGE,"E327");var subQ150=sQuery(id+"F4.wireOp",EDGE,"E326");var subQ151=sQuery(id+"F4.wireOp",EDGE,"E325");var subQ152=sQuery(id+"F4.wireOp",EDGE,"E324");var subQ153=sQuery(id+"F4.wireOp",EDGE,"E323");var subQ154=sQuery(id+"F4.wireOp",EDGE,"E322");var subQ155=sQuery(id+"F4.wireOp",EDGE,"E321");var subQ156=sQuery(id+"F4.wireOp",EDGE,"E320");var subQ157=sQuery(id+"F4.wireOp",EDGE,"E319");var subQ158=sQuery(id+"F4.wireOp",EDGE,"E318");var subQ159=sQuery(id+"F4.wireOp",EDGE,"E317");var subQ160=sQuery(id+"F4.wireOp",EDGE,"E316");var subQ161=sQuery(id+"F4.wireOp",EDGE,"E315");var subQ162=sQuery(id+"F4.wireOp",EDGE,"E314");var subQ163=sQuery(id+"F4.wireOp",EDGE,"E313");var subQ164=sQuery(id+"F4.wireOp",EDGE,"E312");var subQ165=sQuery(id+"F4.wireOp",EDGE,"E311");var subQ166=sQuery(id+"F4.wireOp",EDGE,"E310");var subQ167=sQuery(id+"F4.wireOp",EDGE,"E309");var subQ168=sQuery(id+"F4.wireOp",EDGE,"E308");var subQ169=sQuery(id+"F4.wireOp",EDGE,"E307");var subQ170=sQuery(id+"F4.wireOp",EDGE,"E306");var subQ171=sQuery(id+"F4.wireOp",EDGE,"E305");var subQ172=sQuery(id+"F4.wireOp",EDGE,"E304");var subQ173=sQuery(id+"F4.wireOp",EDGE,"E303");var subQ174=sQuery(id+"F4.wireOp",EDGE,"E302");var subQ175=sQuery(id+"F4.wireOp",EDGE,"E292");var subQ176=sQuery(id+"F4.wireOp",EDGE,"E291");var subQ177=sQuery(id+"F4.wireOp",EDGE,"E184");var subQ178=sQuery(id+"F4.wireOp",EDGE,"E183");var subQ179=sQuery(id+"F4.wireOp",EDGE,"E182");var subQ180=sQuery(id+"F4.wireOp",EDGE,"E181");var subQ181=sQuery(id+"F4.wireOp",EDGE,"E180");var subQ182=sQuery(id+"F4.wireOp",EDGE,"E179");var subQ183=sQuery(id+"F4.wireOp",EDGE,"E178");var subQ184=sQuery(id+"F4.wireOp",EDGE,"E177");var subQ185=sQuery(id+"F4.wireOp",EDGE,"E176");var subQ186=sQuery(id+"F4.wireOp",EDGE,"E175");var subQ187=sQuery(id+"F4.wireOp",EDGE,"E174");var subQ188=sQuery(id+"F4.wireOp",EDGE,"E77");var subQ189=sQuery(id+"F4.wireOp",EDGE,"E277");var subQ190=sQuery(id+"F4.wireOp",EDGE,"E173");var subQ191=sQuery(id+"F4.wireOp",EDGE,"E76");var subQ192=sQuery(id+"F4.wireOp",EDGE,"E276");var subQ193=sQuery(id+"F4.wireOp",EDGE,"E172");var subQ194=sQuery(id+"F4.wireOp",EDGE,"E75");var subQ195=sQuery(id+"F4.wireOp",EDGE,"E275");var subQ196=sQuery(id+"F4.wireOp",EDGE,"E171");var subQ197=sQuery(id+"F4.wireOp",EDGE,"E74");var subQ198=sQuery(id+"F4.wireOp",EDGE,"E274");var subQ199=sQuery(id+"F4.wireOp",EDGE,"E170");var subQ200=sQuery(id+"F4.wireOp",EDGE,"E73");var subQ201=sQuery(id+"F4.wireOp",EDGE,"E273");var subQ202=sQuery(id+"F4.wireOp",EDGE,"E169");var subQ203=sQuery(id+"F4.wireOp",EDGE,"E72");var subQ204=sQuery(id+"F4.wireOp",EDGE,"E272");var subQ205=sQuery(id+"F4.wireOp",EDGE,"E168");var subQ206=sQuery(id+"F4.wireOp",EDGE,"E71");var subQ207=sQuery(id+"F4.wireOp",EDGE,"E271");var subQ208=sQuery(id+"F4.wireOp",EDGE,"E167");var subQ209=sQuery(id+"F4.wireOp",EDGE,"E70");var subQ210=sQuery(id+"F4.wireOp",EDGE,"E270");var subQ211=sQuery(id+"F4.wireOp",EDGE,"E166");var subQ212=sQuery(id+"F4.wireOp",EDGE,"E69");var subQ213=sQuery(id+"F4.wireOp",EDGE,"E269");var subQ214=sQuery(id+"F4.wireOp",EDGE,"E165");var subQ215=sQuery(id+"F4.wireOp",EDGE,"E68");var subQ216=sQuery(id+"F4.wireOp",EDGE,"E268");var subQ217=sQuery(id+"F4.wireOp",EDGE,"E164");var subQ218=sQuery(id+"F4.wireOp",EDGE,"E67");var subQ219=sQuery(id+"F4.wireOp",EDGE,"E267");var subQ220=sQuery(id+"F4.wireOp",EDGE,"E66");var subQ221=sQuery(id+"F4.wireOp",EDGE,"E266");var subQ222=sQuery(id+"F4.wireOp",EDGE,"E65");var subQ223=sQuery(id+"F4.wireOp",EDGE,"E265");var subQ224=sQuery(id+"F4.wireOp",EDGE,"E64");var subQ225=sQuery(id+"F4.wireOp",EDGE,"E264");var subQ226=sQuery(id+"F4.wireOp",EDGE,"E63");var subQ227=sQuery(id+"F4.wireOp",EDGE,"E263");var subQ228=sQuery(id+"F4.wireOp",EDGE,"E62");var subQ229=sQuery(id+"F4.wireOp",EDGE,"E262");var subQ230=sQuery(id+"F4.wireOp",EDGE,"E61");var subQ231=sQuery(id+"F4.wireOp",EDGE,"E261");var subQ232=sQuery(id+"F4.wireOp",EDGE,"E60");var subQ233=sQuery(id+"F4.wireOp",EDGE,"E260");var subQ234=sQuery(id+"F4.wireOp",EDGE,"E59");var subQ235=sQuery(id+"F4.wireOp",EDGE,"E259");var subQ236=sQuery(id+"F4.wireOp",EDGE,"E58");var subQ237=sQuery(id+"F4.wireOp",EDGE,"E258");var subQ238=sQuery(id+"F4.wireOp",EDGE,"E57");var subQ239=sQuery(id+"F4.wireOp",EDGE,"E257");var subQ240=sQuery(id+"F4.wireOp",EDGE,"E56");var subQ241=sQuery(id+"F4.wireOp",EDGE,"E256");var subQ242=sQuery(id+"F4.wireOp",EDGE,"E55");var subQ243=sQuery(id+"F4.wireOp",EDGE,"E255");var subQ244=sQuery(id+"F4.wireOp",EDGE,"E54");var subQ245=sQuery(id+"F4.wireOp",EDGE,"E254");var subQ246=sQuery(id+"F4.wireOp",EDGE,"E53");var subQ247=sQuery(id+"F4.wireOp",EDGE,"E253");var subQ248=sQuery(id+"F4.wireOp",EDGE,"E52");var subQ249=sQuery(id+"F4.wireOp",EDGE,"E252");var subQ250=sQuery(id+"F4.wireOp",EDGE,"E51");var subQ251=sQuery(id+"F4.wireOp",EDGE,"E251");var subQ252=sQuery(id+"F4.wireOp",EDGE,"E50");var subQ253=sQuery(id+"F4.wireOp",EDGE,"E250");var subQ254=sQuery(id+"F4.wireOp",EDGE,"E49");var subQ255=sQuery(id+"F4.wireOp",EDGE,"E249");var subQ256=sQuery(id+"F4.wireOp",EDGE,"E22");var subQ257=sQuery(id+"F4.wireOp",EDGE,"E21");var subQ258=sQuery(id+"F4.wireOp",EDGE,"E222");var subQ259=sQuery(id+"F4.wireOp",EDGE,"E20");var subQ260=sQuery(id+"F4.wireOp",EDGE,"E221");var subQ261=sQuery(id+"F4.wireOp",EDGE,"E19");var subQ262=sQuery(id+"F4.wireOp",EDGE,"E220");var subQ263=sQuery(id+"F4.wireOp",EDGE,"E18");var subQ264=sQuery(id+"F4.wireOp",EDGE,"E218");var subQ265=sQuery(id+"F4.wireOp",EDGE,"E17");var subQ266=sQuery(id+"F4.wireOp",EDGE,"E217");var subQ267=sQuery(id+"F4.wireOp",EDGE,"E16");var subQ268=sQuery(id+"F4.wireOp",EDGE,"E216");var subQ269=sQuery(id+"F4.wireOp",EDGE,"E15");var subQ270=sQuery(id+"F4.wireOp",EDGE,"E215");var subQ271=sQuery(id+"F4.wireOp",EDGE,"E14");var subQ272=sQuery(id+"F4.wireOp",EDGE,"E214");var subQ273=sQuery(id+"F4.wireOp",EDGE,"E13");var subQ274=sQuery(id+"F4.wireOp",EDGE,"E213");var subQ275=sQuery(id+"F4.wireOp",EDGE,"E12");var subQ276=sQuery(id+"F4.wireOp",EDGE,"E212");var subQ277=sQuery(id+"F4.wireOp",EDGE,"E427");var subQ278=sQuery(id+"F4.wireOp",EDGE,"E4");var subQ279=sQuery(id+"F4.wireOp",EDGE,"E204");var subQ280=sQuery(id+"F4.wireOp",EDGE,"E426");var subQ281=sQuery(id+"F4.wireOp",EDGE,"E3");var subQ282=sQuery(id+"F4.wireOp",EDGE,"E203");var subQ283=sQuery(id+"F4.wireOp",EDGE,"E5");var subQ284=sQuery(id+"F4.wireOp",EDGE,"E205");var subQ285=sQuery(id+"F4.wireOp",EDGE,"E23");var subQ286=sQuery(id+"F4.wireOp",EDGE,"E422");var subQ287=sQuery(id+"F4.wireOp",EDGE,"E2");var subQ288=sQuery(id+"F4.wireOp",EDGE,"E200");var subQ289=sQuery(id+"F4.wireOp",EDGE,"E48");var subQ290=sQuery(id+"F4.wireOp",EDGE,"E248");var subQ291=sQuery(id+"F4.wireOp",EDGE,"E11");var subQ292=sQuery(id+"F4.wireOp",EDGE,"E211");var subQ293=sQuery(id+"F4.wireOp",EDGE,"E6");var subQ294=sQuery(id+"F4.wireOp",EDGE,"E206");var subQ295=sQuery(id+"F4.wireOp",EDGE,"E7");var subQ296=sQuery(id+"F4.wireOp",EDGE,"E207");var subQ297=sQuery(id+"F4.wireOp",EDGE,"E8");var subQ298=sQuery(id+"F4.wireOp",EDGE,"E208");var subQ299=sQuery(id+"F4.wireOp",EDGE,"E9");var subQ300=sQuery(id+"F4.wireOp",EDGE,"E209");var subQ301=sQuery(id+"F4.wireOp",EDGE,"E10");var subQ302=sQuery(id+"F4.wireOp",EDGE,"E210");var subQ303=sQuery(id+"F4.wireOp",EDGE,"E24");var subQ304=sQuery(id+"F4.wireOp",EDGE,"E25");var subQ305=sQuery(id+"F4.wireOp",EDGE,"E226");var subQ306=sQuery(id+"F4.wireOp",EDGE,"E26");var subQ307=sQuery(id+"F4.wireOp",EDGE,"E227");var subQ308=sQuery(id+"F4.wireOp",EDGE,"E27");var subQ309=sQuery(id+"F4.wireOp",EDGE,"E228");var subQ310=sQuery(id+"F4.wireOp",EDGE,"E28");var subQ311=sQuery(id+"F4.wireOp",EDGE,"E229");var subQ312=sQuery(id+"F4.wireOp",EDGE,"E29");var subQ313=sQuery(id+"F4.wireOp",EDGE,"E230");var subQ314=sQuery(id+"F4.wireOp",EDGE,"E30");var subQ315=sQuery(id+"F4.wireOp",EDGE,"E231");var subQ316=sQuery(id+"F4.wireOp",EDGE,"E31");var subQ317=sQuery(id+"F4.wireOp",EDGE,"E232");var subQ318=sQuery(id+"F4.wireOp",EDGE,"E32");var subQ319=sQuery(id+"F4.wireOp",EDGE,"E233");var subQ320=sQuery(id+"F4.wireOp",EDGE,"E33");var subQ321=sQuery(id+"F4.wireOp",EDGE,"E234");var subQ322=sQuery(id+"F4.wireOp",EDGE,"E34");var subQ323=sQuery(id+"F4.wireOp",EDGE,"E235");var subQ324=sQuery(id+"F4.wireOp",EDGE,"E35");var subQ325=sQuery(id+"F4.wireOp",EDGE,"E236");var subQ326=sQuery(id+"F4.wireOp",EDGE,"E36");var subQ327=sQuery(id+"F4.wireOp",EDGE,"E237");var subQ328=sQuery(id+"F4.wireOp",EDGE,"E37");var subQ329=sQuery(id+"F4.wireOp",EDGE,"E238");var subQ330=sQuery(id+"F4.wireOp",EDGE,"E38");var subQ331=sQuery(id+"F4.wireOp",EDGE,"E239");var subQ332=sQuery(id+"F4.wireOp",EDGE,"E39");var subQ333=sQuery(id+"F4.wireOp",EDGE,"E240");var subQ334=sQuery(id+"F4.wireOp",EDGE,"E40");var subQ335=sQuery(id+"F4.wireOp",EDGE,"E241");var subQ336=sQuery(id+"F4.wireOp",EDGE,"E41");var subQ337=sQuery(id+"F4.wireOp",EDGE,"E242");var subQ338=sQuery(id+"F4.wireOp",EDGE,"E43");var subQ339=sQuery(id+"F4.wireOp",EDGE,"E42");var subQ340=sQuery(id+"F4.wireOp",EDGE,"E243");var subQ341=sQuery(id+"F4.wireOp",EDGE,"E44");var subQ342=sQuery(id+"F4.wireOp",EDGE,"E244");var subQ343=sQuery(id+"F4.wireOp",EDGE,"E45");var subQ344=sQuery(id+"F4.wireOp",EDGE,"E245");var subQ345=sQuery(id+"F4.wireOp",EDGE,"E46");var subQ346=sQuery(id+"F4.wireOp",EDGE,"E246");var subQ347=sQuery(id+"F4.wireOp",EDGE,"E47");var subQ348=sQuery(id+"F4.wireOp",EDGE,"E247");var subQ349=sQuery(id+"F4.wireOp",EDGE,"E185");var subQ350=sQuery(id+"F4.wireOp",EDGE,"E186");var subQ351=sQuery(id+"F4.wireOp",EDGE,"E187");var subQ352=sQuery(id+"F4.wireOp",EDGE,"E188");var subQ353=sQuery(id+"F4.wireOp",EDGE,"E189");var subQ354=sQuery(id+"F4.wireOp",EDGE,"E190");var subQ355=sQuery(id+"F4.wireOp",EDGE,"E191");var subQ356=sQuery(id+"F4.wireOp",EDGE,"E192");var subQ357=sQuery(id+"F4.wireOp",EDGE,"E193");var subQ358=sQuery(id+"F4.wireOp",EDGE,"E194");var subQ359=sQuery(id+"F4.wireOp",EDGE,"E195");var subQ360=sQuery(id+"F4.wireOp",EDGE,"E196");var subQ361=sQuery(id+"F4.wireOp",EDGE,"E197");var subQ362=sQuery(id+"F4.wireOp",EDGE,"E198");var subQ363=sQuery(id+"F4.wireOp",EDGE,"E199");var subQ364=sQuery(id+"F4.wireOp",EDGE,"E201");var subQ365=sQuery(id+"F4.wireOp",EDGE,"E202");var subQ366=sQuery(id+"F4.wireOp",EDGE,"E278");var subQ367=sQuery(id+"F4.wireOp",EDGE,"E279");var subQ368=sQuery(id+"F4.wireOp",EDGE,"E280");var subQ369=sQuery(id+"F4.wireOp",EDGE,"E281");var subQ370=sQuery(id+"F4.wireOp",EDGE,"E282");var subQ371=sQuery(id+"F4.wireOp",EDGE,"E283");var subQ372=sQuery(id+"F4.wireOp",EDGE,"E284");var subQ373=sQuery(id+"F4.wireOp",EDGE,"E285");var subQ374=sQuery(id+"F4.wireOp",EDGE,"E286");var subQ375=sQuery(id+"F4.wireOp",EDGE,"E287");var subQ376=sQuery(id+"F4.wireOp",EDGE,"E288");var subQ377=sQuery(id+"F4.wireOp",EDGE,"E289");var subQ378=sQuery(id+"F4.wireOp",EDGE,"E290");Q0=makeQuery(id+"F11.boolean.opBoolean","SPLIT",FACE,{"disambiguationData":[TD([makeQuery(id+"F5.opExtrude","SWEPT_FACE",FACE,{"disambiguationData":[OSD([subQ287])]})])],"derivedFrom":makeQuery(id+"F5.opExtrude","CAP_FACE",FACE,{"disambiguationData":[OSD([subQ287,subQ281,subQ278,subQ283,subQ293,subQ295,subQ297,subQ299,subQ301,subQ291,subQ275,subQ273,subQ271,subQ269,subQ267,subQ265,subQ263,subQ261,subQ259,subQ257,subQ256,subQ285,subQ303,subQ304,subQ306,subQ308,subQ310,subQ312,subQ314,subQ316,subQ318,subQ320,subQ322,subQ324,subQ326,subQ328,subQ330,subQ332,subQ334,subQ336,subQ339,subQ338,subQ341,subQ343,subQ345,subQ347,subQ289,subQ254,subQ252,subQ250,subQ248,subQ246,subQ244,subQ242,subQ240,subQ238,subQ236,subQ234,subQ232,subQ230,subQ228,subQ226,subQ224,subQ222,subQ220,subQ218,subQ215,subQ212,subQ209,subQ206,subQ203,subQ200,subQ197,subQ194,subQ191,subQ188,sQuery(id+"F4.wireOp",EDGE,"E78"),sQuery(id+"F4.wireOp",EDGE,"E79"),sQuery(id+"F4.wireOp",EDGE,"E80"),sQuery(id+"F4.wireOp",EDGE,"E81"),sQuery(id+"F4.wireOp",EDGE,"E82"),sQuery(id+"F4.wireOp",EDGE,"E83"),sQuery(id+"F4.wireOp",EDGE,"E84"),sQuery(id+"F4.wireOp",EDGE,"E85"),sQuery(id+"F4.wireOp",EDGE,"E86"),sQuery(id+"F4.wireOp",EDGE,"E87"),sQuery(id+"F4.wireOp",EDGE,"E88"),sQuery(id+"F4.wireOp",EDGE,"E89"),sQuery(id+"F4.wireOp",EDGE,"E90"),sQuery(id+"F4.wireOp",EDGE,"E91"),sQuery(id+"F4.wireOp",EDGE,"E92"),sQuery(id+"F4.wireOp",EDGE,"E93"),sQuery(id+"F4.wireOp",EDGE,"E94"),sQuery(id+"F4.wireOp",EDGE,"E95"),sQuery(id+"F4.wireOp",EDGE,"E96"),sQuery(id+"F4.wireOp",EDGE,"E97"),sQuery(id+"F4.wireOp",EDGE,"E98"),sQuery(id+"F4.wireOp",EDGE,"E99"),sQuery(id+"F4.wireOp",EDGE,"E100"),sQuery(id+"F4.wireOp",EDGE,"E101"),sQuery(id+"F4.wireOp",EDGE,"E102"),sQuery(id+"F4.wireOp",EDGE,"E103"),sQuery(id+"F4.wireOp",EDGE,"E104"),sQuery(id+"F4.wireOp",EDGE,"E105"),sQuery(id+"F4.wireOp",EDGE,"E106"),sQuery(id+"F4.wireOp",EDGE,"E107"),sQuery(id+"F4.wireOp",EDGE,"E108"),sQuery(id+"F4.wireOp",EDGE,"E109"),sQuery(id+"F4.wireOp",EDGE,"E110"),sQuery(id+"F4.wireOp",EDGE,"E111"),sQuery(id+"F4.wireOp",EDGE,"E112"),sQuery(id+"F4.wireOp",EDGE,"E113"),sQuery(id+"F4.wireOp",EDGE,"E114"),sQuery(id+"F4.wireOp",EDGE,"E115"),sQuery(id+"F4.wireOp",EDGE,"E116"),sQuery(id+"F4.wireOp",EDGE,"E117"),sQuery(id+"F4.wireOp",EDGE,"E118"),sQuery(id+"F4.wireOp",EDGE,"E119"),sQuery(id+"F4.wireOp",EDGE,"E120"),sQuery(id+"F4.wireOp",EDGE,"E121"),sQuery(id+"F4.wireOp",EDGE,"E122"),sQuery(id+"F4.wireOp",EDGE,"E123"),sQuery(id+"F4.wireOp",EDGE,"E124"),sQuery(id+"F4.wireOp",EDGE,"E125"),sQuery(id+"F4.wireOp",EDGE,"E126"),sQuery(id+"F4.wireOp",EDGE,"E127"),sQuery(id+"F4.wireOp",EDGE,"E128"),sQuery(id+"F4.wireOp",EDGE,"E129"),sQuery(id+"F4.wireOp",EDGE,"E130"),sQuery(id+"F4.wireOp",EDGE,"E131"),sQuery(id+"F4.wireOp",EDGE,"E132"),sQuery(id+"F4.wireOp",EDGE,"E133"),sQuery(id+"F4.wireOp",EDGE,"E134"),sQuery(id+"F4.wireOp",EDGE,"E135"),sQuery(id+"F4.wireOp",EDGE,"E136"),sQuery(id+"F4.wireOp",EDGE,"E137"),sQuery(id+"F4.wireOp",EDGE,"E138"),sQuery(id+"F4.wireOp",EDGE,"E139"),sQuery(id+"F4.wireOp",EDGE,"E140"),sQuery(id+"F4.wireOp",EDGE,"E141"),sQuery(id+"F4.wireOp",EDGE,"E142"),sQuery(id+"F4.wireOp",EDGE,"E143"),sQuery(id+"F4.wireOp",EDGE,"E144"),sQuery(id+"F4.wireOp",EDGE,"E145"),sQuery(id+"F4.wireOp",EDGE,"E146"),sQuery(id+"F4.wireOp",EDGE,"E147"),sQuery(id+"F4.wireOp",EDGE,"E148"),sQuery(id+"F4.wireOp",EDGE,"E149"),sQuery(id+"F4.wireOp",EDGE,"E150"),sQuery(id+"F4.wireOp",EDGE,"E151"),sQuery(id+"F4.wireOp",EDGE,"E152"),sQuery(id+"F4.wireOp",EDGE,"E153"),sQuery(id+"F4.wireOp",EDGE,"E154"),sQuery(id+"F4.wireOp",EDGE,"E155"),sQuery(id+"F4.wireOp",EDGE,"E156"),sQuery(id+"F4.wireOp",EDGE,"E157"),sQuery(id+"F4.wireOp",EDGE,"E158"),sQuery(id+"F4.wireOp",EDGE,"E159"),sQuery(id+"F4.wireOp",EDGE,"E160"),sQuery(id+"F4.wireOp",EDGE,"E161"),sQuery(id+"F4.wireOp",EDGE,"E162"),sQuery(id+"F4.wireOp",EDGE,"E163"),subQ217,subQ214,subQ211,subQ208,subQ205,subQ202,subQ199,subQ196,subQ193,subQ190,subQ187,subQ186,subQ185,subQ184,subQ183,subQ182,subQ181,subQ180,subQ179,subQ178,subQ177,subQ349,subQ350,subQ351,subQ352,subQ353,subQ354,subQ355,subQ356,subQ357,subQ358,subQ359,subQ360,subQ361,subQ362,subQ363,subQ288,subQ364,subQ365,subQ282,subQ279,subQ284,subQ294,subQ296,subQ298,subQ300,subQ302,subQ292,subQ276,subQ274,subQ272,subQ270,subQ268,subQ266,subQ264,subQ262,subQ260,subQ258,sQuery(id+"F4.wireOp",EDGE,"E223"),sQuery(id+"F4.wireOp",EDGE,"E224"),sQuery(id+"F4.wireOp",EDGE,"E225"),subQ305,subQ307,subQ309,subQ311,subQ313,subQ315,subQ317,subQ319,subQ321,subQ323,subQ325,subQ327,subQ329,subQ331,subQ333,subQ335,subQ337,subQ340,subQ342,subQ344,subQ346,subQ348,subQ290,subQ255,subQ253,subQ251,subQ249,subQ247,subQ245,subQ243,subQ241,subQ239,subQ237,subQ235,subQ233,subQ231,subQ229,subQ227,subQ225,subQ223,subQ221,subQ219,subQ216,subQ213,subQ210,subQ207,subQ204,subQ201,subQ198,subQ195,subQ192,subQ189,subQ366,subQ367,subQ368,subQ369,subQ370,subQ371,subQ372,subQ373,subQ374,subQ375,subQ376,subQ377,subQ378,subQ176,subQ175,subQ174,subQ173,subQ172,subQ171,subQ170,subQ169,subQ168,subQ167,subQ166,subQ165,subQ164,subQ163,subQ162,subQ161,subQ160,subQ159,subQ158,subQ157,subQ156,subQ155,subQ154,subQ153,subQ152,subQ151,subQ150,subQ149,subQ148,subQ147,subQ146,subQ145,subQ144,subQ143,subQ142,subQ141,subQ140,subQ139,subQ138,subQ137,subQ136,subQ135,subQ134,subQ122,subQ121,subQ119,subQ117,subQ115,subQ113,subQ111,subQ109,subQ107,subQ105,subQ103,subQ101,subQ99,subQ97,subQ95,subQ93,subQ91,subQ89,subQ87,subQ85,subQ83,subQ81,subQ79,subQ77,subQ75,subQ73,subQ71,subQ69,subQ67,subQ65,subQ63,subQ61,subQ59,subQ57,subQ55,subQ53,subQ51,subQ49,subQ47,subQ45,subQ43,subQ41,subQ39,subQ38,subQ37,subQ36,subQ35,subQ34,subQ33,subQ32,subQ31,subQ30,subQ29,subQ28,subQ27,subQ26,subQ25,subQ24,subQ23,subQ22,subQ21,subQ20,subQ19,subQ18,subQ17,subQ16,subQ15,subQ14,subQ13,subQ12,subQ11,subQ10,subQ9,subQ8,subQ7,subQ6,subQ5,subQ4,subQ3,subQ286,subQ2,subQ1,subQ0,subQ280,subQ277])],"isStart":false})});}
            var sketch = newSketch(context, id + "F14", { "sketchPlane" : qUnion([Q0])});
            skLineSegment(sketch, "E915", {"start": v(28.9, -13.72) * mm, "end": v(29.04, -13.8) * mm});
            skLineSegment(sketch, "E916", {"start": v(29.04, -13.8) * mm, "end": v(29.2, -13.89) * mm});
            skLineSegment(sketch, "E917", {"start": v(29.2, -13.89) * mm, "end": v(29.4, -13.96) * mm});
            skLineSegment(sketch, "E918", {"start": v(29.4, -13.96) * mm, "end": v(29.66, -14.02) * mm});
            skLineSegment(sketch, "E919", {"start": v(29.66, -14.02) * mm, "end": v(29.92, -14.05) * mm});
            skLineSegment(sketch, "E920", {"start": v(29.92, -14.05) * mm, "end": v(30.2, -14.06) * mm});
            skLineSegment(sketch, "E921", {"start": v(30.2, -14.06) * mm, "end": v(30.6, -14.04) * mm});
            skLineSegment(sketch, "E922", {"start": v(30.6, -14.04) * mm, "end": v(30.96, -14) * mm});
            skLineSegment(sketch, "E923", {"start": v(30.96, -14) * mm, "end": v(31.32, -13.91) * mm});
            skLineSegment(sketch, "E924", {"start": v(31.32, -13.91) * mm, "end": v(31.6, -13.85) * mm});
            skLineSegment(sketch, "E925", {"start": v(31.6, -13.85) * mm, "end": v(31.8, -13.82) * mm});
            skLineSegment(sketch, "E926", {"start": v(31.8, -13.82) * mm, "end": v(31.83, -13.83) * mm});
            skLineSegment(sketch, "E927", {"start": v(31.83, -13.83) * mm, "end": v(31.87, -13.85) * mm});
            skLineSegment(sketch, "E928", {"start": v(31.87, -13.85) * mm, "end": v(31.9, -13.91) * mm});
            skLineSegment(sketch, "E929", {"start": v(31.97, -14.05) * mm, "end": v(31.95, -14.19) * mm});
            skLineSegment(sketch, "E930", {"start": v(31.95, -14.19) * mm, "end": v(31.9, -14.33) * mm});
            skLineSegment(sketch, "E931", {"start": v(31.9, -14.33) * mm, "end": v(31.89, -14.4) * mm});
            skLineSegment(sketch, "E932", {"start": v(31.89, -14.4) * mm, "end": v(31.84, -14.5) * mm});
            skLineSegment(sketch, "E933", {"start": v(31.84, -14.5) * mm, "end": v(31.73, -14.64) * mm});
            skLineSegment(sketch, "E934", {"start": v(31.73, -14.64) * mm, "end": v(31.58, -14.75) * mm});
            skLineSegment(sketch, "E935", {"start": v(31.58, -14.75) * mm, "end": v(31.44, -14.8) * mm});
            skLineSegment(sketch, "E936", {"start": v(31.44, -14.8) * mm, "end": v(31.29, -14.85) * mm});
            skLineSegment(sketch, "E937", {"start": v(31.29, -14.85) * mm, "end": v(31.14, -14.85) * mm});
            skLineSegment(sketch, "E938", {"start": v(31.14, -14.85) * mm, "end": v(31.02, -14.84) * mm});
            skLineSegment(sketch, "E939", {"start": v(31.02, -14.84) * mm, "end": v(30.93, -14.8) * mm});
            skLineSegment(sketch, "E940", {"start": v(30.93, -14.8) * mm, "end": v(30.85, -14.73) * mm});
            skLineSegment(sketch, "E941", {"start": v(30.85, -14.73) * mm, "end": v(30.82, -14.67) * mm});
            skLineSegment(sketch, "E942", {"start": v(30.82, -14.67) * mm, "end": v(30.8, -14.63) * mm});
            skLineSegment(sketch, "E943", {"start": v(30.8, -14.63) * mm, "end": v(30.74, -14.6) * mm});
            skLineSegment(sketch, "E944", {"start": v(30.74, -14.6) * mm, "end": v(30.67, -14.6) * mm});
            skLineSegment(sketch, "E945", {"start": v(30.67, -14.6) * mm, "end": v(30.57, -14.64) * mm});
            skLineSegment(sketch, "E946", {"start": v(30.57, -14.64) * mm, "end": v(30.53, -14.69) * mm});
            skLineSegment(sketch, "E947", {"start": v(30.53, -14.69) * mm, "end": v(30.35, -14.8) * mm});
            skLineSegment(sketch, "E948", {"start": v(30.35, -14.8) * mm, "end": v(30.27, -14.87) * mm});
            skLineSegment(sketch, "E949", {"start": v(30.27, -14.87) * mm, "end": v(30.08, -14.95) * mm});
            skLineSegment(sketch, "E950", {"start": v(30.08, -14.95) * mm, "end": v(29.87, -15.03) * mm});
            skLineSegment(sketch, "E951", {"start": v(29.87, -15.03) * mm, "end": v(29.7, -15.05) * mm});
            skLineSegment(sketch, "E952", {"start": v(29.7, -15.05) * mm, "end": v(29.54, -15.1) * mm});
            skLineSegment(sketch, "E953", {"start": v(29.54, -15.1) * mm, "end": v(29.25, -15.17) * mm});
            skLineSegment(sketch, "E954", {"start": v(29.25, -15.17) * mm, "end": v(29.02, -15.21) * mm});
            skLineSegment(sketch, "E955", {"start": v(29.02, -15.21) * mm, "end": v(28.83, -15.24) * mm});
            skLineSegment(sketch, "E956", {"start": v(28.83, -15.24) * mm, "end": v(28.67, -15.24) * mm});
            skLineSegment(sketch, "E957", {"start": v(28.67, -15.24) * mm, "end": v(28.45, -15.26) * mm});
            skLineSegment(sketch, "E958", {"start": v(28.45, -15.26) * mm, "end": v(28.28, -15.24) * mm});
            skLineSegment(sketch, "E959", {"start": v(28.28, -15.24) * mm, "end": v(28.05, -15.22) * mm});
            skLineSegment(sketch, "E960", {"start": v(28.05, -15.22) * mm, "end": v(27.75, -15.19) * mm});
            skLineSegment(sketch, "E961", {"start": v(27.75, -15.19) * mm, "end": v(27.47, -15.13) * mm});
            skLineSegment(sketch, "E962", {"start": v(27.47, -15.13) * mm, "end": v(27.19, -15) * mm});
            skLineSegment(sketch, "E963", {"start": v(27.19, -15) * mm, "end": v(27.08, -14.88) * mm});
            skLineSegment(sketch, "E964", {"start": v(27.08, -14.88) * mm, "end": v(27.04, -14.75) * mm});
            skLineSegment(sketch, "E965", {"start": v(27.04, -14.75) * mm, "end": v(27.1, -14.57) * mm});
            skLineSegment(sketch, "E966", {"start": v(27.2, -14.43) * mm, "end": v(27.37, -14.27) * mm});
            skLineSegment(sketch, "E967", {"start": v(27.37, -14.27) * mm, "end": v(27.6, -14.16) * mm});
            skLineSegment(sketch, "E968", {"start": v(27.6, -14.16) * mm, "end": v(27.87, -14.01) * mm});
            skLineSegment(sketch, "E969", {"start": v(27.87, -14.01) * mm, "end": v(28.13, -13.91) * mm});
            skLineSegment(sketch, "E970", {"start": v(28.13, -13.91) * mm, "end": v(28.4, -13.81) * mm});
            skLineSegment(sketch, "E971", {"start": v(28.4, -13.81) * mm, "end": v(28.58, -13.76) * mm});
            skLineSegment(sketch, "E972", {"start": v(28.58, -13.76) * mm, "end": v(28.65, -13.73) * mm});
            skLineSegment(sketch, "E973", {"start": v(37.24, -14.96) * mm, "end": v(37.4, -15.2) * mm});
            skLineSegment(sketch, "E974", {"start": v(37.4, -15.2) * mm, "end": v(37.7, -15.52) * mm});
            skLineSegment(sketch, "E975", {"start": v(37.7, -15.52) * mm, "end": v(37.9, -15.68) * mm});
            skLineSegment(sketch, "E976", {"start": v(37.9, -15.68) * mm, "end": v(38.38, -15.86) * mm});
            skLineSegment(sketch, "E977", {"start": v(38.38, -15.86) * mm, "end": v(38.64, -15.91) * mm});
            skLineSegment(sketch, "E978", {"start": v(38.64, -15.91) * mm, "end": v(38.9, -15.93) * mm});
            skLineSegment(sketch, "E979", {"start": v(38.9, -15.93) * mm, "end": v(39.15, -15.87) * mm});
            skLineSegment(sketch, "E980", {"start": v(39.15, -15.87) * mm, "end": v(39.37, -15.82) * mm});
            skLineSegment(sketch, "E981", {"start": v(39.37, -15.82) * mm, "end": v(39.57, -15.7) * mm});
            skLineSegment(sketch, "E982", {"start": v(39.57, -15.7) * mm, "end": v(39.73, -15.6) * mm});
            skLineSegment(sketch, "E983", {"start": v(39.73, -15.6) * mm, "end": v(39.86, -15.42) * mm});
            skLineSegment(sketch, "E984", {"start": v(39.86, -15.42) * mm, "end": v(39.89, -15.22) * mm});
            skLineSegment(sketch, "E985", {"start": v(39.89, -15.22) * mm, "end": v(39.88, -15.03) * mm});
            skLineSegment(sketch, "E986", {"start": v(39.88, -15.03) * mm, "end": v(39.83, -14.78) * mm});
            skLineSegment(sketch, "E987", {"start": v(39.83, -14.78) * mm, "end": v(39.8, -14.65) * mm});
            skLineSegment(sketch, "E988", {"start": v(39.8, -14.65) * mm, "end": v(39.74, -14.44) * mm});
            skLineSegment(sketch, "E989", {"start": v(39.74, -14.44) * mm, "end": v(39.64, -14.23) * mm});
            skLineSegment(sketch, "E990", {"start": v(39.64, -14.23) * mm, "end": v(39.55, -14.08) * mm});
            skLineSegment(sketch, "E991", {"start": v(39.55, -14.08) * mm, "end": v(39.5, -14) * mm});
            skLineSegment(sketch, "E992", {"start": v(39.5, -14) * mm, "end": v(39.44, -13.9) * mm});
            skLineSegment(sketch, "E993", {"start": v(39.44, -13.9) * mm, "end": v(39.3, -14.04) * mm});
            skLineSegment(sketch, "E994", {"start": v(39.3, -14.04) * mm, "end": v(39.15, -14.12) * mm});
            skLineSegment(sketch, "E995", {"start": v(39.15, -14.12) * mm, "end": v(38.86, -14.2) * mm});
            skLineSegment(sketch, "E996", {"start": v(38.86, -14.2) * mm, "end": v(38.66, -14.26) * mm});
            skLineSegment(sketch, "E997", {"start": v(38.66, -14.26) * mm, "end": v(38.5, -14.3) * mm});
            skLineSegment(sketch, "E998", {"start": v(38.5, -14.3) * mm, "end": v(38.25, -14.33) * mm});
            skLineSegment(sketch, "E999", {"start": v(38.25, -14.33) * mm, "end": v(38.02, -14.34) * mm});
            skLineSegment(sketch, "E1000", {"start": v(38.02, -14.34) * mm, "end": v(37.8, -14.33) * mm});
            skLineSegment(sketch, "E1001", {"start": v(37.8, -14.33) * mm, "end": v(37.66, -14.3) * mm});
            skLineSegment(sketch, "E1002", {"start": v(37.66, -14.3) * mm, "end": v(37.45, -14.27) * mm});
            skLineSegment(sketch, "E1003", {"start": v(37.45, -14.27) * mm, "end": v(37.35, -14.23) * mm});
            skLineSegment(sketch, "E1004", {"start": v(37.35, -14.23) * mm, "end": v(37.2, -14.2) * mm});
            skLineSegment(sketch, "E1005", {"start": v(37.2, -14.2) * mm, "end": v(37.13, -14.17) * mm});
            skLineSegment(sketch, "E1006", {"start": v(37.13, -14.17) * mm, "end": v(37.09, -14.14) * mm});
            skLineSegment(sketch, "E1007", {"start": v(37.24, -14.96) * mm, "end": v(37.18, -14.9) * mm});
            skLineSegment(sketch, "E1008", {"start": v(37.18, -14.9) * mm, "end": v(37.13, -14.78) * mm});
            skLineSegment(sketch, "E1009", {"start": v(37.13, -14.78) * mm, "end": v(37.07, -14.65) * mm});
            skLineSegment(sketch, "E1010", {"start": v(37.07, -14.65) * mm, "end": v(37.03, -14.55) * mm});
            skLineSegment(sketch, "E1011", {"start": v(37.03, -14.55) * mm, "end": v(37, -14.45) * mm});
            skLineSegment(sketch, "E1012", {"start": v(37, -14.45) * mm, "end": v(36.98, -14.34) * mm});
            skLineSegment(sketch, "E1013", {"start": v(36.98, -14.34) * mm, "end": v(36.97, -14.28) * mm});
            skLineSegment(sketch, "E1014", {"start": v(36.97, -14.28) * mm, "end": v(36.97, -14.22) * mm});
            skLineSegment(sketch, "E1015", {"start": v(36.97, -14.22) * mm, "end": v(37, -14.19) * mm});
            skLineSegment(sketch, "E1016", {"start": v(37, -14.19) * mm, "end": v(37.02, -14.16) * mm});
            skLineSegment(sketch, "E1017", {"start": v(37.02, -14.16) * mm, "end": v(37.09, -14.14) * mm});
            skLineSegment(sketch, "E1018", {"start": v(28.65, -13.73) * mm, "end": v(28.7, -13.72) * mm});
            skLineSegment(sketch, "E1019", {"start": v(28.7, -13.72) * mm, "end": v(28.75, -13.72) * mm});
            skLineSegment(sketch, "E1020", {"start": v(28.75, -13.72) * mm, "end": v(28.8, -13.71) * mm});
            skLineSegment(sketch, "E1021", {"start": v(28.8, -13.71) * mm, "end": v(28.85, -13.72) * mm});
            skLineSegment(sketch, "E1022", {"start": v(28.85, -13.72) * mm, "end": v(28.88, -13.72) * mm});
            skLineSegment(sketch, "E1023", {"start": v(28.88, -13.72) * mm, "end": v(28.9, -13.72) * mm});
            skLineSegment(sketch, "E1024", {"start": v(27.1, -14.57) * mm, "end": v(27.1, -14.54) * mm});
            skLineSegment(sketch, "E1025", {"start": v(27.1, -14.54) * mm, "end": v(27.12, -14.5) * mm});
            skLineSegment(sketch, "E1026", {"start": v(27.12, -14.5) * mm, "end": v(27.16, -14.47) * mm});
            skLineSegment(sketch, "E1027", {"start": v(27.16, -14.47) * mm, "end": v(27.17, -14.45) * mm});
            skLineSegment(sketch, "E1028", {"start": v(27.17, -14.45) * mm, "end": v(27.2, -14.44) * mm});
            skLineSegment(sketch, "E1029", {"start": v(27.2, -14.44) * mm, "end": v(27.2, -14.43) * mm});
            skLineSegment(sketch, "E1030", {"start": v(31.97, -14.05) * mm, "end": v(31.97, -13.99) * mm});
            skLineSegment(sketch, "E1031", {"start": v(31.97, -13.99) * mm, "end": v(31.9, -13.91) * mm});
            skSolve(sketch);
        }
        {
            var Q0;
            Q0 = qSketchRegion(id + "F14", true);
            extrude(context, id + "F15", {"entities" : qUnion([Q0]), "operationType" : NewBodyOperationType.REMOVE, "oppositeDirection" : true, "depth" : 0.25 * mm, "offsetDistance" : 25.4 * mm});
        }
        {
            var Q0;
            {var subQ0=sQuery(id+"F4.wireOp",EDGE,"E425");var subQ1=sQuery(id+"F4.wireOp",EDGE,"E424");var subQ2=sQuery(id+"F4.wireOp",EDGE,"E423");var subQ3=sQuery(id+"F4.wireOp",EDGE,"E421");var subQ4=sQuery(id+"F4.wireOp",EDGE,"E420");var subQ5=sQuery(id+"F4.wireOp",EDGE,"E419");var subQ6=sQuery(id+"F4.wireOp",EDGE,"E418");var subQ7=sQuery(id+"F4.wireOp",EDGE,"E417");var subQ8=sQuery(id+"F4.wireOp",EDGE,"E416");var subQ9=sQuery(id+"F4.wireOp",EDGE,"E415");var subQ10=sQuery(id+"F4.wireOp",EDGE,"E414");var subQ11=sQuery(id+"F4.wireOp",EDGE,"E413");var subQ12=sQuery(id+"F4.wireOp",EDGE,"E412");var subQ13=sQuery(id+"F4.wireOp",EDGE,"E411");var subQ14=sQuery(id+"F4.wireOp",EDGE,"E410");var subQ15=sQuery(id+"F4.wireOp",EDGE,"E409");var subQ16=sQuery(id+"F4.wireOp",EDGE,"E408");var subQ17=sQuery(id+"F4.wireOp",EDGE,"E407");var subQ18=sQuery(id+"F4.wireOp",EDGE,"E406");var subQ19=sQuery(id+"F4.wireOp",EDGE,"E405");var subQ20=sQuery(id+"F4.wireOp",EDGE,"E404");var subQ21=sQuery(id+"F4.wireOp",EDGE,"E403");var subQ22=sQuery(id+"F4.wireOp",EDGE,"E402");var subQ23=sQuery(id+"F4.wireOp",EDGE,"E401");var subQ24=sQuery(id+"F4.wireOp",EDGE,"E400");var subQ25=sQuery(id+"F4.wireOp",EDGE,"E399");var subQ26=sQuery(id+"F4.wireOp",EDGE,"E398");var subQ27=sQuery(id+"F4.wireOp",EDGE,"E397");var subQ28=sQuery(id+"F4.wireOp",EDGE,"E396");var subQ29=sQuery(id+"F4.wireOp",EDGE,"E395");var subQ30=sQuery(id+"F4.wireOp",EDGE,"E394");var subQ31=sQuery(id+"F4.wireOp",EDGE,"E393");var subQ32=sQuery(id+"F4.wireOp",EDGE,"E392");var subQ33=sQuery(id+"F4.wireOp",EDGE,"E391");var subQ34=sQuery(id+"F4.wireOp",EDGE,"E390");var subQ35=sQuery(id+"F4.wireOp",EDGE,"E389");var subQ36=sQuery(id+"F4.wireOp",EDGE,"E388");var subQ37=sQuery(id+"F4.wireOp",EDGE,"E387");var subQ38=sQuery(id+"F4.wireOp",EDGE,"E386");var subQ39=sQuery(id+"F4.wireOp",EDGE,"E385");var subQ41=sQuery(id+"F4.wireOp",EDGE,"E384");var subQ43=sQuery(id+"F4.wireOp",EDGE,"E383");var subQ45=sQuery(id+"F4.wireOp",EDGE,"E382");var subQ47=sQuery(id+"F4.wireOp",EDGE,"E381");var subQ49=sQuery(id+"F4.wireOp",EDGE,"E380");var subQ51=sQuery(id+"F4.wireOp",EDGE,"E379");var subQ53=sQuery(id+"F4.wireOp",EDGE,"E378");var subQ55=sQuery(id+"F4.wireOp",EDGE,"E377");var subQ57=sQuery(id+"F4.wireOp",EDGE,"E376");var subQ59=sQuery(id+"F4.wireOp",EDGE,"E375");var subQ61=sQuery(id+"F4.wireOp",EDGE,"E374");var subQ63=sQuery(id+"F4.wireOp",EDGE,"E373");var subQ65=sQuery(id+"F4.wireOp",EDGE,"E372");var subQ67=sQuery(id+"F4.wireOp",EDGE,"E371");var subQ69=sQuery(id+"F4.wireOp",EDGE,"E370");var subQ71=sQuery(id+"F4.wireOp",EDGE,"E369");var subQ73=sQuery(id+"F4.wireOp",EDGE,"E368");var subQ75=sQuery(id+"F4.wireOp",EDGE,"E367");var subQ77=sQuery(id+"F4.wireOp",EDGE,"E366");var subQ79=sQuery(id+"F4.wireOp",EDGE,"E365");var subQ81=sQuery(id+"F4.wireOp",EDGE,"E364");var subQ83=sQuery(id+"F4.wireOp",EDGE,"E363");var subQ85=sQuery(id+"F4.wireOp",EDGE,"E362");var subQ87=sQuery(id+"F4.wireOp",EDGE,"E361");var subQ89=sQuery(id+"F4.wireOp",EDGE,"E360");var subQ91=sQuery(id+"F4.wireOp",EDGE,"E359");var subQ93=sQuery(id+"F4.wireOp",EDGE,"E358");var subQ95=sQuery(id+"F4.wireOp",EDGE,"E357");var subQ97=sQuery(id+"F4.wireOp",EDGE,"E356");var subQ99=sQuery(id+"F4.wireOp",EDGE,"E355");var subQ101=sQuery(id+"F4.wireOp",EDGE,"E354");var subQ103=sQuery(id+"F4.wireOp",EDGE,"E353");var subQ105=sQuery(id+"F4.wireOp",EDGE,"E352");var subQ107=sQuery(id+"F4.wireOp",EDGE,"E351");var subQ109=sQuery(id+"F4.wireOp",EDGE,"E350");var subQ111=sQuery(id+"F4.wireOp",EDGE,"E349");var subQ113=sQuery(id+"F4.wireOp",EDGE,"E348");var subQ115=sQuery(id+"F4.wireOp",EDGE,"E347");var subQ117=sQuery(id+"F4.wireOp",EDGE,"E346");var subQ119=sQuery(id+"F4.wireOp",EDGE,"E345");var subQ121=sQuery(id+"F4.wireOp",EDGE,"E344");var subQ122=sQuery(id+"F4.wireOp",EDGE,"E343");var subQ134=sQuery(id+"F4.wireOp",EDGE,"E342");var subQ135=sQuery(id+"F4.wireOp",EDGE,"E341");var subQ136=sQuery(id+"F4.wireOp",EDGE,"E340");var subQ137=sQuery(id+"F4.wireOp",EDGE,"E339");var subQ138=sQuery(id+"F4.wireOp",EDGE,"E338");var subQ139=sQuery(id+"F4.wireOp",EDGE,"E337");var subQ140=sQuery(id+"F4.wireOp",EDGE,"E336");var subQ141=sQuery(id+"F4.wireOp",EDGE,"E335");var subQ142=sQuery(id+"F4.wireOp",EDGE,"E334");var subQ143=sQuery(id+"F4.wireOp",EDGE,"E333");var subQ144=sQuery(id+"F4.wireOp",EDGE,"E332");var subQ145=sQuery(id+"F4.wireOp",EDGE,"E331");var subQ146=sQuery(id+"F4.wireOp",EDGE,"E330");var subQ147=sQuery(id+"F4.wireOp",EDGE,"E329");var subQ148=sQuery(id+"F4.wireOp",EDGE,"E328");var subQ149=sQuery(id+"F4.wireOp",EDGE,"E327");var subQ150=sQuery(id+"F4.wireOp",EDGE,"E326");var subQ151=sQuery(id+"F4.wireOp",EDGE,"E325");var subQ152=sQuery(id+"F4.wireOp",EDGE,"E324");var subQ153=sQuery(id+"F4.wireOp",EDGE,"E323");var subQ154=sQuery(id+"F4.wireOp",EDGE,"E322");var subQ155=sQuery(id+"F4.wireOp",EDGE,"E321");var subQ156=sQuery(id+"F4.wireOp",EDGE,"E320");var subQ157=sQuery(id+"F4.wireOp",EDGE,"E319");var subQ158=sQuery(id+"F4.wireOp",EDGE,"E318");var subQ159=sQuery(id+"F4.wireOp",EDGE,"E317");var subQ160=sQuery(id+"F4.wireOp",EDGE,"E316");var subQ161=sQuery(id+"F4.wireOp",EDGE,"E315");var subQ162=sQuery(id+"F4.wireOp",EDGE,"E314");var subQ163=sQuery(id+"F4.wireOp",EDGE,"E313");var subQ164=sQuery(id+"F4.wireOp",EDGE,"E312");var subQ165=sQuery(id+"F4.wireOp",EDGE,"E311");var subQ166=sQuery(id+"F4.wireOp",EDGE,"E310");var subQ167=sQuery(id+"F4.wireOp",EDGE,"E309");var subQ168=sQuery(id+"F4.wireOp",EDGE,"E308");var subQ169=sQuery(id+"F4.wireOp",EDGE,"E307");var subQ170=sQuery(id+"F4.wireOp",EDGE,"E306");var subQ171=sQuery(id+"F4.wireOp",EDGE,"E305");var subQ172=sQuery(id+"F4.wireOp",EDGE,"E304");var subQ173=sQuery(id+"F4.wireOp",EDGE,"E303");var subQ174=sQuery(id+"F4.wireOp",EDGE,"E302");var subQ175=sQuery(id+"F4.wireOp",EDGE,"E292");var subQ176=sQuery(id+"F4.wireOp",EDGE,"E291");var subQ177=sQuery(id+"F4.wireOp",EDGE,"E184");var subQ178=sQuery(id+"F4.wireOp",EDGE,"E183");var subQ179=sQuery(id+"F4.wireOp",EDGE,"E182");var subQ180=sQuery(id+"F4.wireOp",EDGE,"E181");var subQ181=sQuery(id+"F4.wireOp",EDGE,"E180");var subQ182=sQuery(id+"F4.wireOp",EDGE,"E179");var subQ183=sQuery(id+"F4.wireOp",EDGE,"E178");var subQ184=sQuery(id+"F4.wireOp",EDGE,"E177");var subQ185=sQuery(id+"F4.wireOp",EDGE,"E176");var subQ186=sQuery(id+"F4.wireOp",EDGE,"E175");var subQ187=sQuery(id+"F4.wireOp",EDGE,"E174");var subQ188=sQuery(id+"F4.wireOp",EDGE,"E77");var subQ189=sQuery(id+"F4.wireOp",EDGE,"E277");var subQ190=sQuery(id+"F4.wireOp",EDGE,"E173");var subQ191=sQuery(id+"F4.wireOp",EDGE,"E76");var subQ192=sQuery(id+"F4.wireOp",EDGE,"E276");var subQ193=sQuery(id+"F4.wireOp",EDGE,"E172");var subQ194=sQuery(id+"F4.wireOp",EDGE,"E75");var subQ195=sQuery(id+"F4.wireOp",EDGE,"E275");var subQ196=sQuery(id+"F4.wireOp",EDGE,"E171");var subQ197=sQuery(id+"F4.wireOp",EDGE,"E74");var subQ198=sQuery(id+"F4.wireOp",EDGE,"E274");var subQ199=sQuery(id+"F4.wireOp",EDGE,"E170");var subQ200=sQuery(id+"F4.wireOp",EDGE,"E73");var subQ201=sQuery(id+"F4.wireOp",EDGE,"E273");var subQ202=sQuery(id+"F4.wireOp",EDGE,"E169");var subQ203=sQuery(id+"F4.wireOp",EDGE,"E72");var subQ204=sQuery(id+"F4.wireOp",EDGE,"E272");var subQ205=sQuery(id+"F4.wireOp",EDGE,"E168");var subQ206=sQuery(id+"F4.wireOp",EDGE,"E71");var subQ207=sQuery(id+"F4.wireOp",EDGE,"E271");var subQ208=sQuery(id+"F4.wireOp",EDGE,"E167");var subQ209=sQuery(id+"F4.wireOp",EDGE,"E70");var subQ210=sQuery(id+"F4.wireOp",EDGE,"E270");var subQ211=sQuery(id+"F4.wireOp",EDGE,"E166");var subQ212=sQuery(id+"F4.wireOp",EDGE,"E69");var subQ213=sQuery(id+"F4.wireOp",EDGE,"E269");var subQ214=sQuery(id+"F4.wireOp",EDGE,"E165");var subQ215=sQuery(id+"F4.wireOp",EDGE,"E68");var subQ216=sQuery(id+"F4.wireOp",EDGE,"E268");var subQ217=sQuery(id+"F4.wireOp",EDGE,"E164");var subQ218=sQuery(id+"F4.wireOp",EDGE,"E67");var subQ219=sQuery(id+"F4.wireOp",EDGE,"E267");var subQ220=sQuery(id+"F4.wireOp",EDGE,"E66");var subQ221=sQuery(id+"F4.wireOp",EDGE,"E266");var subQ222=sQuery(id+"F4.wireOp",EDGE,"E65");var subQ223=sQuery(id+"F4.wireOp",EDGE,"E265");var subQ224=sQuery(id+"F4.wireOp",EDGE,"E64");var subQ225=sQuery(id+"F4.wireOp",EDGE,"E264");var subQ226=sQuery(id+"F4.wireOp",EDGE,"E63");var subQ227=sQuery(id+"F4.wireOp",EDGE,"E263");var subQ228=sQuery(id+"F4.wireOp",EDGE,"E62");var subQ229=sQuery(id+"F4.wireOp",EDGE,"E262");var subQ230=sQuery(id+"F4.wireOp",EDGE,"E61");var subQ231=sQuery(id+"F4.wireOp",EDGE,"E261");var subQ232=sQuery(id+"F4.wireOp",EDGE,"E60");var subQ233=sQuery(id+"F4.wireOp",EDGE,"E260");var subQ234=sQuery(id+"F4.wireOp",EDGE,"E59");var subQ235=sQuery(id+"F4.wireOp",EDGE,"E259");var subQ236=sQuery(id+"F4.wireOp",EDGE,"E58");var subQ237=sQuery(id+"F4.wireOp",EDGE,"E258");var subQ238=sQuery(id+"F4.wireOp",EDGE,"E57");var subQ239=sQuery(id+"F4.wireOp",EDGE,"E257");var subQ240=sQuery(id+"F4.wireOp",EDGE,"E56");var subQ241=sQuery(id+"F4.wireOp",EDGE,"E256");var subQ242=sQuery(id+"F4.wireOp",EDGE,"E55");var subQ243=sQuery(id+"F4.wireOp",EDGE,"E255");var subQ244=sQuery(id+"F4.wireOp",EDGE,"E54");var subQ245=sQuery(id+"F4.wireOp",EDGE,"E254");var subQ246=sQuery(id+"F4.wireOp",EDGE,"E53");var subQ247=sQuery(id+"F4.wireOp",EDGE,"E253");var subQ248=sQuery(id+"F4.wireOp",EDGE,"E52");var subQ249=sQuery(id+"F4.wireOp",EDGE,"E252");var subQ250=sQuery(id+"F4.wireOp",EDGE,"E51");var subQ251=sQuery(id+"F4.wireOp",EDGE,"E251");var subQ252=sQuery(id+"F4.wireOp",EDGE,"E50");var subQ253=sQuery(id+"F4.wireOp",EDGE,"E250");var subQ254=sQuery(id+"F4.wireOp",EDGE,"E49");var subQ255=sQuery(id+"F4.wireOp",EDGE,"E249");var subQ256=sQuery(id+"F4.wireOp",EDGE,"E22");var subQ257=sQuery(id+"F4.wireOp",EDGE,"E21");var subQ258=sQuery(id+"F4.wireOp",EDGE,"E222");var subQ259=sQuery(id+"F4.wireOp",EDGE,"E20");var subQ260=sQuery(id+"F4.wireOp",EDGE,"E221");var subQ261=sQuery(id+"F4.wireOp",EDGE,"E19");var subQ262=sQuery(id+"F4.wireOp",EDGE,"E220");var subQ263=sQuery(id+"F4.wireOp",EDGE,"E18");var subQ264=sQuery(id+"F4.wireOp",EDGE,"E218");var subQ265=sQuery(id+"F4.wireOp",EDGE,"E17");var subQ266=sQuery(id+"F4.wireOp",EDGE,"E217");var subQ267=sQuery(id+"F4.wireOp",EDGE,"E16");var subQ268=sQuery(id+"F4.wireOp",EDGE,"E216");var subQ269=sQuery(id+"F4.wireOp",EDGE,"E15");var subQ270=sQuery(id+"F4.wireOp",EDGE,"E215");var subQ271=sQuery(id+"F4.wireOp",EDGE,"E14");var subQ272=sQuery(id+"F4.wireOp",EDGE,"E214");var subQ273=sQuery(id+"F4.wireOp",EDGE,"E13");var subQ274=sQuery(id+"F4.wireOp",EDGE,"E213");var subQ275=sQuery(id+"F4.wireOp",EDGE,"E12");var subQ276=sQuery(id+"F4.wireOp",EDGE,"E212");var subQ277=sQuery(id+"F4.wireOp",EDGE,"E427");var subQ278=sQuery(id+"F4.wireOp",EDGE,"E4");var subQ279=sQuery(id+"F4.wireOp",EDGE,"E204");var subQ280=sQuery(id+"F4.wireOp",EDGE,"E426");var subQ281=sQuery(id+"F4.wireOp",EDGE,"E3");var subQ282=sQuery(id+"F4.wireOp",EDGE,"E203");var subQ283=sQuery(id+"F4.wireOp",EDGE,"E5");var subQ284=sQuery(id+"F4.wireOp",EDGE,"E205");var subQ285=sQuery(id+"F4.wireOp",EDGE,"E23");var subQ286=sQuery(id+"F4.wireOp",EDGE,"E422");var subQ287=sQuery(id+"F4.wireOp",EDGE,"E2");var subQ288=sQuery(id+"F4.wireOp",EDGE,"E200");var subQ289=sQuery(id+"F4.wireOp",EDGE,"E48");var subQ290=sQuery(id+"F4.wireOp",EDGE,"E248");var subQ291=sQuery(id+"F4.wireOp",EDGE,"E11");var subQ292=sQuery(id+"F4.wireOp",EDGE,"E211");var subQ293=sQuery(id+"F4.wireOp",EDGE,"E6");var subQ294=sQuery(id+"F4.wireOp",EDGE,"E206");var subQ295=sQuery(id+"F4.wireOp",EDGE,"E7");var subQ296=sQuery(id+"F4.wireOp",EDGE,"E207");var subQ297=sQuery(id+"F4.wireOp",EDGE,"E8");var subQ298=sQuery(id+"F4.wireOp",EDGE,"E208");var subQ299=sQuery(id+"F4.wireOp",EDGE,"E9");var subQ300=sQuery(id+"F4.wireOp",EDGE,"E209");var subQ301=sQuery(id+"F4.wireOp",EDGE,"E10");var subQ302=sQuery(id+"F4.wireOp",EDGE,"E210");var subQ303=sQuery(id+"F4.wireOp",EDGE,"E24");var subQ304=sQuery(id+"F4.wireOp",EDGE,"E25");var subQ305=sQuery(id+"F4.wireOp",EDGE,"E226");var subQ306=sQuery(id+"F4.wireOp",EDGE,"E26");var subQ307=sQuery(id+"F4.wireOp",EDGE,"E227");var subQ308=sQuery(id+"F4.wireOp",EDGE,"E27");var subQ309=sQuery(id+"F4.wireOp",EDGE,"E228");var subQ310=sQuery(id+"F4.wireOp",EDGE,"E28");var subQ311=sQuery(id+"F4.wireOp",EDGE,"E229");var subQ312=sQuery(id+"F4.wireOp",EDGE,"E29");var subQ313=sQuery(id+"F4.wireOp",EDGE,"E230");var subQ314=sQuery(id+"F4.wireOp",EDGE,"E30");var subQ315=sQuery(id+"F4.wireOp",EDGE,"E231");var subQ316=sQuery(id+"F4.wireOp",EDGE,"E31");var subQ317=sQuery(id+"F4.wireOp",EDGE,"E232");var subQ318=sQuery(id+"F4.wireOp",EDGE,"E32");var subQ319=sQuery(id+"F4.wireOp",EDGE,"E233");var subQ320=sQuery(id+"F4.wireOp",EDGE,"E33");var subQ321=sQuery(id+"F4.wireOp",EDGE,"E234");var subQ322=sQuery(id+"F4.wireOp",EDGE,"E34");var subQ323=sQuery(id+"F4.wireOp",EDGE,"E235");var subQ324=sQuery(id+"F4.wireOp",EDGE,"E35");var subQ325=sQuery(id+"F4.wireOp",EDGE,"E236");var subQ326=sQuery(id+"F4.wireOp",EDGE,"E36");var subQ327=sQuery(id+"F4.wireOp",EDGE,"E237");var subQ328=sQuery(id+"F4.wireOp",EDGE,"E37");var subQ329=sQuery(id+"F4.wireOp",EDGE,"E238");var subQ330=sQuery(id+"F4.wireOp",EDGE,"E38");var subQ331=sQuery(id+"F4.wireOp",EDGE,"E239");var subQ332=sQuery(id+"F4.wireOp",EDGE,"E39");var subQ333=sQuery(id+"F4.wireOp",EDGE,"E240");var subQ334=sQuery(id+"F4.wireOp",EDGE,"E40");var subQ335=sQuery(id+"F4.wireOp",EDGE,"E241");var subQ336=sQuery(id+"F4.wireOp",EDGE,"E41");var subQ337=sQuery(id+"F4.wireOp",EDGE,"E242");var subQ338=sQuery(id+"F4.wireOp",EDGE,"E43");var subQ339=sQuery(id+"F4.wireOp",EDGE,"E42");var subQ340=sQuery(id+"F4.wireOp",EDGE,"E243");var subQ341=sQuery(id+"F4.wireOp",EDGE,"E44");var subQ342=sQuery(id+"F4.wireOp",EDGE,"E244");var subQ343=sQuery(id+"F4.wireOp",EDGE,"E45");var subQ344=sQuery(id+"F4.wireOp",EDGE,"E245");var subQ345=sQuery(id+"F4.wireOp",EDGE,"E46");var subQ346=sQuery(id+"F4.wireOp",EDGE,"E246");var subQ347=sQuery(id+"F4.wireOp",EDGE,"E47");var subQ348=sQuery(id+"F4.wireOp",EDGE,"E247");var subQ349=sQuery(id+"F4.wireOp",EDGE,"E185");var subQ350=sQuery(id+"F4.wireOp",EDGE,"E186");var subQ351=sQuery(id+"F4.wireOp",EDGE,"E187");var subQ352=sQuery(id+"F4.wireOp",EDGE,"E188");var subQ353=sQuery(id+"F4.wireOp",EDGE,"E189");var subQ354=sQuery(id+"F4.wireOp",EDGE,"E190");var subQ355=sQuery(id+"F4.wireOp",EDGE,"E191");var subQ356=sQuery(id+"F4.wireOp",EDGE,"E192");var subQ357=sQuery(id+"F4.wireOp",EDGE,"E193");var subQ358=sQuery(id+"F4.wireOp",EDGE,"E194");var subQ359=sQuery(id+"F4.wireOp",EDGE,"E195");var subQ360=sQuery(id+"F4.wireOp",EDGE,"E196");var subQ361=sQuery(id+"F4.wireOp",EDGE,"E197");var subQ362=sQuery(id+"F4.wireOp",EDGE,"E198");var subQ363=sQuery(id+"F4.wireOp",EDGE,"E199");var subQ364=sQuery(id+"F4.wireOp",EDGE,"E201");var subQ365=sQuery(id+"F4.wireOp",EDGE,"E202");var subQ366=sQuery(id+"F4.wireOp",EDGE,"E278");var subQ367=sQuery(id+"F4.wireOp",EDGE,"E279");var subQ368=sQuery(id+"F4.wireOp",EDGE,"E280");var subQ369=sQuery(id+"F4.wireOp",EDGE,"E281");var subQ370=sQuery(id+"F4.wireOp",EDGE,"E282");var subQ371=sQuery(id+"F4.wireOp",EDGE,"E283");var subQ372=sQuery(id+"F4.wireOp",EDGE,"E284");var subQ373=sQuery(id+"F4.wireOp",EDGE,"E285");var subQ374=sQuery(id+"F4.wireOp",EDGE,"E286");var subQ375=sQuery(id+"F4.wireOp",EDGE,"E287");var subQ376=sQuery(id+"F4.wireOp",EDGE,"E288");var subQ377=sQuery(id+"F4.wireOp",EDGE,"E289");var subQ378=sQuery(id+"F4.wireOp",EDGE,"E290");Q0=makeQuery(id+"F11.boolean.opBoolean","SPLIT",FACE,{"disambiguationData":[TD([makeQuery(id+"F5.opExtrude","SWEPT_FACE",FACE,{"disambiguationData":[OSD([subQ287])]})])],"derivedFrom":makeQuery(id+"F5.opExtrude","CAP_FACE",FACE,{"disambiguationData":[OSD([subQ287,subQ281,subQ278,subQ283,subQ293,subQ295,subQ297,subQ299,subQ301,subQ291,subQ275,subQ273,subQ271,subQ269,subQ267,subQ265,subQ263,subQ261,subQ259,subQ257,subQ256,subQ285,subQ303,subQ304,subQ306,subQ308,subQ310,subQ312,subQ314,subQ316,subQ318,subQ320,subQ322,subQ324,subQ326,subQ328,subQ330,subQ332,subQ334,subQ336,subQ339,subQ338,subQ341,subQ343,subQ345,subQ347,subQ289,subQ254,subQ252,subQ250,subQ248,subQ246,subQ244,subQ242,subQ240,subQ238,subQ236,subQ234,subQ232,subQ230,subQ228,subQ226,subQ224,subQ222,subQ220,subQ218,subQ215,subQ212,subQ209,subQ206,subQ203,subQ200,subQ197,subQ194,subQ191,subQ188,sQuery(id+"F4.wireOp",EDGE,"E78"),sQuery(id+"F4.wireOp",EDGE,"E79"),sQuery(id+"F4.wireOp",EDGE,"E80"),sQuery(id+"F4.wireOp",EDGE,"E81"),sQuery(id+"F4.wireOp",EDGE,"E82"),sQuery(id+"F4.wireOp",EDGE,"E83"),sQuery(id+"F4.wireOp",EDGE,"E84"),sQuery(id+"F4.wireOp",EDGE,"E85"),sQuery(id+"F4.wireOp",EDGE,"E86"),sQuery(id+"F4.wireOp",EDGE,"E87"),sQuery(id+"F4.wireOp",EDGE,"E88"),sQuery(id+"F4.wireOp",EDGE,"E89"),sQuery(id+"F4.wireOp",EDGE,"E90"),sQuery(id+"F4.wireOp",EDGE,"E91"),sQuery(id+"F4.wireOp",EDGE,"E92"),sQuery(id+"F4.wireOp",EDGE,"E93"),sQuery(id+"F4.wireOp",EDGE,"E94"),sQuery(id+"F4.wireOp",EDGE,"E95"),sQuery(id+"F4.wireOp",EDGE,"E96"),sQuery(id+"F4.wireOp",EDGE,"E97"),sQuery(id+"F4.wireOp",EDGE,"E98"),sQuery(id+"F4.wireOp",EDGE,"E99"),sQuery(id+"F4.wireOp",EDGE,"E100"),sQuery(id+"F4.wireOp",EDGE,"E101"),sQuery(id+"F4.wireOp",EDGE,"E102"),sQuery(id+"F4.wireOp",EDGE,"E103"),sQuery(id+"F4.wireOp",EDGE,"E104"),sQuery(id+"F4.wireOp",EDGE,"E105"),sQuery(id+"F4.wireOp",EDGE,"E106"),sQuery(id+"F4.wireOp",EDGE,"E107"),sQuery(id+"F4.wireOp",EDGE,"E108"),sQuery(id+"F4.wireOp",EDGE,"E109"),sQuery(id+"F4.wireOp",EDGE,"E110"),sQuery(id+"F4.wireOp",EDGE,"E111"),sQuery(id+"F4.wireOp",EDGE,"E112"),sQuery(id+"F4.wireOp",EDGE,"E113"),sQuery(id+"F4.wireOp",EDGE,"E114"),sQuery(id+"F4.wireOp",EDGE,"E115"),sQuery(id+"F4.wireOp",EDGE,"E116"),sQuery(id+"F4.wireOp",EDGE,"E117"),sQuery(id+"F4.wireOp",EDGE,"E118"),sQuery(id+"F4.wireOp",EDGE,"E119"),sQuery(id+"F4.wireOp",EDGE,"E120"),sQuery(id+"F4.wireOp",EDGE,"E121"),sQuery(id+"F4.wireOp",EDGE,"E122"),sQuery(id+"F4.wireOp",EDGE,"E123"),sQuery(id+"F4.wireOp",EDGE,"E124"),sQuery(id+"F4.wireOp",EDGE,"E125"),sQuery(id+"F4.wireOp",EDGE,"E126"),sQuery(id+"F4.wireOp",EDGE,"E127"),sQuery(id+"F4.wireOp",EDGE,"E128"),sQuery(id+"F4.wireOp",EDGE,"E129"),sQuery(id+"F4.wireOp",EDGE,"E130"),sQuery(id+"F4.wireOp",EDGE,"E131"),sQuery(id+"F4.wireOp",EDGE,"E132"),sQuery(id+"F4.wireOp",EDGE,"E133"),sQuery(id+"F4.wireOp",EDGE,"E134"),sQuery(id+"F4.wireOp",EDGE,"E135"),sQuery(id+"F4.wireOp",EDGE,"E136"),sQuery(id+"F4.wireOp",EDGE,"E137"),sQuery(id+"F4.wireOp",EDGE,"E138"),sQuery(id+"F4.wireOp",EDGE,"E139"),sQuery(id+"F4.wireOp",EDGE,"E140"),sQuery(id+"F4.wireOp",EDGE,"E141"),sQuery(id+"F4.wireOp",EDGE,"E142"),sQuery(id+"F4.wireOp",EDGE,"E143"),sQuery(id+"F4.wireOp",EDGE,"E144"),sQuery(id+"F4.wireOp",EDGE,"E145"),sQuery(id+"F4.wireOp",EDGE,"E146"),sQuery(id+"F4.wireOp",EDGE,"E147"),sQuery(id+"F4.wireOp",EDGE,"E148"),sQuery(id+"F4.wireOp",EDGE,"E149"),sQuery(id+"F4.wireOp",EDGE,"E150"),sQuery(id+"F4.wireOp",EDGE,"E151"),sQuery(id+"F4.wireOp",EDGE,"E152"),sQuery(id+"F4.wireOp",EDGE,"E153"),sQuery(id+"F4.wireOp",EDGE,"E154"),sQuery(id+"F4.wireOp",EDGE,"E155"),sQuery(id+"F4.wireOp",EDGE,"E156"),sQuery(id+"F4.wireOp",EDGE,"E157"),sQuery(id+"F4.wireOp",EDGE,"E158"),sQuery(id+"F4.wireOp",EDGE,"E159"),sQuery(id+"F4.wireOp",EDGE,"E160"),sQuery(id+"F4.wireOp",EDGE,"E161"),sQuery(id+"F4.wireOp",EDGE,"E162"),sQuery(id+"F4.wireOp",EDGE,"E163"),subQ217,subQ214,subQ211,subQ208,subQ205,subQ202,subQ199,subQ196,subQ193,subQ190,subQ187,subQ186,subQ185,subQ184,subQ183,subQ182,subQ181,subQ180,subQ179,subQ178,subQ177,subQ349,subQ350,subQ351,subQ352,subQ353,subQ354,subQ355,subQ356,subQ357,subQ358,subQ359,subQ360,subQ361,subQ362,subQ363,subQ288,subQ364,subQ365,subQ282,subQ279,subQ284,subQ294,subQ296,subQ298,subQ300,subQ302,subQ292,subQ276,subQ274,subQ272,subQ270,subQ268,subQ266,subQ264,subQ262,subQ260,subQ258,sQuery(id+"F4.wireOp",EDGE,"E223"),sQuery(id+"F4.wireOp",EDGE,"E224"),sQuery(id+"F4.wireOp",EDGE,"E225"),subQ305,subQ307,subQ309,subQ311,subQ313,subQ315,subQ317,subQ319,subQ321,subQ323,subQ325,subQ327,subQ329,subQ331,subQ333,subQ335,subQ337,subQ340,subQ342,subQ344,subQ346,subQ348,subQ290,subQ255,subQ253,subQ251,subQ249,subQ247,subQ245,subQ243,subQ241,subQ239,subQ237,subQ235,subQ233,subQ231,subQ229,subQ227,subQ225,subQ223,subQ221,subQ219,subQ216,subQ213,subQ210,subQ207,subQ204,subQ201,subQ198,subQ195,subQ192,subQ189,subQ366,subQ367,subQ368,subQ369,subQ370,subQ371,subQ372,subQ373,subQ374,subQ375,subQ376,subQ377,subQ378,subQ176,subQ175,subQ174,subQ173,subQ172,subQ171,subQ170,subQ169,subQ168,subQ167,subQ166,subQ165,subQ164,subQ163,subQ162,subQ161,subQ160,subQ159,subQ158,subQ157,subQ156,subQ155,subQ154,subQ153,subQ152,subQ151,subQ150,subQ149,subQ148,subQ147,subQ146,subQ145,subQ144,subQ143,subQ142,subQ141,subQ140,subQ139,subQ138,subQ137,subQ136,subQ135,subQ134,subQ122,subQ121,subQ119,subQ117,subQ115,subQ113,subQ111,subQ109,subQ107,subQ105,subQ103,subQ101,subQ99,subQ97,subQ95,subQ93,subQ91,subQ89,subQ87,subQ85,subQ83,subQ81,subQ79,subQ77,subQ75,subQ73,subQ71,subQ69,subQ67,subQ65,subQ63,subQ61,subQ59,subQ57,subQ55,subQ53,subQ51,subQ49,subQ47,subQ45,subQ43,subQ41,subQ39,subQ38,subQ37,subQ36,subQ35,subQ34,subQ33,subQ32,subQ31,subQ30,subQ29,subQ28,subQ27,subQ26,subQ25,subQ24,subQ23,subQ22,subQ21,subQ20,subQ19,subQ18,subQ17,subQ16,subQ15,subQ14,subQ13,subQ12,subQ11,subQ10,subQ9,subQ8,subQ7,subQ6,subQ5,subQ4,subQ3,subQ286,subQ2,subQ1,subQ0,subQ280,subQ277])],"isStart":false})});}
            var sketch = newSketch(context, id + "F16", { "sketchPlane" : qUnion([Q0])});
            skLineSegment(sketch, "E1032", {"start": v(23.81, 3.14) * mm, "end": v(23.95, 3.32) * mm});
            skLineSegment(sketch, "E1033", {"start": v(23.95, 3.32) * mm, "end": v(24.16, 3.6) * mm});
            skLineSegment(sketch, "E1034", {"start": v(24.16, 3.6) * mm, "end": v(24.37, 3.86) * mm});
            skLineSegment(sketch, "E1035", {"start": v(24.37, 3.86) * mm, "end": v(24.53, 4.13) * mm});
            skLineSegment(sketch, "E1036", {"start": v(24.53, 4.13) * mm, "end": v(24.74, 4.49) * mm});
            skLineSegment(sketch, "E1037", {"start": v(24.74, 4.49) * mm, "end": v(24.87, 4.88) * mm});
            skLineSegment(sketch, "E1038", {"start": v(24.87, 4.88) * mm, "end": v(24.93, 5.31) * mm});
            skLineSegment(sketch, "E1039", {"start": v(24.93, 5.31) * mm, "end": v(24.91, 5.7) * mm});
            skLineSegment(sketch, "E1040", {"start": v(24.91, 5.7) * mm, "end": v(24.86, 6.06) * mm});
            skLineSegment(sketch, "E1041", {"start": v(24.86, 6.06) * mm, "end": v(24.75, 6.34) * mm});
            skLineSegment(sketch, "E1042", {"start": v(24.75, 6.34) * mm, "end": v(24.64, 6.5) * mm});
            skLineSegment(sketch, "E1043", {"start": v(24.64, 6.5) * mm, "end": v(24.53, 6.72) * mm});
            skLineSegment(sketch, "E1044", {"start": v(24.53, 6.72) * mm, "end": v(24.44, 6.87) * mm});
            skLineSegment(sketch, "E1045", {"start": v(24.44, 6.87) * mm, "end": v(24.36, 7.02) * mm});
            skLineSegment(sketch, "E1046", {"start": v(24.36, 7.02) * mm, "end": v(24.18, 7.3) * mm});
            skLineSegment(sketch, "E1047", {"start": v(24.18, 7.3) * mm, "end": v(23.96, 7.58) * mm});
            skLineSegment(sketch, "E1048", {"start": v(23.96, 7.58) * mm, "end": v(23.68, 7.86) * mm});
            skLineSegment(sketch, "E1049", {"start": v(23.68, 7.86) * mm, "end": v(23.3, 8.2) * mm});
            skLineSegment(sketch, "E1050", {"start": v(23.3, 8.2) * mm, "end": v(23.13, 8.45) * mm});
            skLineSegment(sketch, "E1051", {"start": v(23.13, 8.45) * mm, "end": v(23.07, 8.71) * mm});
            skLineSegment(sketch, "E1052", {"start": v(23.07, 8.71) * mm, "end": v(23.07, 8.94) * mm});
            skLineSegment(sketch, "E1053", {"start": v(23.07, 8.94) * mm, "end": v(23.14, 9.14) * mm});
            skLineSegment(sketch, "E1054", {"start": v(23.14, 9.14) * mm, "end": v(23.22, 9.38) * mm});
            skLineSegment(sketch, "E1055", {"start": v(23.22, 9.38) * mm, "end": v(23.26, 9.54) * mm});
            skLineSegment(sketch, "E1056", {"start": v(23.26, 9.54) * mm, "end": v(23.3, 9.72) * mm});
            skLineSegment(sketch, "E1057", {"start": v(23.3, 9.72) * mm, "end": v(23.3, 9.96) * mm});
            skLineSegment(sketch, "E1058", {"start": v(23.3, 9.96) * mm, "end": v(23.27, 10.2) * mm});
            skLineSegment(sketch, "E1059", {"start": v(23.27, 10.2) * mm, "end": v(23.08, 10.43) * mm});
            skLineSegment(sketch, "E1060", {"start": v(23.08, 10.43) * mm, "end": v(22.83, 10.6) * mm});
            skLineSegment(sketch, "E1061", {"start": v(22.83, 10.6) * mm, "end": v(22.55, 10.64) * mm});
            skLineSegment(sketch, "E1062", {"start": v(22.55, 10.64) * mm, "end": v(22.22, 10.6) * mm});
            skLineSegment(sketch, "E1063", {"start": v(22.22, 10.6) * mm, "end": v(21.98, 10.46) * mm});
            skLineSegment(sketch, "E1064", {"start": v(21.98, 10.46) * mm, "end": v(21.75, 10.3) * mm});
            skLineSegment(sketch, "E1065", {"start": v(21.75, 10.3) * mm, "end": v(21.62, 10.04) * mm});
            skLineSegment(sketch, "E1066", {"start": v(21.62, 10.04) * mm, "end": v(21.45, 9.78) * mm});
            skLineSegment(sketch, "E1067", {"start": v(21.45, 9.78) * mm, "end": v(21.34, 9.4) * mm});
            skLineSegment(sketch, "E1068", {"start": v(21.34, 9.4) * mm, "end": v(21.31, 9.15) * mm});
            skLineSegment(sketch, "E1069", {"start": v(21.31, 9.15) * mm, "end": v(21.3, 8.75) * mm});
            skLineSegment(sketch, "E1070", {"start": v(21.3, 8.75) * mm, "end": v(21.44, 8.36) * mm});
            skLineSegment(sketch, "E1071", {"start": v(21.44, 8.36) * mm, "end": v(21.6, 8) * mm});
            skLineSegment(sketch, "E1072", {"start": v(21.6, 8) * mm, "end": v(21.66, 7.85) * mm});
            skLineSegment(sketch, "E1073", {"start": v(21.66, 7.85) * mm, "end": v(21.4, 7.88) * mm});
            skLineSegment(sketch, "E1074", {"start": v(21.4, 7.88) * mm, "end": v(21.03, 7.85) * mm});
            skLineSegment(sketch, "E1075", {"start": v(21.03, 7.85) * mm, "end": v(20.64, 7.77) * mm});
            skLineSegment(sketch, "E1076", {"start": v(20.64, 7.77) * mm, "end": v(20.37, 7.6) * mm});
            skLineSegment(sketch, "E1077", {"start": v(20.37, 7.6) * mm, "end": v(20.22, 7.45) * mm});
            skLineSegment(sketch, "E1078", {"start": v(20.22, 7.45) * mm, "end": v(20.1, 7.25) * mm});
            skLineSegment(sketch, "E1079", {"start": v(20.1, 7.25) * mm, "end": v(20.03, 6.98) * mm});
            skLineSegment(sketch, "E1080", {"start": v(20.03, 6.98) * mm, "end": v(20.04, 6.75) * mm});
            skLineSegment(sketch, "E1081", {"start": v(20.04, 6.75) * mm, "end": v(20.08, 6.47) * mm});
            skLineSegment(sketch, "E1082", {"start": v(20.08, 6.47) * mm, "end": v(20.3, 6.23) * mm});
            skLineSegment(sketch, "E1083", {"start": v(20.3, 6.23) * mm, "end": v(20.37, 6.07) * mm});
            skLineSegment(sketch, "E1084", {"start": v(20.37, 6.07) * mm, "end": v(20.14, 5.81) * mm});
            skLineSegment(sketch, "E1085", {"start": v(20.14, 5.81) * mm, "end": v(20.07, 5.54) * mm});
            skLineSegment(sketch, "E1086", {"start": v(20.07, 5.54) * mm, "end": v(20.25, 5.26) * mm});
            skLineSegment(sketch, "E1087", {"start": v(20.25, 5.26) * mm, "end": v(20.47, 5) * mm});
            skLineSegment(sketch, "E1088", {"start": v(20.47, 5) * mm, "end": v(20.6, 4.96) * mm});
            skLineSegment(sketch, "E1089", {"start": v(20.6, 4.96) * mm, "end": v(20.5, 4.77) * mm});
            skLineSegment(sketch, "E1090", {"start": v(20.5, 4.77) * mm, "end": v(20.4, 4.56) * mm});
            skLineSegment(sketch, "E1091", {"start": v(20.4, 4.56) * mm, "end": v(20.37, 4.27) * mm});
            skLineSegment(sketch, "E1092", {"start": v(20.37, 4.27) * mm, "end": v(20.5, 4.1) * mm});
            skLineSegment(sketch, "E1093", {"start": v(20.5, 4.1) * mm, "end": v(20.76, 3.8) * mm});
            skLineSegment(sketch, "E1094", {"start": v(20.76, 3.8) * mm, "end": v(21.02, 3.6) * mm});
            skLineSegment(sketch, "E1095", {"start": v(21.02, 3.6) * mm, "end": v(21.38, 3.39) * mm});
            skLineSegment(sketch, "E1096", {"start": v(21.38, 3.39) * mm, "end": v(21.8, 3.28) * mm});
            skLineSegment(sketch, "E1097", {"start": v(21.8, 3.28) * mm, "end": v(22.22, 3.26) * mm});
            skLineSegment(sketch, "E1098", {"start": v(22.22, 3.26) * mm, "end": v(22.61, 3.24) * mm});
            skLineSegment(sketch, "E1099", {"start": v(22.61, 3.24) * mm, "end": v(22.89, 3.25) * mm});
            skLineSegment(sketch, "E1100", {"start": v(22.89, 3.25) * mm, "end": v(23.07, 3.2) * mm});
            skLineSegment(sketch, "E1101", {"start": v(23.07, 3.2) * mm, "end": v(23.2, 3.15) * mm});
            skLineSegment(sketch, "E1102", {"start": v(23.2, 3.15) * mm, "end": v(23.36, 3.1) * mm});
            skLineSegment(sketch, "E1103", {"start": v(23.36, 3.1) * mm, "end": v(23.6, 3.08) * mm});
            skLineSegment(sketch, "E1104", {"start": v(23.6, 3.08) * mm, "end": v(23.72, 3.1) * mm});
            skLineSegment(sketch, "E1105", {"start": v(23.72, 3.1) * mm, "end": v(23.81, 3.14) * mm});
            skLineSegment(sketch, "E1106", {"start": v(37.17, -1.64) * mm, "end": v(37.33, -1.78) * mm});
            skLineSegment(sketch, "E1107", {"start": v(37.33, -1.78) * mm, "end": v(37.5, -1.96) * mm});
            skLineSegment(sketch, "E1108", {"start": v(37.5, -1.96) * mm, "end": v(37.8, -2.2) * mm});
            skLineSegment(sketch, "E1109", {"start": v(37.8, -2.2) * mm, "end": v(38.08, -2.38) * mm});
            skLineSegment(sketch, "E1110", {"start": v(38.08, -2.38) * mm, "end": v(38.48, -2.5) * mm});
            skLineSegment(sketch, "E1111", {"start": v(38.48, -2.5) * mm, "end": v(38.78, -2.51) * mm});
            skLineSegment(sketch, "E1112", {"start": v(38.78, -2.51) * mm, "end": v(39, -2.58) * mm});
            skLineSegment(sketch, "E1113", {"start": v(39, -2.58) * mm, "end": v(39.1, -2.73) * mm});
            skLineSegment(sketch, "E1114", {"start": v(39.1, -2.73) * mm, "end": v(39.22, -2.83) * mm});
            skLineSegment(sketch, "E1115", {"start": v(39.22, -2.83) * mm, "end": v(39.4, -3) * mm});
            skLineSegment(sketch, "E1116", {"start": v(39.4, -3) * mm, "end": v(39.5, -3.25) * mm});
            skLineSegment(sketch, "E1117", {"start": v(39.5, -3.25) * mm, "end": v(39.57, -3.53) * mm});
            skLineSegment(sketch, "E1118", {"start": v(39.57, -3.53) * mm, "end": v(39.54, -3.76) * mm});
            skLineSegment(sketch, "E1119", {"start": v(39.54, -3.76) * mm, "end": v(39.38, -4.03) * mm});
            skLineSegment(sketch, "E1120", {"start": v(39.38, -4.03) * mm, "end": v(39.22, -4.32) * mm});
            skLineSegment(sketch, "E1121", {"start": v(39.22, -4.32) * mm, "end": v(39.13, -4.41) * mm});
            skLineSegment(sketch, "E1122", {"start": v(39.13, -4.41) * mm, "end": v(39.07, -4.47) * mm});
            skLineSegment(sketch, "E1123", {"start": v(39.07, -4.47) * mm, "end": v(38.96, -4.51) * mm});
            skLineSegment(sketch, "E1124", {"start": v(38.96, -4.51) * mm, "end": v(38.81, -4.51) * mm});
            skLineSegment(sketch, "E1125", {"start": v(38.81, -4.51) * mm, "end": v(38.58, -4.53) * mm});
            skLineSegment(sketch, "E1126", {"start": v(38.58, -4.53) * mm, "end": v(38.24, -4.5) * mm});
            skLineSegment(sketch, "E1127", {"start": v(38.24, -4.5) * mm, "end": v(37.91, -4.5) * mm});
            skLineSegment(sketch, "E1128", {"start": v(37.91, -4.5) * mm, "end": v(37.7, -4.48) * mm});
            skLineSegment(sketch, "E1129", {"start": v(37.7, -4.48) * mm, "end": v(37.5, -4.46) * mm});
            skLineSegment(sketch, "E1130", {"start": v(37.5, -4.46) * mm, "end": v(37.36, -4.44) * mm});
            skLineSegment(sketch, "E1131", {"start": v(37.36, -4.44) * mm, "end": v(37.25, -4.4) * mm});
            skLineSegment(sketch, "E1132", {"start": v(37.25, -4.4) * mm, "end": v(37.1, -4.55) * mm});
            skLineSegment(sketch, "E1133", {"start": v(37.1, -4.55) * mm, "end": v(36.96, -4.12) * mm});
            skLineSegment(sketch, "E1134", {"start": v(36.96, -4.12) * mm, "end": v(36.76, -3.72) * mm});
            skLineSegment(sketch, "E1135", {"start": v(36.76, -3.72) * mm, "end": v(36.65, -3.2) * mm});
            skLineSegment(sketch, "E1136", {"start": v(36.65, -3.2) * mm, "end": v(36.62, -2.87) * mm});
            skLineSegment(sketch, "E1137", {"start": v(36.62, -2.87) * mm, "end": v(36.62, -2.47) * mm});
            skLineSegment(sketch, "E1138", {"start": v(36.62, -2.47) * mm, "end": v(36.65, -2.12) * mm});
            skLineSegment(sketch, "E1139", {"start": v(36.65, -2.12) * mm, "end": v(36.74, -1.96) * mm});
            skLineSegment(sketch, "E1140", {"start": v(36.74, -1.96) * mm, "end": v(36.87, -1.8) * mm});
            skLineSegment(sketch, "E1141", {"start": v(36.87, -1.8) * mm, "end": v(37, -1.7) * mm});
            skLineSegment(sketch, "E1142", {"start": v(37, -1.7) * mm, "end": v(37.1, -1.64) * mm});
            skLineSegment(sketch, "E1143", {"start": v(37.1, -1.64) * mm, "end": v(37.17, -1.64) * mm});
            skSolve(sketch);
        }
        {
            var Q0;
            Q0 = qSketchRegion(id + "F16", true);
            extrude(context, id + "F17", {"entities" : qUnion([Q0]), "operationType" : NewBodyOperationType.REMOVE, "oppositeDirection" : true, "depth" : 0.25 * mm, "offsetDistance" : 25.4 * mm});
        }
        {
            var Q0;
            Q0=makeQuery(id+"F3.imprint","IMPRINT",FACE,{"disambiguationData":[TD([[makeQuery(id+"F3.imprint","IMPRINT",EDGE,{"derivedFrom":sQuery(id+"F3.wireOp",EDGE,"E1.sketch_text.stroke-0")}),-1.0]])]});
            var Q1;
            Q1=makeQuery(id+"F3.imprint","IMPRINT",FACE,{"disambiguationData":[TD([[makeQuery(id+"F3.imprint","IMPRINT",EDGE,{"derivedFrom":sQuery(id+"F3.wireOp",EDGE,"E1.sketch_text.stroke-12")}),-1.0]])]});
            var Q2;
            Q2=makeQuery(id+"F3.imprint","IMPRINT",FACE,{"disambiguationData":[TD([[makeQuery(id+"F3.imprint","IMPRINT",EDGE,{"derivedFrom":sQuery(id+"F3.wireOp",EDGE,"E1.sketch_text.stroke-37")}),-1.0]])]});
            var Q3;
            Q3=makeQuery(id+"F3.imprint","IMPRINT",FACE,{"disambiguationData":[TD([[makeQuery(id+"F3.imprint","IMPRINT",EDGE,{"derivedFrom":sQuery(id+"F3.wireOp",EDGE,"E1.sketch_text.stroke-41")}),-1.0]])]});
            extrude(context, id + "F18", {"entities" : qUnion([Q0, Q1, Q2, Q3]), "operationType" : NewBodyOperationType.REMOVE, "oppositeDirection" : true, "depth" : 1.27 * mm, "offsetDistance" : 25.4 * mm});
        }
        {
            var Q0;
            {var subQ6=sQuery(id+"F0.wireOp",EDGE,"E0.right");var subQ7=sQuery(id+"F0.wireOp",EDGE,"E0.left");var subQ8=sQuery(id+"F0.wireOp",EDGE,"E0.top");var subQ9=sQuery(id+"F0.wireOp",EDGE,"E0.bottom");Q0=makeQuery(id+"F18.boolean.opBoolean","SPLIT",FACE,{"disambiguationData":[TD([makeQuery(id+"F2.opChamfer","BLEND_FACE",FACE,{"disambiguationData":[OSD([subQ9])]})])],"derivedFrom":makeQuery(id+"F1.opExtrude","CAP_FACE",FACE,{"disambiguationData":[OSD([subQ9,subQ8,subQ7,subQ6])],"isStart":false})});}
            var sketch = newSketch(context, id + "F19", { "sketchPlane" : qUnion([Q0])});
            skLineSegment(sketch, "E1144", {"start": v(-39.92, -13.51) * mm, "end": v(-39.92, -2.68) * mm});
            skLineSegment(sketch, "E1145", {"start": v(-39.92, -2.68) * mm, "end": v(-36.1, -2.68) * mm});
            skLineSegment(sketch, "E1146", {"start": v(-36.1, -2.68) * mm, "end": v(-36.06, -2.69) * mm});
            skLineSegment(sketch, "E1147", {"start": v(-36.06, -2.69) * mm, "end": v(-36, -2.71) * mm});
            skLineSegment(sketch, "E1148", {"start": v(-36, -2.71) * mm, "end": v(-35.86, -2.76) * mm});
            skLineSegment(sketch, "E1149", {"start": v(-35.86, -2.76) * mm, "end": v(-35.76, -2.82) * mm});
            skLineSegment(sketch, "E1150", {"start": v(-35.76, -2.82) * mm, "end": v(-35.66, -2.86) * mm});
            skLineSegment(sketch, "E1151", {"start": v(-35.66, -2.86) * mm, "end": v(-35.6, -2.9) * mm});
            skLineSegment(sketch, "E1152", {"start": v(-35.6, -2.9) * mm, "end": v(-35.4, -3.01) * mm});
            skLineSegment(sketch, "E1153", {"start": v(-35.4, -3.01) * mm, "end": v(-35.25, -3.15) * mm});
            skLineSegment(sketch, "E1154", {"start": v(-35.25, -3.15) * mm, "end": v(-35.08, -3.28) * mm});
            skLineSegment(sketch, "E1155", {"start": v(-35.08, -3.28) * mm, "end": v(-34.93, -3.43) * mm});
            skLineSegment(sketch, "E1156", {"start": v(-34.93, -3.43) * mm, "end": v(-34.7, -3.64) * mm});
            skLineSegment(sketch, "E1157", {"start": v(-34.7, -3.64) * mm, "end": v(-34.56, -3.8) * mm});
            skLineSegment(sketch, "E1158", {"start": v(-34.56, -3.8) * mm, "end": v(-34.43, -3.95) * mm});
            skLineSegment(sketch, "E1159", {"start": v(-34.43, -3.95) * mm, "end": v(-34.27, -4.14) * mm});
            skLineSegment(sketch, "E1160", {"start": v(-34.27, -4.14) * mm, "end": v(-34.1, -4.33) * mm});
            skLineSegment(sketch, "E1161", {"start": v(-34.1, -4.33) * mm, "end": v(-33.88, -4.56) * mm});
            skLineSegment(sketch, "E1162", {"start": v(-33.88, -4.56) * mm, "end": v(-33.71, -4.74) * mm});
            skLineSegment(sketch, "E1163", {"start": v(-33.71, -4.74) * mm, "end": v(-33.57, -4.91) * mm});
            skLineSegment(sketch, "E1164", {"start": v(-33.57, -4.91) * mm, "end": v(-33.36, -5.14) * mm});
            skLineSegment(sketch, "E1165", {"start": v(-33.36, -5.14) * mm, "end": v(-33.12, -5.41) * mm});
            skLineSegment(sketch, "E1166", {"start": v(-33.12, -5.41) * mm, "end": v(-32.96, -5.6) * mm});
            skLineSegment(sketch, "E1167", {"start": v(-32.96, -5.6) * mm, "end": v(-32.78, -5.8) * mm});
            skLineSegment(sketch, "E1168", {"start": v(-32.78, -5.8) * mm, "end": v(-32.53, -6.12) * mm});
            skLineSegment(sketch, "E1169", {"start": v(-32.53, -6.12) * mm, "end": v(-32.26, -6.39) * mm});
            skLineSegment(sketch, "E1170", {"start": v(-32.26, -6.39) * mm, "end": v(-31.67, -7.07) * mm});
            skLineSegment(sketch, "E1171", {"start": v(-31.67, -7.07) * mm, "end": v(-31.13, -7.7) * mm});
            skLineSegment(sketch, "E1172", {"start": v(-31.13, -7.7) * mm, "end": v(-30.61, -8.27) * mm});
            skLineSegment(sketch, "E1173", {"start": v(-30.61, -8.27) * mm, "end": v(-29.53, -9.5) * mm});
            skLineSegment(sketch, "E1174", {"start": v(-29.53, -9.5) * mm, "end": v(-28.6, -10.59) * mm});
            skLineSegment(sketch, "E1175", {"start": v(-28.6, -10.59) * mm, "end": v(-28.42, -10.7) * mm});
            skLineSegment(sketch, "E1176", {"start": v(-28.42, -10.7) * mm, "end": v(-28.3, -10.77) * mm});
            skLineSegment(sketch, "E1177", {"start": v(-28.3, -10.77) * mm, "end": v(-28.16, -10.81) * mm});
            skLineSegment(sketch, "E1178", {"start": v(-28.16, -10.81) * mm, "end": v(-28.08, -10.81) * mm});
            skLineSegment(sketch, "E1179", {"start": v(-28.08, -10.81) * mm, "end": v(-28, -10.77) * mm});
            skLineSegment(sketch, "E1180", {"start": v(-28, -10.77) * mm, "end": v(-28, -2.68) * mm});
            skLineSegment(sketch, "E1181", {"start": v(-28, -2.68) * mm, "end": v(-25.28, -2.68) * mm});
            skLineSegment(sketch, "E1182", {"start": v(-25.28, -2.68) * mm, "end": v(-25.28, -13.6) * mm});
            skLineSegment(sketch, "E1183", {"start": v(-25.28, -13.6) * mm, "end": v(-28.98, -13.6) * mm});
            skLineSegment(sketch, "E1184", {"start": v(-28.98, -13.6) * mm, "end": v(-29.17, -13.57) * mm});
            skLineSegment(sketch, "E1185", {"start": v(-29.17, -13.57) * mm, "end": v(-29.35, -13.49) * mm});
            skLineSegment(sketch, "E1186", {"start": v(-29.35, -13.49) * mm, "end": v(-29.63, -13.34) * mm});
            skLineSegment(sketch, "E1187", {"start": v(-29.63, -13.34) * mm, "end": v(-30.07, -13.01) * mm});
            skLineSegment(sketch, "E1188", {"start": v(-30.07, -13.01) * mm, "end": v(-31.62, -11.36) * mm});
            skLineSegment(sketch, "E1189", {"start": v(-31.62, -11.36) * mm, "end": v(-33.08, -9.68) * mm});
            skLineSegment(sketch, "E1190", {"start": v(-33.08, -9.68) * mm, "end": v(-33.52, -9.19) * mm});
            skLineSegment(sketch, "E1191", {"start": v(-33.52, -9.19) * mm, "end": v(-34.11, -8.52) * mm});
            skLineSegment(sketch, "E1192", {"start": v(-34.11, -8.52) * mm, "end": v(-36.7, -5.54) * mm});
            skLineSegment(sketch, "E1193", {"start": v(-36.7, -5.54) * mm, "end": v(-36.83, -5.46) * mm});
            skLineSegment(sketch, "E1194", {"start": v(-36.83, -5.46) * mm, "end": v(-37.02, -5.42) * mm});
            skLineSegment(sketch, "E1195", {"start": v(-37.02, -5.42) * mm, "end": v(-37.2, -5.41) * mm});
            skLineSegment(sketch, "E1196", {"start": v(-37.2, -5.41) * mm, "end": v(-37.2, -13.56) * mm});
            skLineSegment(sketch, "E1197", {"start": v(-37.2, -13.56) * mm, "end": v(-39.92, -13.56) * mm});
            skLineSegment(sketch, "E1198", {"start": v(-24.25, -2.68) * mm, "end": v(-24.25, -5.42) * mm});
            skLineSegment(sketch, "E1199", {"start": v(-24.25, -5.42) * mm, "end": v(-14.8, -5.42) * mm});
            skLineSegment(sketch, "E1200", {"start": v(-14.8, -5.42) * mm, "end": v(-22.9, -13.56) * mm});
            skLineSegment(sketch, "E1201", {"start": v(-22.9, -13.56) * mm, "end": v(-19, -13.56) * mm});
            skLineSegment(sketch, "E1202", {"start": v(-19, -13.56) * mm, "end": v(-10.72, -5.31) * mm});
            skLineSegment(sketch, "E1203", {"start": v(-10.72, -5.31) * mm, "end": v(-10.72, -2.68) * mm});
            skLineSegment(sketch, "E1204", {"start": v(-8.52, -2.68) * mm, "end": v(-5.78, -2.68) * mm});
            skLineSegment(sketch, "E1205", {"start": v(-5.78, -2.68) * mm, "end": v(-5.78, -13.57) * mm});
            skLineSegment(sketch, "E1206", {"start": v(-5.78, -13.57) * mm, "end": v(-16.65, -13.57) * mm});
            skLineSegment(sketch, "E1207", {"start": v(-16.65, -13.57) * mm, "end": v(-8.54, -5.41) * mm});
            skLineSegment(sketch, "E1208", {"start": v(-8.54, -5.41) * mm, "end": v(-8.52, -2.68) * mm});
            skLineSegment(sketch, "E1209", {"start": v(-10.72, -2.68) * mm, "end": v(-24.25, -2.68) * mm});
            skLineSegment(sketch, "E1210", {"start": v(-39.92, -13.51) * mm, "end": v(-39.92, -13.56) * mm});
            skSolve(sketch);
        }
        {
            var Q0;
            Q0 = qSketchRegion(id + "F19", true);
            extrude(context, id + "F20", {"entities" : qUnion([Q0]), "operationType" : NewBodyOperationType.ADD, "depth" : 2.54 * mm, "offsetDistance" : 25.4 * mm});
        }
        {
            var Q0;
            {var subQ6=sQuery(id+"F0.wireOp",EDGE,"E0.right");var subQ7=sQuery(id+"F0.wireOp",EDGE,"E0.left");var subQ8=sQuery(id+"F0.wireOp",EDGE,"E0.top");var subQ9=sQuery(id+"F0.wireOp",EDGE,"E0.bottom");Q0=makeQuery(id+"F18.boolean.opBoolean","SPLIT",FACE,{"disambiguationData":[TD([makeQuery(id+"F2.opChamfer","BLEND_FACE",FACE,{"disambiguationData":[OSD([subQ9])]})])],"derivedFrom":makeQuery(id+"F1.opExtrude","CAP_FACE",FACE,{"disambiguationData":[OSD([subQ9,subQ8,subQ7,subQ6])],"isStart":false})});}
            var sketch = newSketch(context, id + "F21", { "sketchPlane" : qUnion([Q0])});
            skPoint(sketch, "E1211.startSnap0", {"position": v(12.8, -0.6) * mm});
            skPoint(sketch, "E1212.startSnap0", {"position": v(5.28, -8.1) * mm});
            skLineSegment(sketch, "E1213", {"start": v(6.2, -11.7) * mm, "end": v(6.31, -11.9) * mm});
            skLineSegment(sketch, "E1214", {"start": v(6.31, -11.9) * mm, "end": v(6.43, -12.1) * mm});
            skLineSegment(sketch, "E1215", {"start": v(6.43, -12.1) * mm, "end": v(6.54, -12.27) * mm});
            skLineSegment(sketch, "E1216", {"start": v(6.54, -12.27) * mm, "end": v(6.7, -12.5) * mm});
            skLineSegment(sketch, "E1217", {"start": v(6.7, -12.5) * mm, "end": v(6.77, -12.6) * mm});
            skLineSegment(sketch, "E1218", {"start": v(6.77, -12.6) * mm, "end": v(6.87, -12.72) * mm});
            skLineSegment(sketch, "E1219", {"start": v(6.87, -12.72) * mm, "end": v(6.92, -12.79) * mm});
            skLineSegment(sketch, "E1220", {"start": v(6.92, -12.79) * mm, "end": v(7.03, -12.92) * mm});
            skLineSegment(sketch, "E1221", {"start": v(7.03, -12.92) * mm, "end": v(7.1, -13) * mm});
            skLineSegment(sketch, "E1222", {"start": v(7.1, -13) * mm, "end": v(7.18, -13.1) * mm});
            skLineSegment(sketch, "E1223", {"start": v(7.18, -13.1) * mm, "end": v(7.24, -13.17) * mm});
            skLineSegment(sketch, "E1224", {"start": v(7.24, -13.17) * mm, "end": v(7.34, -13.27) * mm});
            skLineSegment(sketch, "E1225", {"start": v(7.34, -13.27) * mm, "end": v(7.4, -13.34) * mm});
            skLineSegment(sketch, "E1226", {"start": v(7.4, -13.34) * mm, "end": v(7.46, -13.4) * mm});
            skLineSegment(sketch, "E1227", {"start": v(7.46, -13.4) * mm, "end": v(7.48, -13.42) * mm});
            skLineSegment(sketch, "E1228", {"start": v(7.48, -13.42) * mm, "end": v(7.52, -13.45) * mm});
            skLineSegment(sketch, "E1229", {"start": v(7.52, -13.45) * mm, "end": v(7.58, -13.51) * mm});
            skLineSegment(sketch, "E1230", {"start": v(7.58, -13.51) * mm, "end": v(7.62, -13.55) * mm});
            skLineSegment(sketch, "E1231", {"start": v(7.62, -13.55) * mm, "end": v(7.65, -13.59) * mm});
            skLineSegment(sketch, "E1232", {"start": v(7.65, -13.59) * mm, "end": v(7.7, -13.63) * mm});
            skLineSegment(sketch, "E1233", {"start": v(7.7, -13.63) * mm, "end": v(7.75, -13.67) * mm});
            skLineSegment(sketch, "E1234", {"start": v(7.75, -13.67) * mm, "end": v(7.8, -13.71) * mm});
            skLineSegment(sketch, "E1235", {"start": v(7.8, -13.71) * mm, "end": v(7.85, -13.76) * mm});
            skLineSegment(sketch, "E1236", {"start": v(7.85, -13.76) * mm, "end": v(7.9, -13.8) * mm});
            skLineSegment(sketch, "E1237", {"start": v(7.9, -13.8) * mm, "end": v(7.95, -13.85) * mm});
            skLineSegment(sketch, "E1238", {"start": v(7.95, -13.85) * mm, "end": v(8, -13.88) * mm});
            skLineSegment(sketch, "E1239", {"start": v(8, -13.88) * mm, "end": v(8.06, -13.93) * mm});
            skLineSegment(sketch, "E1240", {"start": v(8.06, -13.93) * mm, "end": v(8.12, -13.99) * mm});
            skLineSegment(sketch, "E1241", {"start": v(8.12, -13.99) * mm, "end": v(8.18, -14.03) * mm});
            skLineSegment(sketch, "E1242", {"start": v(8.18, -14.03) * mm, "end": v(8.6, -14.34) * mm});
            skLineSegment(sketch, "E1243", {"start": v(8.6, -14.34) * mm, "end": v(9.09, -14.64) * mm});
            skLineSegment(sketch, "E1244", {"start": v(9.09, -14.64) * mm, "end": v(9.59, -14.9) * mm});
            skLineSegment(sketch, "E1245", {"start": v(9.59, -14.9) * mm, "end": v(10.14, -15.14) * mm});
            skLineSegment(sketch, "E1246", {"start": v(10.14, -15.14) * mm, "end": v(10.6, -15.3) * mm});
            skLineSegment(sketch, "E1247", {"start": v(10.6, -15.3) * mm, "end": v(11.22, -15.47) * mm});
            skLineSegment(sketch, "E1248", {"start": v(11.22, -15.47) * mm, "end": v(12.05, -15.58) * mm});
            skLineSegment(sketch, "E1249", {"start": v(12.05, -15.58) * mm, "end": v(12.64, -15.62) * mm});
            skLineSegment(sketch, "E1250", {"start": v(12.64, -15.62) * mm, "end": v(13.23, -15.61) * mm});
            skLineSegment(sketch, "E1251", {"start": v(13.23, -15.61) * mm, "end": v(13.86, -15.54) * mm});
            skLineSegment(sketch, "E1252", {"start": v(13.86, -15.54) * mm, "end": v(14.6, -15.4) * mm});
            skLineSegment(sketch, "E1253", {"start": v(14.6, -15.4) * mm, "end": v(15.22, -15.22) * mm});
            skLineSegment(sketch, "E1254", {"start": v(15.22, -15.22) * mm, "end": v(15.96, -14.92) * mm});
            skLineSegment(sketch, "E1255", {"start": v(15.96, -14.92) * mm, "end": v(16.59, -14.6) * mm});
            skLineSegment(sketch, "E1256", {"start": v(16.59, -14.6) * mm, "end": v(17, -14.33) * mm});
            skLineSegment(sketch, "E1257", {"start": v(17, -14.33) * mm, "end": v(17.38, -14.05) * mm});
            skLineSegment(sketch, "E1258", {"start": v(17.38, -14.05) * mm, "end": v(17.65, -13.83) * mm});
            skLineSegment(sketch, "E1259", {"start": v(17.65, -13.83) * mm, "end": v(17.92, -13.59) * mm});
            skLineSegment(sketch, "E1260", {"start": v(17.92, -13.59) * mm, "end": v(18.2, -13.33) * mm});
            skLineSegment(sketch, "E1261", {"start": v(18.2, -13.33) * mm, "end": v(18.47, -13.02) * mm});
            skLineSegment(sketch, "E1262", {"start": v(18.47, -13.02) * mm, "end": v(18.65, -12.81) * mm});
            skLineSegment(sketch, "E1263", {"start": v(18.65, -12.81) * mm, "end": v(18.9, -12.48) * mm});
            skLineSegment(sketch, "E1264", {"start": v(18.9, -12.48) * mm, "end": v(19.08, -12.22) * mm});
            skLineSegment(sketch, "E1265", {"start": v(19.08, -12.22) * mm, "end": v(19.34, -11.79) * mm});
            skLineSegment(sketch, "E1266", {"start": v(19.34, -11.79) * mm, "end": v(19.56, -11.35) * mm});
            skLineSegment(sketch, "E1267", {"start": v(19.56, -11.35) * mm, "end": v(19.74, -10.96) * mm});
            skLineSegment(sketch, "E1268", {"start": v(19.74, -10.96) * mm, "end": v(19.98, -10.3) * mm});
            skLineSegment(sketch, "E1269", {"start": v(19.98, -10.3) * mm, "end": v(20.13, -9.74) * mm});
            skLineSegment(sketch, "E1270", {"start": v(20.13, -9.74) * mm, "end": v(20.23, -9.14) * mm});
            skLineSegment(sketch, "E1271", {"start": v(20.23, -9.14) * mm, "end": v(20.29, -8.64) * mm});
            skLineSegment(sketch, "E1272", {"start": v(20.29, -8.64) * mm, "end": v(20.3, -8.12) * mm});
            skLineSegment(sketch, "E1273", {"start": v(20.3, -8.12) * mm, "end": v(20.3, -7.75) * mm});
            skLineSegment(sketch, "E1274", {"start": v(20.3, -7.75) * mm, "end": v(20.28, -7.5) * mm});
            skLineSegment(sketch, "E1275", {"start": v(20.28, -7.5) * mm, "end": v(20.23, -7.03) * mm});
            skLineSegment(sketch, "E1276", {"start": v(20.23, -7.03) * mm, "end": v(20.17, -6.7) * mm});
            skLineSegment(sketch, "E1277", {"start": v(20.17, -6.7) * mm, "end": v(20.1, -6.32) * mm});
            skLineSegment(sketch, "E1278", {"start": v(20.1, -6.32) * mm, "end": v(20.07, -6.22) * mm});
            skLineSegment(sketch, "E1279", {"start": v(20.07, -6.22) * mm, "end": v(20.04, -6.1) * mm});
            skLineSegment(sketch, "E1280", {"start": v(20.04, -6.1) * mm, "end": v(19.97, -5.89) * mm});
            skLineSegment(sketch, "E1281", {"start": v(19.97, -5.89) * mm, "end": v(19.9, -5.67) * mm});
            skLineSegment(sketch, "E1282", {"start": v(19.9, -5.67) * mm, "end": v(19.83, -5.48) * mm});
            skLineSegment(sketch, "E1283", {"start": v(19.83, -5.48) * mm, "end": v(19.76, -5.3) * mm});
            skLineSegment(sketch, "E1284", {"start": v(19.76, -5.3) * mm, "end": v(19.4, -4.55) * mm});
            skLineSegment(sketch, "E1285", {"start": v(19.4, -4.55) * mm, "end": v(19.03, -3.95) * mm});
            skLineSegment(sketch, "E1286", {"start": v(19.03, -3.95) * mm, "end": v(18.61, -3.34) * mm});
            skLineSegment(sketch, "E1287", {"start": v(18.61, -3.34) * mm, "end": v(18.08, -2.78) * mm});
            skLineSegment(sketch, "E1288", {"start": v(18.08, -2.78) * mm, "end": v(17.55, -2.28) * mm});
            skLineSegment(sketch, "E1289", {"start": v(17.55, -2.28) * mm, "end": v(16.87, -1.81) * mm});
            skLineSegment(sketch, "E1290", {"start": v(16.87, -1.81) * mm, "end": v(16.23, -1.44) * mm});
            skLineSegment(sketch, "E1291", {"start": v(16.23, -1.44) * mm, "end": v(15.93, -1.29) * mm});
            skLineSegment(sketch, "E1292", {"start": v(15.93, -1.29) * mm, "end": v(15.55, -1.13) * mm});
            skLineSegment(sketch, "E1293", {"start": v(15.55, -1.13) * mm, "end": v(14.98, -0.93) * mm});
            skLineSegment(sketch, "E1294", {"start": v(14.98, -0.93) * mm, "end": v(14.19, -0.73) * mm});
            skLineSegment(sketch, "E1295", {"start": v(14.19, -0.73) * mm, "end": v(13.55, -0.64) * mm});
            skLineSegment(sketch, "E1296", {"start": v(13.55, -0.64) * mm, "end": v(12.9, -0.6) * mm});
            skLineSegment(sketch, "E1297", {"start": v(12.9, -0.6) * mm, "end": v(12.44, -0.6) * mm});
            skLineSegment(sketch, "E1298", {"start": v(12.44, -0.6) * mm, "end": v(11.93, -0.65) * mm});
            skLineSegment(sketch, "E1299", {"start": v(11.93, -0.65) * mm, "end": v(11.44, -0.72) * mm});
            skLineSegment(sketch, "E1300", {"start": v(11.44, -0.72) * mm, "end": v(10.85, -0.85) * mm});
            skLineSegment(sketch, "E1301", {"start": v(10.85, -0.85) * mm, "end": v(10.48, -0.97) * mm});
            skLineSegment(sketch, "E1302", {"start": v(10.48, -0.97) * mm, "end": v(10.02, -1.12) * mm});
            skLineSegment(sketch, "E1303", {"start": v(10.02, -1.12) * mm, "end": v(9.65, -1.28) * mm});
            skLineSegment(sketch, "E1304", {"start": v(9.65, -1.28) * mm, "end": v(9.14, -1.55) * mm});
            skLineSegment(sketch, "E1305", {"start": v(9.14, -1.55) * mm, "end": v(8.6, -1.9) * mm});
            skLineSegment(sketch, "E1306", {"start": v(8.6, -1.9) * mm, "end": v(8, -2.32) * mm});
            skLineSegment(sketch, "E1307", {"start": v(8, -2.32) * mm, "end": v(7.56, -2.73) * mm});
            skLineSegment(sketch, "E1308", {"start": v(7.56, -2.73) * mm, "end": v(7.02, -3.3) * mm});
            skLineSegment(sketch, "E1309", {"start": v(7.02, -3.3) * mm, "end": v(6.34, -4.25) * mm});
            skLineSegment(sketch, "E1310", {"start": v(6.34, -4.25) * mm, "end": v(5.86, -5.2) * mm});
            skLineSegment(sketch, "E1311", {"start": v(5.86, -5.2) * mm, "end": v(5.56, -6.14) * mm});
            skLineSegment(sketch, "E1312", {"start": v(5.56, -6.14) * mm, "end": v(5.35, -7.09) * mm});
            skLineSegment(sketch, "E1313", {"start": v(5.35, -7.09) * mm, "end": v(5.28, -7.73) * mm});
            skLineSegment(sketch, "E1314", {"start": v(5.28, -7.73) * mm, "end": v(5.3, -8.54) * mm});
            skLineSegment(sketch, "E1315", {"start": v(5.3, -8.54) * mm, "end": v(5.36, -9.32) * mm});
            skLineSegment(sketch, "E1316", {"start": v(5.36, -9.32) * mm, "end": v(5.56, -10.26) * mm});
            skLineSegment(sketch, "E1317", {"start": v(5.56, -10.26) * mm, "end": v(5.85, -11) * mm});
            skLineSegment(sketch, "E1318", {"start": v(5.85, -11) * mm, "end": v(5.98, -11.27) * mm});
            skLineSegment(sketch, "E1319", {"start": v(5.98, -11.27) * mm, "end": v(6.13, -11.57) * mm});
            skLineSegment(sketch, "E1320", {"start": v(6.13, -11.57) * mm, "end": v(6.2, -11.7) * mm});
            skLineSegment(sketch, "E1321", {"start": v(8.2, -12.33) * mm, "end": v(10.27, -12.33) * mm});
            skLineSegment(sketch, "E1322", {"start": v(10.27, -12.33) * mm, "end": v(10.26, -7.82) * mm});
            skLineSegment(sketch, "E1323", {"start": v(10.26, -7.82) * mm, "end": v(16.53, -7.86) * mm});
            skLineSegment(sketch, "E1324", {"start": v(16.53, -7.86) * mm, "end": v(18.33, -10.83) * mm});
            skLineSegment(sketch, "E1325", {"start": v(18.33, -10.83) * mm, "end": v(18.4, -10.7) * mm});
            skLineSegment(sketch, "E1326", {"start": v(18.4, -10.7) * mm, "end": v(18.66, -10) * mm});
            skLineSegment(sketch, "E1327", {"start": v(18.66, -10) * mm, "end": v(18.75, -9.66) * mm});
            skLineSegment(sketch, "E1328", {"start": v(18.75, -9.66) * mm, "end": v(18.83, -9.25) * mm});
            skLineSegment(sketch, "E1329", {"start": v(18.83, -9.25) * mm, "end": v(18.86, -9) * mm});
            skLineSegment(sketch, "E1330", {"start": v(18.86, -9) * mm, "end": v(18.9, -8.62) * mm});
            skLineSegment(sketch, "E1331", {"start": v(18.9, -8.62) * mm, "end": v(18.9, -8.46) * mm});
            skLineSegment(sketch, "E1332", {"start": v(18.9, -8.46) * mm, "end": v(18.9, -7.77) * mm});
            skLineSegment(sketch, "E1333", {"start": v(18.9, -7.77) * mm, "end": v(18.8, -6.8) * mm});
            skLineSegment(sketch, "E1334", {"start": v(18.8, -6.8) * mm, "end": v(18.56, -6) * mm});
            skLineSegment(sketch, "E1335", {"start": v(18.56, -6) * mm, "end": v(18.17, -5.14) * mm});
            skLineSegment(sketch, "E1336", {"start": v(18.17, -5.14) * mm, "end": v(17.74, -4.52) * mm});
            skLineSegment(sketch, "E1337", {"start": v(17.74, -4.52) * mm, "end": v(17.22, -3.87) * mm});
            skLineSegment(sketch, "E1338", {"start": v(17.22, -3.87) * mm, "end": v(16.7, -3.37) * mm});
            skLineSegment(sketch, "E1339", {"start": v(16.7, -3.37) * mm, "end": v(16.18, -2.98) * mm});
            skLineSegment(sketch, "E1340", {"start": v(16.18, -2.98) * mm, "end": v(15.26, -2.48) * mm});
            skLineSegment(sketch, "E1341", {"start": v(15.26, -2.48) * mm, "end": v(14.43, -2.16) * mm});
            skLineSegment(sketch, "E1342", {"start": v(14.43, -2.16) * mm, "end": v(13.72, -2.02) * mm});
            skLineSegment(sketch, "E1343", {"start": v(13.72, -2.02) * mm, "end": v(12.87, -1.93) * mm});
            skLineSegment(sketch, "E1344", {"start": v(12.87, -1.93) * mm, "end": v(11.96, -2) * mm});
            skLineSegment(sketch, "E1345", {"start": v(11.96, -2) * mm, "end": v(11.15, -2.18) * mm});
            skLineSegment(sketch, "E1346", {"start": v(11.15, -2.18) * mm, "end": v(10.4, -2.37) * mm});
            skLineSegment(sketch, "E1347", {"start": v(10.4, -2.37) * mm, "end": v(9.78, -2.7) * mm});
            skLineSegment(sketch, "E1348", {"start": v(9.78, -2.7) * mm, "end": v(9.07, -3.15) * mm});
            skLineSegment(sketch, "E1349", {"start": v(9.07, -3.15) * mm, "end": v(8.52, -3.6) * mm});
            skLineSegment(sketch, "E1350", {"start": v(8.52, -3.6) * mm, "end": v(7.94, -4.28) * mm});
            skLineSegment(sketch, "E1351", {"start": v(7.94, -4.28) * mm, "end": v(7.47, -4.95) * mm});
            skLineSegment(sketch, "E1352", {"start": v(7.47, -4.95) * mm, "end": v(7.01, -5.82) * mm});
            skLineSegment(sketch, "E1353", {"start": v(7.01, -5.82) * mm, "end": v(6.72, -6.8) * mm});
            skLineSegment(sketch, "E1354", {"start": v(6.72, -6.8) * mm, "end": v(6.58, -8) * mm});
            skLineSegment(sketch, "E1355", {"start": v(6.58, -8) * mm, "end": v(6.6, -8.7) * mm});
            skLineSegment(sketch, "E1356", {"start": v(6.6, -8.7) * mm, "end": v(6.7, -9.37) * mm});
            skLineSegment(sketch, "E1357", {"start": v(6.7, -9.37) * mm, "end": v(6.9, -10.18) * mm});
            skLineSegment(sketch, "E1358", {"start": v(6.9, -10.18) * mm, "end": v(7.1, -10.7) * mm});
            skLineSegment(sketch, "E1359", {"start": v(7.1, -10.7) * mm, "end": v(7.38, -11.3) * mm});
            skLineSegment(sketch, "E1360", {"start": v(7.38, -11.3) * mm, "end": v(7.78, -11.86) * mm});
            skLineSegment(sketch, "E1361", {"start": v(7.78, -11.86) * mm, "end": v(8.2, -12.33) * mm});
            skSolve(sketch);
        }
        {
            var Q0;
            Q0 = qSketchRegion(id + "F21", true);
            extrude(context, id + "F22", {"entities" : qUnion([Q0]), "operationType" : NewBodyOperationType.ADD, "depth" : 2.54 * mm, "offsetDistance" : 25.4 * mm});
        }
    });
